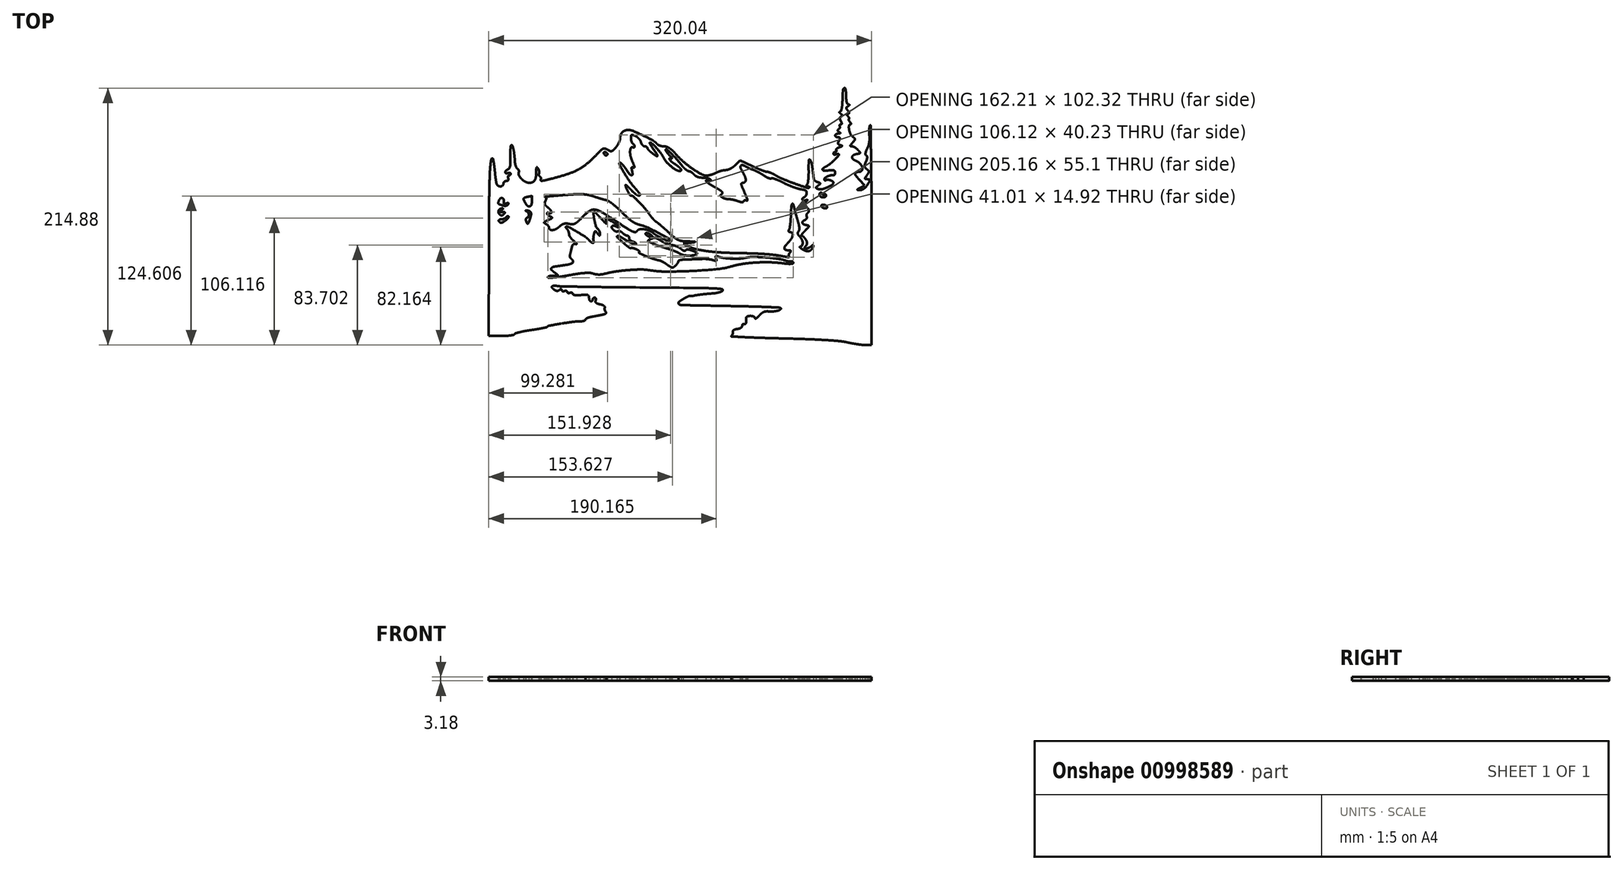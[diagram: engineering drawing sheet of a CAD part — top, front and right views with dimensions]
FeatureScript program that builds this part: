
annotation { "Feature Type Name" : "Feature", "Feature Type Description" : "" }
export const myFeature = defineFeature(function(context is Context, id is Id, definition is map)
    precondition{}
    {
        {
            var Q0;
            Q0=qCreatedBy(makeId("Top.planeOp"),FACE);
            var sketch = newSketch(context, id + "F0", { "sketchPlane" : qUnion([Q0])});
            skArc(sketch, "E0", {"start": v(136, 105.54) * mm, "mid": v(135.97, 104.96) * mm, "end": v(135.94, 104.37) * mm});
            skArc(sketch, "E1", {"start": v(135.94, 104.37) * mm, "mid": v(135.88, 103.1) * mm, "end": v(135.82, 101.84) * mm});
            skArc(sketch, "E2", {"start": v(135.82, 101.84) * mm, "mid": v(135.75, 100.34) * mm, "end": v(135.69, 98.83) * mm});
            skArc(sketch, "E3", {"start": v(135.69, 98.83) * mm, "mid": v(135.62, 97.23) * mm, "end": v(135.55, 95.63) * mm});
            skArc(sketch, "E4", {"start": v(135.55, 95.63) * mm, "mid": v(135.46, 94.03) * mm, "end": v(135.31, 92.43) * mm});
            skArc(sketch, "E5", {"start": v(135.31, 92.43) * mm, "mid": v(135.12, 91.14) * mm, "end": v(134.85, 89.87) * mm});
            skArc(sketch, "E6", {"start": v(134.85, 89.87) * mm, "mid": v(134.58, 88.96) * mm, "end": v(134.24, 88.08) * mm});
            skArc(sketch, "E7", {"start": v(134.24, 88.08) * mm, "mid": v(133.96, 87.74) * mm, "end": v(133.53, 87.6) * mm});
            skArc(sketch, "E8", {"start": v(133.53, 87.6) * mm, "mid": v(133.3, 87.57) * mm, "end": v(133.1, 87.45) * mm});
            skArc(sketch, "E9", {"start": v(133.1, 87.45) * mm, "mid": v(133, 87.3) * mm, "end": v(133, 87.12) * mm});
            skArc(sketch, "E10", {"start": v(133, 87.12) * mm, "mid": v(133.14, 86.83) * mm, "end": v(133.34, 86.6) * mm});
            skArc(sketch, "E11", {"start": v(133.34, 86.6) * mm, "mid": v(133.72, 86.27) * mm, "end": v(134.11, 85.97) * mm});
            skArc(sketch, "E12", {"start": v(134.11, 85.97) * mm, "mid": v(134.64, 85.57) * mm, "end": v(135.15, 85.14) * mm});
            skArc(sketch, "E13", {"start": v(135.15, 85.14) * mm, "mid": v(135.37, 84.87) * mm, "end": v(135.48, 84.54) * mm});
            skArc(sketch, "E14", {"start": v(135.48, 84.54) * mm, "mid": v(135.45, 84.26) * mm, "end": v(135.29, 84.03) * mm});
            skArc(sketch, "E15", {"start": v(135.29, 84.03) * mm, "mid": v(134.91, 83.78) * mm, "end": v(134.5, 83.58) * mm});
            skArc(sketch, "E16", {"start": v(134.5, 83.58) * mm, "mid": v(134.09, 83.36) * mm, "end": v(133.73, 83.05) * mm});
            skArc(sketch, "E17", {"start": v(133.73, 83.05) * mm, "mid": v(133.5, 82.71) * mm, "end": v(133.4, 82.32) * mm});
            skArc(sketch, "E18", {"start": v(133.4, 82.32) * mm, "mid": v(133.41, 81.8) * mm, "end": v(133.54, 81.31) * mm});
            skArc(sketch, "E19", {"start": v(133.54, 81.31) * mm, "mid": v(133.83, 80.59) * mm, "end": v(134.18, 79.89) * mm});
            skArc(sketch, "E20", {"start": v(134.18, 79.89) * mm, "mid": v(134.52, 79.22) * mm, "end": v(134.82, 78.53) * mm});
            skArc(sketch, "E21", {"start": v(134.82, 78.53) * mm, "mid": v(134.95, 78.1) * mm, "end": v(134.98, 77.65) * mm});
            skArc(sketch, "E22", {"start": v(134.98, 77.65) * mm, "mid": v(134.9, 77.38) * mm, "end": v(134.7, 77.16) * mm});
            skArc(sketch, "E23", {"start": v(134.7, 77.16) * mm, "mid": v(134.4, 77.01) * mm, "end": v(134.08, 76.96) * mm});
            skArc(sketch, "E24", {"start": v(134.08, 76.96) * mm, "mid": v(133.79, 76.93) * mm, "end": v(133.5, 76.85) * mm});
            skArc(sketch, "E25", {"start": v(133.5, 76.85) * mm, "mid": v(133.3, 76.73) * mm, "end": v(133.16, 76.55) * mm});
            skArc(sketch, "E26", {"start": v(133.16, 76.55) * mm, "mid": v(133.08, 76.32) * mm, "end": v(133.08, 76.08) * mm});
            skArc(sketch, "E27", {"start": v(133.08, 76.08) * mm, "mid": v(133.16, 75.8) * mm, "end": v(133.28, 75.54) * mm});
            skArc(sketch, "E28", {"start": v(133.28, 75.54) * mm, "mid": v(133.42, 75.24) * mm, "end": v(133.49, 74.92) * mm});
            skArc(sketch, "E29", {"start": v(133.49, 74.92) * mm, "mid": v(133.48, 74.57) * mm, "end": v(133.4, 74.23) * mm});
            skArc(sketch, "E30", {"start": v(133.4, 74.23) * mm, "mid": v(133.25, 73.89) * mm, "end": v(133.04, 73.58) * mm});
            skArc(sketch, "E31", {"start": v(133.04, 73.58) * mm, "mid": v(132.76, 73.3) * mm, "end": v(132.45, 73.07) * mm});
            skArc(sketch, "E32", {"start": v(132.45, 73.07) * mm, "mid": v(132.1, 72.81) * mm, "end": v(131.79, 72.5) * mm});
            skArc(sketch, "E33", {"start": v(131.79, 72.5) * mm, "mid": v(131.64, 72.25) * mm, "end": v(131.62, 71.95) * mm});
            skArc(sketch, "E34", {"start": v(131.62, 71.95) * mm, "mid": v(131.73, 71.63) * mm, "end": v(131.94, 71.36) * mm});
            skArc(sketch, "E35", {"start": v(131.94, 71.36) * mm, "mid": v(132.36, 71.01) * mm, "end": v(132.8, 70.7) * mm});
            skArc(sketch, "E36", {"start": v(132.8, 70.7) * mm, "mid": v(133.3, 70.37) * mm, "end": v(133.8, 70.01) * mm});
            skArc(sketch, "E37", {"start": v(133.8, 70.01) * mm, "mid": v(133.9, 69.85) * mm, "end": v(133.89, 69.66) * mm});
            skArc(sketch, "E38", {"start": v(133.89, 69.66) * mm, "mid": v(133.75, 69.5) * mm, "end": v(133.55, 69.42) * mm});
            skArc(sketch, "E39", {"start": v(133.55, 69.42) * mm, "mid": v(132.88, 69.38) * mm, "end": v(132.2, 69.37) * mm});
            skArc(sketch, "E40", {"start": v(132.2, 69.37) * mm, "mid": v(131.7, 69.33) * mm, "end": v(131.19, 69.24) * mm});
            skArc(sketch, "E41", {"start": v(131.19, 69.24) * mm, "mid": v(130.74, 69.1) * mm, "end": v(130.32, 68.9) * mm});
            skArc(sketch, "E42", {"start": v(130.32, 68.9) * mm, "mid": v(130.01, 68.68) * mm, "end": v(129.74, 68.4) * mm});
            skArc(sketch, "E43", {"start": v(129.74, 68.4) * mm, "mid": v(129.6, 68.13) * mm, "end": v(129.54, 67.82) * mm});
            skArc(sketch, "E44", {"start": v(129.54, 67.82) * mm, "mid": v(129.59, 67.51) * mm, "end": v(129.72, 67.24) * mm});
            skArc(sketch, "E45", {"start": v(129.72, 67.24) * mm, "mid": v(129.95, 66.96) * mm, "end": v(130.23, 66.74) * mm});
            skArc(sketch, "E46", {"start": v(130.23, 66.74) * mm, "mid": v(130.6, 66.54) * mm, "end": v(130.99, 66.4) * mm});
            skArc(sketch, "E47", {"start": v(130.99, 66.4) * mm, "mid": v(131.43, 66.32) * mm, "end": v(131.88, 66.3) * mm});
            skArc(sketch, "E48", {"start": v(131.88, 66.3) * mm, "mid": v(132.43, 66.26) * mm, "end": v(132.96, 66.15) * mm});
            skArc(sketch, "E49", {"start": v(132.96, 66.15) * mm, "mid": v(133.25, 65.98) * mm, "end": v(133.42, 65.7) * mm});
            skArc(sketch, "E50", {"start": v(133.42, 65.7) * mm, "mid": v(133.46, 65.27) * mm, "end": v(133.36, 64.87) * mm});
            skArc(sketch, "E51", {"start": v(133.36, 64.87) * mm, "mid": v(133.02, 64.1) * mm, "end": v(132.65, 63.36) * mm});
            skArc(sketch, "E52", {"start": v(132.65, 63.36) * mm, "mid": v(132.28, 62.6) * mm, "end": v(131.96, 61.82) * mm});
            skArc(sketch, "E53", {"start": v(131.96, 61.82) * mm, "mid": v(131.87, 61.35) * mm, "end": v(131.93, 60.87) * mm});
            skArc(sketch, "E54", {"start": v(131.93, 60.87) * mm, "mid": v(132.14, 60.48) * mm, "end": v(132.47, 60.2) * mm});
            skArc(sketch, "E55", {"start": v(132.47, 60.2) * mm, "mid": v(133.1, 59.92) * mm, "end": v(133.74, 59.7) * mm});
            skArc(sketch, "E56", {"start": v(133.74, 59.7) * mm, "mid": v(134.44, 59.5) * mm, "end": v(135.13, 59.28) * mm});
            skArc(sketch, "E57", {"start": v(135.13, 59.28) * mm, "mid": v(135.29, 59.13) * mm, "end": v(135.3, 58.93) * mm});
            skArc(sketch, "E58", {"start": v(135.3, 58.93) * mm, "mid": v(135.13, 58.7) * mm, "end": v(134.9, 58.55) * mm});
            skArc(sketch, "E59", {"start": v(134.9, 58.55) * mm, "mid": v(133.94, 58.22) * mm, "end": v(132.99, 57.9) * mm});
            skArc(sketch, "E60", {"start": v(132.99, 57.9) * mm, "mid": v(132.35, 57.67) * mm, "end": v(131.74, 57.38) * mm});
            skArc(sketch, "E61", {"start": v(131.74, 57.38) * mm, "mid": v(131.26, 57.09) * mm, "end": v(130.82, 56.73) * mm});
            skArc(sketch, "E62", {"start": v(130.82, 56.73) * mm, "mid": v(130.55, 56.42) * mm, "end": v(130.36, 56.05) * mm});
            skArc(sketch, "E63", {"start": v(130.36, 56.05) * mm, "mid": v(130.31, 55.75) * mm, "end": v(130.4, 55.45) * mm});
            skArc(sketch, "E64", {"start": v(130.4, 55.45) * mm, "mid": v(130.53, 55.2) * mm, "end": v(130.6, 54.94) * mm});
            skArc(sketch, "E65", {"start": v(130.6, 54.94) * mm, "mid": v(130.6, 54.71) * mm, "end": v(130.52, 54.5) * mm});
            skArc(sketch, "E66", {"start": v(130.52, 54.5) * mm, "mid": v(130.38, 54.32) * mm, "end": v(130.18, 54.2) * mm});
            skArc(sketch, "E67", {"start": v(130.18, 54.2) * mm, "mid": v(129.91, 54.13) * mm, "end": v(129.63, 54.1) * mm});
            skArc(sketch, "E68", {"start": v(129.63, 54.1) * mm, "mid": v(129.32, 54.07) * mm, "end": v(129.01, 53.99) * mm});
            skArc(sketch, "E69", {"start": v(129.01, 53.99) * mm, "mid": v(128.74, 53.85) * mm, "end": v(128.5, 53.67) * mm});
            skArc(sketch, "E70", {"start": v(128.5, 53.67) * mm, "mid": v(128.3, 53.45) * mm, "end": v(128.14, 53.19) * mm});
            skArc(sketch, "E71", {"start": v(128.14, 53.19) * mm, "mid": v(128.05, 52.91) * mm, "end": v(128.02, 52.63) * mm});
            skArc(sketch, "E72", {"start": v(128.02, 52.63) * mm, "mid": v(128.06, 52.36) * mm, "end": v(128.2, 52.14) * mm});
            skArc(sketch, "E73", {"start": v(128.2, 52.14) * mm, "mid": v(128.42, 51.95) * mm, "end": v(128.69, 51.84) * mm});
            skArc(sketch, "E74", {"start": v(128.69, 51.84) * mm, "mid": v(129.05, 51.78) * mm, "end": v(129.43, 51.8) * mm});
            skArc(sketch, "E75", {"start": v(129.43, 51.8) * mm, "mid": v(129.87, 51.89) * mm, "end": v(130.3, 52.03) * mm});
            skArc(sketch, "E76", {"start": v(130.3, 52.03) * mm, "mid": v(130.74, 52.18) * mm, "end": v(131.18, 52.3) * mm});
            skArc(sketch, "E77", {"start": v(131.18, 52.3) * mm, "mid": v(131.54, 52.37) * mm, "end": v(131.92, 52.4) * mm});
            skArc(sketch, "E78", {"start": v(131.92, 52.4) * mm, "mid": v(132.17, 52.38) * mm, "end": v(132.41, 52.31) * mm});
            skArc(sketch, "E79", {"start": v(132.41, 52.31) * mm, "mid": v(132.54, 52.21) * mm, "end": v(132.59, 52.06) * mm});
            skArc(sketch, "E80", {"start": v(132.59, 52.06) * mm, "mid": v(132.43, 51.22) * mm, "end": v(131.98, 50.5) * mm});
            skArc(sketch, "E81", {"start": v(131.98, 50.5) * mm, "mid": v(130.39, 48.82) * mm, "end": v(128.75, 47.19) * mm});
            skArc(sketch, "E82", {"start": v(128.75, 47.19) * mm, "mid": v(127.01, 45.57) * mm, "end": v(125.2, 44.02) * mm});
            skArc(sketch, "E83", {"start": v(125.2, 44.02) * mm, "mid": v(123.8, 42.98) * mm, "end": v(122.3, 42.09) * mm});
            skArc(sketch, "E84", {"start": v(122.3, 42.09) * mm, "mid": v(120.8, 41.23) * mm, "end": v(119.37, 40.28) * mm});
            skArc(sketch, "E85", {"start": v(119.37, 40.28) * mm, "mid": v(119, 39.73) * mm, "end": v(119.08, 39.07) * mm});
            skArc(sketch, "E86", {"start": v(119.08, 39.07) * mm, "mid": v(119.62, 38.52) * mm, "end": v(120.36, 38.32) * mm});
            skArc(sketch, "E87", {"start": v(120.36, 38.32) * mm, "mid": v(122.29, 38.4) * mm, "end": v(124.2, 38.57) * mm});
            skArc(sketch, "E88", {"start": v(124.2, 38.57) * mm, "mid": v(125.56, 38.7) * mm, "end": v(126.93, 38.78) * mm});
            skArc(sketch, "E89", {"start": v(126.93, 38.78) * mm, "mid": v(127.7, 38.74) * mm, "end": v(128.45, 38.55) * mm});
            skArc(sketch, "E90", {"start": v(128.45, 38.55) * mm, "mid": v(128.9, 38.28) * mm, "end": v(129.24, 37.86) * mm});
            skArc(sketch, "E91", {"start": v(129.24, 37.86) * mm, "mid": v(129.46, 37.29) * mm, "end": v(129.54, 36.68) * mm});
            skArc(sketch, "E92", {"start": v(129.54, 36.68) * mm, "mid": v(129.5, 36.2) * mm, "end": v(129.4, 35.74) * mm});
            skArc(sketch, "E93", {"start": v(129.4, 35.74) * mm, "mid": v(129.23, 35.34) * mm, "end": v(128.98, 34.99) * mm});
            skArc(sketch, "E94", {"start": v(128.98, 34.99) * mm, "mid": v(128.7, 34.73) * mm, "end": v(128.36, 34.54) * mm});
            skArc(sketch, "E95", {"start": v(128.36, 34.54) * mm, "mid": v(128, 34.45) * mm, "end": v(127.64, 34.46) * mm});
            skArc(sketch, "E96", {"start": v(127.64, 34.46) * mm, "mid": v(126.55, 34.53) * mm, "end": v(125.47, 34.4) * mm});
            skArc(sketch, "E97", {"start": v(125.47, 34.4) * mm, "mid": v(124.21, 34.03) * mm, "end": v(123, 33.54) * mm});
            skArc(sketch, "E98", {"start": v(123, 33.54) * mm, "mid": v(121.97, 32.96) * mm, "end": v(121, 32.27) * mm});
            skArc(sketch, "E99", {"start": v(121, 32.27) * mm, "mid": v(120.56, 31.7) * mm, "end": v(120.4, 30.99) * mm});
            skArc(sketch, "E100", {"start": v(120.4, 30.99) * mm, "mid": v(120.42, 30.74) * mm, "end": v(120.5, 30.5) * mm});
            skArc(sketch, "E101", {"start": v(120.5, 30.5) * mm, "mid": v(120.63, 30.33) * mm, "end": v(120.8, 30.22) * mm});
            skArc(sketch, "E102", {"start": v(120.8, 30.22) * mm, "mid": v(121.02, 30.16) * mm, "end": v(121.25, 30.18) * mm});
            skArc(sketch, "E103", {"start": v(121.25, 30.18) * mm, "mid": v(121.53, 30.26) * mm, "end": v(121.78, 30.4) * mm});
            skArc(sketch, "E104", {"start": v(121.78, 30.4) * mm, "mid": v(122.51, 30.7) * mm, "end": v(123.3, 30.76) * mm});
            skArc(sketch, "E105", {"start": v(123.3, 30.76) * mm, "mid": v(124.42, 30.6) * mm, "end": v(125.5, 30.32) * mm});
            skArc(sketch, "E106", {"start": v(125.5, 30.32) * mm, "mid": v(126.5, 29.93) * mm, "end": v(127.42, 29.42) * mm});
            skArc(sketch, "E107", {"start": v(127.42, 29.42) * mm, "mid": v(127.86, 28.97) * mm, "end": v(128.02, 28.36) * mm});
            skArc(sketch, "E108", {"start": v(128.02, 28.36) * mm, "mid": v(127.75, 27.32) * mm, "end": v(127, 26.54) * mm});
            skArc(sketch, "E109", {"start": v(127, 26.54) * mm, "mid": v(125.03, 25.4) * mm, "end": v(122.99, 24.41) * mm});
            skArc(sketch, "E110", {"start": v(122.99, 24.41) * mm, "mid": v(120.8, 23.55) * mm, "end": v(118.58, 22.84) * mm});
            skArc(sketch, "E111", {"start": v(118.58, 22.84) * mm, "mid": v(117.13, 22.66) * mm, "end": v(115.7, 22.9) * mm});
            skArc(sketch, "E112", {"start": v(115.7, 22.9) * mm, "mid": v(114.75, 23.22) * mm, "end": v(113.8, 23.56) * mm});
            skArc(sketch, "E113", {"start": v(113.8, 23.56) * mm, "mid": v(113.55, 23.75) * mm, "end": v(113.42, 24.04) * mm});
            skArc(sketch, "E114", {"start": v(113.42, 24.04) * mm, "mid": v(113.46, 24.35) * mm, "end": v(113.64, 24.61) * mm});
            skArc(sketch, "E115", {"start": v(113.64, 24.61) * mm, "mid": v(114.43, 25.24) * mm, "end": v(115.24, 25.85) * mm});
            skArc(sketch, "E116", {"start": v(115.24, 25.85) * mm, "mid": v(116.05, 26.46) * mm, "end": v(116.85, 27.1) * mm});
            skArc(sketch, "E117", {"start": v(116.85, 27.1) * mm, "mid": v(117.03, 27.35) * mm, "end": v(117.07, 27.66) * mm});
            skArc(sketch, "E118", {"start": v(117.07, 27.66) * mm, "mid": v(116.95, 27.95) * mm, "end": v(116.7, 28.13) * mm});
            skArc(sketch, "E119", {"start": v(116.7, 28.13) * mm, "mid": v(115.77, 28.47) * mm, "end": v(114.84, 28.78) * mm});
            skArc(sketch, "E120", {"start": v(114.84, 28.78) * mm, "mid": v(114.23, 29.01) * mm, "end": v(113.65, 29.3) * mm});
            skArc(sketch, "E121", {"start": v(113.65, 29.3) * mm, "mid": v(113.1, 29.64) * mm, "end": v(112.6, 30.03) * mm});
            skArc(sketch, "E122", {"start": v(112.6, 30.03) * mm, "mid": v(112.2, 30.42) * mm, "end": v(111.86, 30.85) * mm});
            skArc(sketch, "E123", {"start": v(111.86, 30.85) * mm, "mid": v(111.66, 31.23) * mm, "end": v(111.56, 31.65) * mm});
            skArc(sketch, "E124", {"start": v(111.56, 31.65) * mm, "mid": v(110.9, 37.43) * mm, "end": v(110.15, 43.2) * mm});
            skArc(sketch, "E125", {"start": v(110.15, 43.2) * mm, "mid": v(109.61, 45.37) * mm, "end": v(108.64, 47.38) * mm});
            skArc(sketch, "E126", {"start": v(108.64, 47.38) * mm, "mid": v(107.94, 47.66) * mm, "end": v(107.46, 47.08) * mm});
            skArc(sketch, "E127", {"start": v(107.46, 47.08) * mm, "mid": v(107.33, 42.78) * mm, "end": v(107.34, 38.48) * mm});
            skArc(sketch, "E128", {"start": v(107.34, 38.48) * mm, "mid": v(107.35, 36.59) * mm, "end": v(107.31, 34.7) * mm});
            skArc(sketch, "E129", {"start": v(107.31, 34.7) * mm, "mid": v(107.22, 32.94) * mm, "end": v(107.07, 31.2) * mm});
            skArc(sketch, "E130", {"start": v(107.07, 31.2) * mm, "mid": v(106.9, 29.75) * mm, "end": v(106.68, 28.31) * mm});
            skArc(sketch, "E131", {"start": v(106.68, 28.31) * mm, "mid": v(106.5, 27.65) * mm, "end": v(106.16, 27.05) * mm});
            skArc(sketch, "E132", {"start": v(106.16, 27.05) * mm, "mid": v(105.9, 26.65) * mm, "end": v(105.67, 26.22) * mm});
            skArc(sketch, "E133", {"start": v(105.67, 26.22) * mm, "mid": v(105.6, 25.93) * mm, "end": v(105.63, 25.63) * mm});
            skArc(sketch, "E134", {"start": v(105.63, 25.63) * mm, "mid": v(105.77, 25.4) * mm, "end": v(105.99, 25.27) * mm});
            skArc(sketch, "E135", {"start": v(105.99, 25.27) * mm, "mid": v(106.36, 25.18) * mm, "end": v(106.75, 25.15) * mm});
            skArc(sketch, "E136", {"start": v(106.75, 25.15) * mm, "mid": v(107.1, 25.13) * mm, "end": v(107.45, 25.1) * mm});
            skArc(sketch, "E137", {"start": v(107.45, 25.1) * mm, "mid": v(107.7, 25.03) * mm, "end": v(107.91, 24.92) * mm});
            skArc(sketch, "E138", {"start": v(107.91, 24.92) * mm, "mid": v(108.02, 24.82) * mm, "end": v(108.06, 24.67) * mm});
            skArc(sketch, "E139", {"start": v(108.06, 24.67) * mm, "mid": v(108.04, 24.52) * mm, "end": v(107.95, 24.39) * mm});
            skArc(sketch, "E140", {"start": v(107.95, 24.39) * mm, "mid": v(107.13, 23.93) * mm, "end": v(106.18, 23.97) * mm});
            skArc(sketch, "E141", {"start": v(106.18, 23.97) * mm, "mid": v(100.97, 25.74) * mm, "end": v(95.77, 27.55) * mm});
            skArc(sketch, "E142", {"start": v(95.77, 27.55) * mm, "mid": v(90.84, 29.36) * mm, "end": v(85.95, 31.27) * mm});
            skArc(sketch, "E143", {"start": v(85.95, 31.27) * mm, "mid": v(82.96, 32.63) * mm, "end": v(80.1, 34.24) * mm});
            skArc(sketch, "E144", {"start": v(80.1, 34.24) * mm, "mid": v(79.06, 34.85) * mm, "end": v(78, 35.43) * mm});
            skArc(sketch, "E145", {"start": v(78, 35.43) * mm, "mid": v(76.95, 35.95) * mm, "end": v(75.87, 36.43) * mm});
            skArc(sketch, "E146", {"start": v(75.87, 36.43) * mm, "mid": v(74.93, 36.8) * mm, "end": v(73.98, 37.14) * mm});
            skArc(sketch, "E147", {"start": v(73.98, 37.14) * mm, "mid": v(73.38, 37.29) * mm, "end": v(72.76, 37.34) * mm});
            skArc(sketch, "E148", {"start": v(72.76, 37.34) * mm, "mid": v(72.05, 37.4) * mm, "end": v(71.35, 37.57) * mm});
            skArc(sketch, "E149", {"start": v(71.35, 37.57) * mm, "mid": v(69.74, 38.14) * mm, "end": v(68.14, 38.74) * mm});
            skArc(sketch, "E150", {"start": v(68.14, 38.74) * mm, "mid": v(66.23, 39.49) * mm, "end": v(64.34, 40.28) * mm});
            skArc(sketch, "E151", {"start": v(64.34, 40.28) * mm, "mid": v(62.3, 41.17) * mm, "end": v(60.27, 42.1) * mm});
            skLineSegment(sketch, "E152", {"start": v(60.27, 42.1) * mm, "end": v(50.1, 46.86) * mm});
            skLineSegment(sketch, "E153", {"start": v(50.1, 46.86) * mm, "end": v(45.92, 42.86) * mm});
            skArc(sketch, "E154", {"start": v(45.92, 42.86) * mm, "mid": v(45.01, 42.06) * mm, "end": v(44.05, 41.33) * mm});
            skArc(sketch, "E155", {"start": v(44.05, 41.33) * mm, "mid": v(42.98, 40.65) * mm, "end": v(41.87, 40.03) * mm});
            skArc(sketch, "E156", {"start": v(41.87, 40.03) * mm, "mid": v(40.82, 39.55) * mm, "end": v(39.74, 39.14) * mm});
            skArc(sketch, "E157", {"start": v(39.74, 39.14) * mm, "mid": v(38.9, 38.93) * mm, "end": v(38.02, 38.85) * mm});
            skArc(sketch, "E158", {"start": v(38.02, 38.85) * mm, "mid": v(37.14, 38.81) * mm, "end": v(36.28, 38.69) * mm});
            skArc(sketch, "E159", {"start": v(36.28, 38.69) * mm, "mid": v(35.18, 38.46) * mm, "end": v(34.1, 38.18) * mm});
            skArc(sketch, "E160", {"start": v(34.1, 38.18) * mm, "mid": v(32.98, 37.83) * mm, "end": v(31.87, 37.44) * mm});
            skArc(sketch, "E161", {"start": v(31.87, 37.44) * mm, "mid": v(30.88, 37.03) * mm, "end": v(29.92, 36.57) * mm});
            skArc(sketch, "E162", {"start": v(29.92, 36.57) * mm, "mid": v(28.97, 36.1) * mm, "end": v(28, 35.7) * mm});
            skArc(sketch, "E163", {"start": v(28, 35.7) * mm, "mid": v(26.92, 35.3) * mm, "end": v(25.82, 34.96) * mm});
            skArc(sketch, "E164", {"start": v(25.82, 34.96) * mm, "mid": v(24.78, 34.68) * mm, "end": v(23.72, 34.45) * mm});
            skArc(sketch, "E165", {"start": v(23.72, 34.45) * mm, "mid": v(22.9, 34.33) * mm, "end": v(22.08, 34.3) * mm});
            skArc(sketch, "E166", {"start": v(22.08, 34.3) * mm, "mid": v(19.75, 34.59) * mm, "end": v(17.57, 35.46) * mm});
            skArc(sketch, "E167", {"start": v(17.57, 35.46) * mm, "mid": v(13.88, 37.63) * mm, "end": v(10.3, 39.97) * mm});
            skArc(sketch, "E168", {"start": v(10.3, 39.97) * mm, "mid": v(6.45, 42.78) * mm, "end": v(2.75, 45.78) * mm});
            skArc(sketch, "E169", {"start": v(2.75, 45.79) * mm, "mid": v(-0.44, 48.72) * mm, "end": v(-3.42, 51.87) * mm});
            skArc(sketch, "E170", {"start": v(-3.42, 51.87) * mm, "mid": v(-4.92, 53.52) * mm, "end": v(-6.48, 55.1) * mm});
            skArc(sketch, "E171", {"start": v(-6.48, 55.1) * mm, "mid": v(-7.7, 56.18) * mm, "end": v(-9.02, 57.15) * mm});
            skArc(sketch, "E172", {"start": v(-9.02, 57.15) * mm, "mid": v(-10.13, 57.8) * mm, "end": v(-11.33, 58.29) * mm});
            skArc(sketch, "E173", {"start": v(-11.33, 58.29) * mm, "mid": v(-12.48, 58.58) * mm, "end": v(-13.66, 58.67) * mm});
            skArc(sketch, "E174", {"start": v(-13.66, 58.67) * mm, "mid": v(-14.55, 58.72) * mm, "end": v(-15.44, 58.85) * mm});
            skArc(sketch, "E175", {"start": v(-15.44, 58.85) * mm, "mid": v(-16.36, 59.08) * mm, "end": v(-17.26, 59.39) * mm});
            skArc(sketch, "E176", {"start": v(-17.26, 59.39) * mm, "mid": v(-18.07, 59.75) * mm, "end": v(-18.85, 60.18) * mm});
            skArc(sketch, "E177", {"start": v(-18.85, 60.18) * mm, "mid": v(-19.43, 60.6) * mm, "end": v(-19.93, 61.1) * mm});
            skArc(sketch, "E178", {"start": v(-19.94, 61.1) * mm, "mid": v(-21.46, 62.63) * mm, "end": v(-23.25, 63.83) * mm});
            skArc(sketch, "E179", {"start": v(-23.25, 63.83) * mm, "mid": v(-27.24, 65.92) * mm, "end": v(-31.28, 67.9) * mm});
            skArc(sketch, "E180", {"start": v(-31.28, 67.9) * mm, "mid": v(-35.38, 69.8) * mm, "end": v(-39.52, 71.57) * mm});
            skArc(sketch, "E181", {"start": v(-39.52, 71.57) * mm, "mid": v(-41.55, 72.18) * mm, "end": v(-43.66, 72.4) * mm});
            skArc(sketch, "E182", {"start": v(-43.66, 72.39) * mm, "mid": v(-45.02, 72.26) * mm, "end": v(-46.33, 71.88) * mm});
            skArc(sketch, "E183", {"start": v(-46.33, 71.88) * mm, "mid": v(-47.47, 71.27) * mm, "end": v(-48.46, 70.43) * mm});
            skArc(sketch, "E184", {"start": v(-48.46, 70.43) * mm, "mid": v(-49.26, 69.37) * mm, "end": v(-49.82, 68.16) * mm});
            skArc(sketch, "E185", {"start": v(-49.82, 68.16) * mm, "mid": v(-50.17, 66.76) * mm, "end": v(-50.3, 65.31) * mm});
            skArc(sketch, "E186", {"start": v(-50.3, 65.31) * mm, "mid": v(-50.35, 64.5) * mm, "end": v(-50.54, 63.71) * mm});
            skArc(sketch, "E187", {"start": v(-50.54, 63.71) * mm, "mid": v(-50.9, 62.7) * mm, "end": v(-51.33, 61.7) * mm});
            skArc(sketch, "E188", {"start": v(-51.33, 61.7) * mm, "mid": v(-51.86, 60.64) * mm, "end": v(-52.46, 59.62) * mm});
            skArc(sketch, "E189", {"start": v(-52.46, 59.62) * mm, "mid": v(-53.1, 58.69) * mm, "end": v(-53.81, 57.8) * mm});
            skArc(sketch, "E190", {"start": v(-53.81, 57.8) * mm, "mid": v(-54.86, 56.63) * mm, "end": v(-55.95, 55.5) * mm});
            skArc(sketch, "E191", {"start": v(-55.95, 55.5) * mm, "mid": v(-56.58, 55.01) * mm, "end": v(-57.3, 54.7) * mm});
            skArc(sketch, "E192", {"start": v(-57.3, 54.7) * mm, "mid": v(-58, 54.62) * mm, "end": v(-58.67, 54.78) * mm});
            skArc(sketch, "E193", {"start": v(-58.67, 54.78) * mm, "mid": v(-59.7, 55.25) * mm, "end": v(-60.69, 55.81) * mm});
            skArc(sketch, "E194", {"start": v(-60.69, 55.81) * mm, "mid": v(-61.7, 56.36) * mm, "end": v(-62.76, 56.79) * mm});
            skArc(sketch, "E195", {"start": v(-62.76, 56.79) * mm, "mid": v(-63.54, 56.9) * mm, "end": v(-64.3, 56.75) * mm});
            skArc(sketch, "E196", {"start": v(-64.3, 56.75) * mm, "mid": v(-65.21, 56.3) * mm, "end": v(-66, 55.68) * mm});
            skArc(sketch, "E197", {"start": v(-66, 55.68) * mm, "mid": v(-67.56, 54.15) * mm, "end": v(-69.08, 52.58) * mm});
            skArc(sketch, "E198", {"start": v(-69.08, 52.58) * mm, "mid": v(-73.1, 48.53) * mm, "end": v(-77.34, 44.7) * mm});
            skArc(sketch, "E199", {"start": v(-77.34, 44.7) * mm, "mid": v(-80.95, 41.9) * mm, "end": v(-84.83, 39.5) * mm});
            skArc(sketch, "E200", {"start": v(-84.83, 39.5) * mm, "mid": v(-89.19, 37.36) * mm, "end": v(-93.73, 35.63) * mm});
            skArc(sketch, "E201", {"start": v(-93.73, 35.63) * mm, "mid": v(-100.17, 33.64) * mm, "end": v(-106.68, 31.87) * mm});
            skArc(sketch, "E202", {"start": v(-106.68, 31.87) * mm, "mid": v(-109.97, 31.06) * mm, "end": v(-113.26, 30.27) * mm});
            skArc(sketch, "E203", {"start": v(-113.26, 30.27) * mm, "mid": v(-114.54, 30.01) * mm, "end": v(-115.84, 29.87) * mm});
            skArc(sketch, "E204", {"start": v(-115.84, 29.87) * mm, "mid": v(-116.3, 29.96) * mm, "end": v(-116.64, 30.26) * mm});
            skArc(sketch, "E205", {"start": v(-116.64, 30.26) * mm, "mid": v(-116.77, 30.7) * mm, "end": v(-116.65, 31.14) * mm});
            skArc(sketch, "E206", {"start": v(-116.65, 31.14) * mm, "mid": v(-116.51, 31.43) * mm, "end": v(-116.44, 31.75) * mm});
            skArc(sketch, "E207", {"start": v(-116.44, 31.75) * mm, "mid": v(-116.43, 32.1) * mm, "end": v(-116.5, 32.42) * mm});
            skArc(sketch, "E208", {"start": v(-116.5, 32.42) * mm, "mid": v(-116.62, 32.75) * mm, "end": v(-116.81, 33.05) * mm});
            skArc(sketch, "E209", {"start": v(-116.81, 33.05) * mm, "mid": v(-117.06, 33.31) * mm, "end": v(-117.35, 33.53) * mm});
            skArc(sketch, "E210", {"start": v(-117.35, 33.53) * mm, "mid": v(-117.64, 33.74) * mm, "end": v(-117.88, 34) * mm});
            skArc(sketch, "E211", {"start": v(-117.88, 34) * mm, "mid": v(-118.07, 34.3) * mm, "end": v(-118.2, 34.63) * mm});
            skArc(sketch, "E212", {"start": v(-118.2, 34.63) * mm, "mid": v(-118.27, 34.96) * mm, "end": v(-118.26, 35.3) * mm});
            skArc(sketch, "E213", {"start": v(-118.26, 35.3) * mm, "mid": v(-118.2, 35.61) * mm, "end": v(-118.05, 35.9) * mm});
            skArc(sketch, "E214", {"start": v(-118.05, 35.9) * mm, "mid": v(-117.9, 36.26) * mm, "end": v(-117.83, 36.64) * mm});
            skArc(sketch, "E215", {"start": v(-117.83, 36.64) * mm, "mid": v(-117.84, 37.16) * mm, "end": v(-117.9, 37.69) * mm});
            skArc(sketch, "E216", {"start": v(-117.9, 37.69) * mm, "mid": v(-118.03, 38.28) * mm, "end": v(-118.21, 38.86) * mm});
            skArc(sketch, "E217", {"start": v(-118.21, 38.86) * mm, "mid": v(-118.45, 39.44) * mm, "end": v(-118.74, 40) * mm});
            skArc(sketch, "E218", {"start": v(-118.74, 40) * mm, "mid": v(-119.15, 40.64) * mm, "end": v(-119.59, 41.27) * mm});
            skArc(sketch, "E219", {"start": v(-119.59, 41.27) * mm, "mid": v(-119.8, 41.38) * mm, "end": v(-120.02, 41.27) * mm});
            skArc(sketch, "E220", {"start": v(-120.02, 41.27) * mm, "mid": v(-120.2, 40.92) * mm, "end": v(-120.28, 40.52) * mm});
            skArc(sketch, "E221", {"start": v(-120.28, 40.52) * mm, "mid": v(-120.33, 39.18) * mm, "end": v(-120.35, 37.84) * mm});
            skArc(sketch, "E222", {"start": v(-120.35, 37.84) * mm, "mid": v(-120.44, 35.5) * mm, "end": v(-120.67, 33.15) * mm});
            skArc(sketch, "E223", {"start": v(-120.67, 33.15) * mm, "mid": v(-121.02, 31.67) * mm, "end": v(-121.65, 30.3) * mm});
            skArc(sketch, "E224", {"start": v(-121.65, 30.3) * mm, "mid": v(-122.41, 29.38) * mm, "end": v(-123.42, 28.75) * mm});
            skArc(sketch, "E225", {"start": v(-123.42, 28.75) * mm, "mid": v(-124.73, 28.33) * mm, "end": v(-126.1, 28.2) * mm});
            skArc(sketch, "E226", {"start": v(-126.1, 28.2) * mm, "mid": v(-127.76, 28.4) * mm, "end": v(-129.33, 29) * mm});
            skArc(sketch, "E227", {"start": v(-129.33, 29) * mm, "mid": v(-131.04, 30.07) * mm, "end": v(-132.59, 31.37) * mm});
            skArc(sketch, "E228", {"start": v(-132.59, 31.37) * mm, "mid": v(-133.82, 32.77) * mm, "end": v(-134.82, 34.33) * mm});
            skArc(sketch, "E229", {"start": v(-134.82, 34.33) * mm, "mid": v(-135.18, 35.56) * mm, "end": v(-134.99, 36.83) * mm});
            skArc(sketch, "E230", {"start": v(-134.99, 36.83) * mm, "mid": v(-134.87, 37.24) * mm, "end": v(-134.84, 37.66) * mm});
            skArc(sketch, "E231", {"start": v(-134.84, 37.66) * mm, "mid": v(-134.88, 38.12) * mm, "end": v(-135, 38.56) * mm});
            skArc(sketch, "E232", {"start": v(-135, 38.56) * mm, "mid": v(-135.18, 38.98) * mm, "end": v(-135.43, 39.37) * mm});
            skArc(sketch, "E233", {"start": v(-135.43, 39.37) * mm, "mid": v(-135.73, 39.7) * mm, "end": v(-136.08, 39.96) * mm});
            skArc(sketch, "E234", {"start": v(-136.08, 39.96) * mm, "mid": v(-136.5, 40.3) * mm, "end": v(-136.8, 40.73) * mm});
            skArc(sketch, "E235", {"start": v(-136.8, 40.73) * mm, "mid": v(-137.16, 41.43) * mm, "end": v(-137.46, 42.14) * mm});
            skArc(sketch, "E236", {"start": v(-137.46, 42.14) * mm, "mid": v(-137.73, 43) * mm, "end": v(-137.94, 43.88) * mm});
            skArc(sketch, "E237", {"start": v(-137.94, 43.88) * mm, "mid": v(-138.1, 44.8) * mm, "end": v(-138.18, 45.72) * mm});
            skArc(sketch, "E238", {"start": v(-138.18, 45.72) * mm, "mid": v(-138.35, 48.23) * mm, "end": v(-138.57, 50.73) * mm});
            skArc(sketch, "E239", {"start": v(-138.57, 50.73) * mm, "mid": v(-138.84, 52.86) * mm, "end": v(-139.18, 54.98) * mm});
            skArc(sketch, "E240", {"start": v(-139.18, 54.98) * mm, "mid": v(-139.52, 56.64) * mm, "end": v(-139.91, 58.28) * mm});
            skArc(sketch, "E241", {"start": v(-139.91, 58.28) * mm, "mid": v(-140.22, 59.04) * mm, "end": v(-140.72, 59.7) * mm});
            skArc(sketch, "E242", {"start": v(-140.72, 59.7) * mm, "mid": v(-141.1, 59.8) * mm, "end": v(-141.4, 59.53) * mm});
            skArc(sketch, "E243", {"start": v(-141.4, 59.53) * mm, "mid": v(-141.68, 58.51) * mm, "end": v(-141.83, 57.47) * mm});
            skArc(sketch, "E244", {"start": v(-141.83, 57.47) * mm, "mid": v(-141.97, 55.46) * mm, "end": v(-142.01, 53.45) * mm});
            skArc(sketch, "E245", {"start": v(-142.01, 53.45) * mm, "mid": v(-141.99, 50.13) * mm, "end": v(-141.92, 46.81) * mm});
            skArc(sketch, "E246", {"start": v(-141.92, 46.81) * mm, "mid": v(-141.92, 45.3) * mm, "end": v(-141.97, 43.8) * mm});
            skArc(sketch, "E247", {"start": v(-141.97, 43.8) * mm, "mid": v(-142.1, 42.72) * mm, "end": v(-142.34, 41.65) * mm});
            skArc(sketch, "E248", {"start": v(-142.34, 41.65) * mm, "mid": v(-142.63, 40.9) * mm, "end": v(-143.02, 40.2) * mm});
            skArc(sketch, "E249", {"start": v(-143.02, 40.2) * mm, "mid": v(-143.47, 39.73) * mm, "end": v(-144.03, 39.4) * mm});
            skArc(sketch, "E250", {"start": v(-144.03, 39.4) * mm, "mid": v(-144.48, 39.2) * mm, "end": v(-144.9, 38.96) * mm});
            skArc(sketch, "E251", {"start": v(-144.9, 38.96) * mm, "mid": v(-145.29, 38.67) * mm, "end": v(-145.64, 38.34) * mm});
            skArc(sketch, "E252", {"start": v(-145.64, 38.34) * mm, "mid": v(-145.9, 38.02) * mm, "end": v(-146.14, 37.66) * mm});
            skArc(sketch, "E253", {"start": v(-146.14, 37.66) * mm, "mid": v(-146.26, 37.35) * mm, "end": v(-146.3, 37.01) * mm});
            skArc(sketch, "E254", {"start": v(-146.3, 37.01) * mm, "mid": v(-146.26, 36.74) * mm, "end": v(-146.12, 36.5) * mm});
            skArc(sketch, "E255", {"start": v(-146.12, 36.5) * mm, "mid": v(-145.9, 36.31) * mm, "end": v(-145.63, 36.2) * mm});
            skArc(sketch, "E256", {"start": v(-145.63, 36.2) * mm, "mid": v(-145.27, 36.13) * mm, "end": v(-144.9, 36.14) * mm});
            skArc(sketch, "E257", {"start": v(-144.9, 36.14) * mm, "mid": v(-144.45, 36.23) * mm, "end": v(-144.02, 36.37) * mm});
            skArc(sketch, "E258", {"start": v(-144.02, 36.37) * mm, "mid": v(-143.59, 36.5) * mm, "end": v(-143.14, 36.6) * mm});
            skArc(sketch, "E259", {"start": v(-143.14, 36.6) * mm, "mid": v(-142.77, 36.6) * mm, "end": v(-142.4, 36.55) * mm});
            skArc(sketch, "E260", {"start": v(-142.4, 36.55) * mm, "mid": v(-142.14, 36.44) * mm, "end": v(-141.92, 36.25) * mm});
            skArc(sketch, "E261", {"start": v(-141.92, 36.25) * mm, "mid": v(-141.78, 36.03) * mm, "end": v(-141.73, 35.77) * mm});
            skArc(sketch, "E262", {"start": v(-141.73, 35.77) * mm, "mid": v(-141.76, 35.48) * mm, "end": v(-141.84, 35.2) * mm});
            skArc(sketch, "E263", {"start": v(-141.84, 35.2) * mm, "mid": v(-141.98, 34.95) * mm, "end": v(-142.17, 34.72) * mm});
            skArc(sketch, "E264", {"start": v(-142.17, 34.72) * mm, "mid": v(-142.39, 34.54) * mm, "end": v(-142.64, 34.4) * mm});
            skArc(sketch, "E265", {"start": v(-142.64, 34.4) * mm, "mid": v(-142.92, 34.32) * mm, "end": v(-143.2, 34.3) * mm});
            skArc(sketch, "E266", {"start": v(-143.2, 34.3) * mm, "mid": v(-143.47, 34.24) * mm, "end": v(-143.7, 34.1) * mm});
            skArc(sketch, "E267", {"start": v(-143.7, 34.1) * mm, "mid": v(-143.88, 33.88) * mm, "end": v(-144, 33.62) * mm});
            skArc(sketch, "E268", {"start": v(-144, 33.62) * mm, "mid": v(-144.05, 33.25) * mm, "end": v(-144.03, 32.88) * mm});
            skArc(sketch, "E269", {"start": v(-144.03, 32.88) * mm, "mid": v(-143.95, 32.44) * mm, "end": v(-143.8, 32) * mm});
            skArc(sketch, "E270", {"start": v(-143.8, 32) * mm, "mid": v(-143.67, 31.53) * mm, "end": v(-143.6, 31.04) * mm});
            skArc(sketch, "E271", {"start": v(-143.6, 31.04) * mm, "mid": v(-143.64, 30.66) * mm, "end": v(-143.8, 30.32) * mm});
            skArc(sketch, "E272", {"start": v(-143.8, 30.32) * mm, "mid": v(-144.07, 30.04) * mm, "end": v(-144.4, 29.87) * mm});
            skArc(sketch, "E273", {"start": v(-144.4, 29.87) * mm, "mid": v(-144.89, 29.76) * mm, "end": v(-145.38, 29.72) * mm});
            skArc(sketch, "E274", {"start": v(-145.38, 29.72) * mm, "mid": v(-145.85, 29.67) * mm, "end": v(-146.31, 29.54) * mm});
            skArc(sketch, "E275", {"start": v(-146.31, 29.54) * mm, "mid": v(-146.74, 29.33) * mm, "end": v(-147.1, 29.05) * mm});
            skArc(sketch, "E276", {"start": v(-147.1, 29.05) * mm, "mid": v(-147.41, 28.7) * mm, "end": v(-147.64, 28.3) * mm});
            skArc(sketch, "E277", {"start": v(-147.64, 28.3) * mm, "mid": v(-147.78, 27.88) * mm, "end": v(-147.83, 27.43) * mm});
            skArc(sketch, "E278", {"start": v(-147.83, 27.43) * mm, "mid": v(-147.98, 26.64) * mm, "end": v(-148.43, 25.97) * mm});
            skArc(sketch, "E279", {"start": v(-148.43, 25.97) * mm, "mid": v(-149.13, 25.46) * mm, "end": v(-149.95, 25.2) * mm});
            skArc(sketch, "E280", {"start": v(-149.95, 25.2) * mm, "mid": v(-150.9, 25.21) * mm, "end": v(-151.8, 25.48) * mm});
            skArc(sketch, "E281", {"start": v(-151.8, 25.48) * mm, "mid": v(-152.58, 25.99) * mm, "end": v(-153.18, 26.7) * mm});
            skArc(sketch, "E282", {"start": v(-153.18, 26.7) * mm, "mid": v(-153.43, 27.19) * mm, "end": v(-153.59, 27.72) * mm});
            skArc(sketch, "E283", {"start": v(-153.59, 27.72) * mm, "mid": v(-153.83, 28.92) * mm, "end": v(-154.05, 30.13) * mm});
            skArc(sketch, "E284", {"start": v(-154.05, 30.13) * mm, "mid": v(-154.28, 31.6) * mm, "end": v(-154.47, 33.05) * mm});
            skArc(sketch, "E285", {"start": v(-154.47, 33.05) * mm, "mid": v(-154.65, 34.64) * mm, "end": v(-154.8, 36.22) * mm});
            skArc(sketch, "E286", {"start": v(-154.8, 36.22) * mm, "mid": v(-154.94, 37.89) * mm, "end": v(-155.12, 39.55) * mm});
            skArc(sketch, "E287", {"start": v(-155.12, 39.55) * mm, "mid": v(-155.32, 41.26) * mm, "end": v(-155.55, 42.97) * mm});
            skArc(sketch, "E288", {"start": v(-155.55, 42.97) * mm, "mid": v(-155.78, 44.5) * mm, "end": v(-156.02, 46.01) * mm});
            skArc(sketch, "E289", {"start": v(-156.02, 46.01) * mm, "mid": v(-156.22, 47.01) * mm, "end": v(-156.45, 48) * mm});
            skArc(sketch, "E290", {"start": v(-156.45, 48) * mm, "mid": v(-157.25, 48.6) * mm, "end": v(-158, 47.93) * mm});
            skArc(sketch, "E291", {"start": v(-158, 47.93) * mm, "mid": v(-158.69, 42.62) * mm, "end": v(-159.08, 37.28) * mm});
            skArc(sketch, "E292", {"start": v(-159.08, 37.28) * mm, "mid": v(-159.51, 25.18) * mm, "end": v(-159.72, 13.07) * mm});
            skArc(sketch, "E293", {"start": v(-159.72, 13.07) * mm, "mid": v(-159.87, -8.51) * mm, "end": v(-159.93, -30.1) * mm});
            skLineSegment(sketch, "E294", {"start": v(-159.93, -30.1) * mm, "end": v(-160.02, -99.82) * mm});
            skLineSegment(sketch, "E295", {"start": v(-160.02, -99.82) * mm, "end": v(-149.48, -99.82) * mm});
            skArc(sketch, "E296", {"start": v(-149.48, -99.82) * mm, "mid": v(-147.44, -99.8) * mm, "end": v(-145.4, -99.71) * mm});
            skArc(sketch, "E297", {"start": v(-145.4, -99.71) * mm, "mid": v(-143.64, -99.58) * mm, "end": v(-141.89, -99.37) * mm});
            skArc(sketch, "E298", {"start": v(-141.89, -99.37) * mm, "mid": v(-140.5, -99.16) * mm, "end": v(-139.1, -98.9) * mm});
            skArc(sketch, "E299", {"start": v(-139.1, -98.9) * mm, "mid": v(-138.69, -98.69) * mm, "end": v(-138.43, -98.3) * mm});
            skArc(sketch, "E300", {"start": v(-138.43, -98.3) * mm, "mid": v(-138.16, -97.87) * mm, "end": v(-137.73, -97.62) * mm});
            skArc(sketch, "E301", {"start": v(-137.73, -97.62) * mm, "mid": v(-136, -97.13) * mm, "end": v(-134.27, -96.68) * mm});
            skArc(sketch, "E302", {"start": v(-134.27, -96.68) * mm, "mid": v(-132.12, -96.18) * mm, "end": v(-129.97, -95.75) * mm});
            skArc(sketch, "E303", {"start": v(-129.97, -95.75) * mm, "mid": v(-127.47, -95.31) * mm, "end": v(-124.97, -94.93) * mm});
            skArc(sketch, "E304", {"start": v(-124.97, -94.93) * mm, "mid": v(-122.46, -94.56) * mm, "end": v(-119.95, -94.16) * mm});
            skArc(sketch, "E305", {"start": v(-119.95, -94.16) * mm, "mid": v(-117.77, -93.79) * mm, "end": v(-115.6, -93.37) * mm});
            skArc(sketch, "E306", {"start": v(-115.6, -93.37) * mm, "mid": v(-113.77, -93) * mm, "end": v(-111.94, -92.62) * mm});
            skArc(sketch, "E307", {"start": v(-111.94, -92.62) * mm, "mid": v(-111.56, -92.47) * mm, "end": v(-111.25, -92.2) * mm});
            skArc(sketch, "E308", {"start": v(-111.25, -92.2) * mm, "mid": v(-110.5, -91.6) * mm, "end": v(-109.59, -91.26) * mm});
            skArc(sketch, "E309", {"start": v(-109.59, -91.26) * mm, "mid": v(-104.48, -90.36) * mm, "end": v(-99.36, -89.49) * mm});
            skArc(sketch, "E310", {"start": v(-99.36, -89.49) * mm, "mid": v(-94.5, -88.72) * mm, "end": v(-89.62, -88.02) * mm});
            skArc(sketch, "E311", {"start": v(-89.62, -88.02) * mm, "mid": v(-86.71, -87.73) * mm, "end": v(-83.8, -87.63) * mm});
            skArc(sketch, "E312", {"start": v(-83.8, -87.63) * mm, "mid": v(-82.92, -87.6) * mm, "end": v(-82.05, -87.53) * mm});
            skArc(sketch, "E313", {"start": v(-82.05, -87.53) * mm, "mid": v(-81.3, -87.4) * mm, "end": v(-80.58, -87.22) * mm});
            skArc(sketch, "E314", {"start": v(-80.58, -87.22) * mm, "mid": v(-80.06, -87.02) * mm, "end": v(-79.56, -86.77) * mm});
            skArc(sketch, "E315", {"start": v(-79.56, -86.77) * mm, "mid": v(-79.33, -86.54) * mm, "end": v(-79.25, -86.23) * mm});
            skArc(sketch, "E316", {"start": v(-79.25, -86.23) * mm, "mid": v(-79.17, -85.9) * mm, "end": v(-78.95, -85.63) * mm});
            skArc(sketch, "E317", {"start": v(-78.95, -85.63) * mm, "mid": v(-78.44, -85.28) * mm, "end": v(-77.9, -84.98) * mm});
            skArc(sketch, "E318", {"start": v(-77.9, -84.98) * mm, "mid": v(-77.18, -84.65) * mm, "end": v(-76.43, -84.38) * mm});
            skArc(sketch, "E319", {"start": v(-76.43, -84.38) * mm, "mid": v(-75.56, -84.14) * mm, "end": v(-74.68, -83.94) * mm});
            skArc(sketch, "E320", {"start": v(-74.68, -83.94) * mm, "mid": v(-73.63, -83.74) * mm, "end": v(-72.58, -83.54) * mm});
            skArc(sketch, "E321", {"start": v(-72.58, -83.54) * mm, "mid": v(-71.32, -83.3) * mm, "end": v(-70.06, -83.05) * mm});
            skArc(sketch, "E322", {"start": v(-70.06, -83.05) * mm, "mid": v(-68.8, -82.8) * mm, "end": v(-67.52, -82.56) * mm});
            skArc(sketch, "E323", {"start": v(-67.52, -82.56) * mm, "mid": v(-66.45, -82.35) * mm, "end": v(-65.38, -82.14) * mm});
            skArc(sketch, "E324", {"start": v(-65.38, -82.14) * mm, "mid": v(-64.35, -81.92) * mm, "end": v(-63.32, -81.64) * mm});
            skArc(sketch, "E325", {"start": v(-63.32, -81.64) * mm, "mid": v(-62.73, -81.41) * mm, "end": v(-62.2, -81.07) * mm});
            skArc(sketch, "E326", {"start": v(-62.2, -81.07) * mm, "mid": v(-61.96, -80.78) * mm, "end": v(-61.9, -80.4) * mm});
            skArc(sketch, "E327", {"start": v(-61.9, -80.4) * mm, "mid": v(-61.98, -80) * mm, "end": v(-62.21, -79.67) * mm});
            skArc(sketch, "E328", {"start": v(-62.21, -79.67) * mm, "mid": v(-62.51, -79.32) * mm, "end": v(-62.75, -78.93) * mm});
            skArc(sketch, "E329", {"start": v(-62.75, -78.93) * mm, "mid": v(-62.96, -78.49) * mm, "end": v(-63.1, -78.02) * mm});
            skArc(sketch, "E330", {"start": v(-63.1, -78.02) * mm, "mid": v(-63.18, -77.54) * mm, "end": v(-63.2, -77.06) * mm});
            skArc(sketch, "E331", {"start": v(-63.2, -77.06) * mm, "mid": v(-63.16, -76.63) * mm, "end": v(-63.04, -76.22) * mm});
            skArc(sketch, "E332", {"start": v(-63.04, -76.22) * mm, "mid": v(-62.98, -75.8) * mm, "end": v(-63.09, -75.38) * mm});
            skArc(sketch, "E333", {"start": v(-63.09, -75.38) * mm, "mid": v(-63.38, -74.95) * mm, "end": v(-63.77, -74.6) * mm});
            skArc(sketch, "E334", {"start": v(-63.77, -74.6) * mm, "mid": v(-64.4, -74.2) * mm, "end": v(-65.08, -73.9) * mm});
            skArc(sketch, "E335", {"start": v(-65.08, -73.9) * mm, "mid": v(-66, -73.62) * mm, "end": v(-66.94, -73.4) * mm});
            skArc(sketch, "E336", {"start": v(-66.94, -73.4) * mm, "mid": v(-68.02, -73.16) * mm, "end": v(-69.08, -72.85) * mm});
            skArc(sketch, "E337", {"start": v(-69.08, -72.85) * mm, "mid": v(-69.72, -72.56) * mm, "end": v(-70.3, -72.16) * mm});
            skArc(sketch, "E338", {"start": v(-70.3, -72.16) * mm, "mid": v(-70.62, -71.76) * mm, "end": v(-70.8, -71.27) * mm});
            skArc(sketch, "E339", {"start": v(-70.8, -71.27) * mm, "mid": v(-70.8, -70.7) * mm, "end": v(-70.67, -70.15) * mm});
            skArc(sketch, "E340", {"start": v(-70.67, -70.15) * mm, "mid": v(-70.53, -69.7) * mm, "end": v(-70.45, -69.26) * mm});
            skArc(sketch, "E341", {"start": v(-70.45, -69.26) * mm, "mid": v(-70.45, -68.88) * mm, "end": v(-70.54, -68.5) * mm});
            skArc(sketch, "E342", {"start": v(-70.54, -68.5) * mm, "mid": v(-70.68, -68.23) * mm, "end": v(-70.9, -68) * mm});
            skArc(sketch, "E343", {"start": v(-70.9, -68) * mm, "mid": v(-71.17, -67.87) * mm, "end": v(-71.46, -67.82) * mm});
            skArc(sketch, "E344", {"start": v(-71.46, -67.82) * mm, "mid": v(-71.8, -67.85) * mm, "end": v(-72.1, -67.93) * mm});
            skArc(sketch, "E345", {"start": v(-72.1, -67.93) * mm, "mid": v(-72.4, -68.07) * mm, "end": v(-72.66, -68.27) * mm});
            skArc(sketch, "E346", {"start": v(-72.66, -68.27) * mm, "mid": v(-72.86, -68.5) * mm, "end": v(-73.02, -68.76) * mm});
            skArc(sketch, "E347", {"start": v(-73.02, -68.76) * mm, "mid": v(-73.12, -69.04) * mm, "end": v(-73.15, -69.34) * mm});
            skArc(sketch, "E348", {"start": v(-73.15, -69.34) * mm, "mid": v(-73.18, -69.64) * mm, "end": v(-73.27, -69.92) * mm});
            skArc(sketch, "E349", {"start": v(-73.27, -69.92) * mm, "mid": v(-73.4, -70.19) * mm, "end": v(-73.6, -70.42) * mm});
            skArc(sketch, "E350", {"start": v(-73.6, -70.42) * mm, "mid": v(-73.83, -70.6) * mm, "end": v(-74.1, -70.75) * mm});
            skArc(sketch, "E351", {"start": v(-74.1, -70.75) * mm, "mid": v(-74.38, -70.84) * mm, "end": v(-74.68, -70.87) * mm});
            skArc(sketch, "E352", {"start": v(-74.68, -70.87) * mm, "mid": v(-74.99, -70.8) * mm, "end": v(-75.26, -70.64) * mm});
            skArc(sketch, "E353", {"start": v(-75.26, -70.64) * mm, "mid": v(-75.53, -70.34) * mm, "end": v(-75.75, -70) * mm});
            skArc(sketch, "E354", {"start": v(-75.75, -70) * mm, "mid": v(-75.95, -69.53) * mm, "end": v(-76.09, -69.04) * mm});
            skArc(sketch, "E355", {"start": v(-76.09, -69.04) * mm, "mid": v(-76.17, -68.48) * mm, "end": v(-76.2, -67.92) * mm});
            skArc(sketch, "E356", {"start": v(-76.2, -67.92) * mm, "mid": v(-76.28, -67.14) * mm, "end": v(-76.51, -66.39) * mm});
            skArc(sketch, "E357", {"start": v(-76.51, -66.39) * mm, "mid": v(-76.86, -65.9) * mm, "end": v(-77.38, -65.58) * mm});
            skArc(sketch, "E358", {"start": v(-77.38, -65.58) * mm, "mid": v(-78.26, -65.38) * mm, "end": v(-79.17, -65.33) * mm});
            skArc(sketch, "E359", {"start": v(-79.17, -65.33) * mm, "mid": v(-81.11, -65.45) * mm, "end": v(-83.06, -65.6) * mm});
            skArc(sketch, "E360", {"start": v(-83.06, -65.6) * mm, "mid": v(-84.51, -65.72) * mm, "end": v(-85.97, -65.78) * mm});
            skArc(sketch, "E361", {"start": v(-85.97, -65.78) * mm, "mid": v(-87.04, -65.76) * mm, "end": v(-88.11, -65.64) * mm});
            skArc(sketch, "E362", {"start": v(-88.11, -65.64) * mm, "mid": v(-88.81, -65.5) * mm, "end": v(-89.48, -65.25) * mm});
            skArc(sketch, "E363", {"start": v(-89.48, -65.25) * mm, "mid": v(-89.8, -64.98) * mm, "end": v(-89.92, -64.58) * mm});
            skArc(sketch, "E364", {"start": v(-89.92, -64.58) * mm, "mid": v(-89.96, -64.29) * mm, "end": v(-90.1, -64.02) * mm});
            skArc(sketch, "E365", {"start": v(-90.1, -64.02) * mm, "mid": v(-90.32, -63.8) * mm, "end": v(-90.59, -63.67) * mm});
            skArc(sketch, "E366", {"start": v(-90.59, -63.67) * mm, "mid": v(-90.95, -63.58) * mm, "end": v(-91.33, -63.58) * mm});
            skArc(sketch, "E367", {"start": v(-91.33, -63.58) * mm, "mid": v(-91.77, -63.66) * mm, "end": v(-92.2, -63.8) * mm});
            skArc(sketch, "E368", {"start": v(-92.2, -63.8) * mm, "mid": v(-92.63, -63.93) * mm, "end": v(-93.08, -64.01) * mm});
            skArc(sketch, "E369", {"start": v(-93.08, -64.01) * mm, "mid": v(-93.45, -64.01) * mm, "end": v(-93.82, -63.94) * mm});
            skArc(sketch, "E370", {"start": v(-93.82, -63.94) * mm, "mid": v(-94.09, -63.8) * mm, "end": v(-94.3, -63.59) * mm});
            skArc(sketch, "E371", {"start": v(-94.3, -63.59) * mm, "mid": v(-94.44, -63.33) * mm, "end": v(-94.49, -63.04) * mm});
            skArc(sketch, "E372", {"start": v(-94.49, -63.04) * mm, "mid": v(-94.54, -62.74) * mm, "end": v(-94.67, -62.48) * mm});
            skArc(sketch, "E373", {"start": v(-94.67, -62.48) * mm, "mid": v(-94.9, -62.27) * mm, "end": v(-95.16, -62.14) * mm});
            skArc(sketch, "E374", {"start": v(-95.16, -62.14) * mm, "mid": v(-95.53, -62.06) * mm, "end": v(-95.9, -62.06) * mm});
            skArc(sketch, "E375", {"start": v(-95.9, -62.06) * mm, "mid": v(-96.34, -62.14) * mm, "end": v(-96.77, -62.27) * mm});
            skArc(sketch, "E376", {"start": v(-96.77, -62.27) * mm, "mid": v(-97.2, -62.4) * mm, "end": v(-97.65, -62.49) * mm});
            skArc(sketch, "E377", {"start": v(-97.65, -62.49) * mm, "mid": v(-98.02, -62.49) * mm, "end": v(-98.39, -62.4) * mm});
            skArc(sketch, "E378", {"start": v(-98.39, -62.4) * mm, "mid": v(-98.66, -62.26) * mm, "end": v(-98.87, -62.05) * mm});
            skArc(sketch, "E379", {"start": v(-98.87, -62.05) * mm, "mid": v(-99.01, -61.78) * mm, "end": v(-99.06, -61.49) * mm});
            skArc(sketch, "E380", {"start": v(-99.06, -61.49) * mm, "mid": v(-99.1, -61.16) * mm, "end": v(-99.18, -60.84) * mm});
            skArc(sketch, "E381", {"start": v(-99.18, -60.84) * mm, "mid": v(-99.31, -60.67) * mm, "end": v(-99.52, -60.6) * mm});
            skArc(sketch, "E382", {"start": v(-99.52, -60.6) * mm, "mid": v(-99.81, -60.63) * mm, "end": v(-100.08, -60.76) * mm});
            skArc(sketch, "E383", {"start": v(-100.08, -60.76) * mm, "mid": v(-100.54, -61.07) * mm, "end": v(-100.97, -61.4) * mm});
            skArc(sketch, "E384", {"start": v(-100.97, -61.4) * mm, "mid": v(-101.46, -61.75) * mm, "end": v(-102, -62) * mm});
            skArc(sketch, "E385", {"start": v(-102, -62) * mm, "mid": v(-102.53, -62.13) * mm, "end": v(-103.08, -62.14) * mm});
            skArc(sketch, "E386", {"start": v(-103.08, -62.14) * mm, "mid": v(-103.69, -62.03) * mm, "end": v(-104.27, -61.8) * mm});
            skArc(sketch, "E387", {"start": v(-104.27, -61.8) * mm, "mid": v(-104.97, -61.42) * mm, "end": v(-105.63, -60.98) * mm});
            skArc(sketch, "E388", {"start": v(-105.63, -60.98) * mm, "mid": v(-106.48, -60.26) * mm, "end": v(-107.2, -59.43) * mm});
            skArc(sketch, "E389", {"start": v(-107.2, -59.43) * mm, "mid": v(-107.36, -58.87) * mm, "end": v(-107.08, -58.36) * mm});
            skArc(sketch, "E390", {"start": v(-107.08, -58.36) * mm, "mid": v(-106.32, -57.95) * mm, "end": v(-105.47, -57.83) * mm});
            skArc(sketch, "E391", {"start": v(-105.47, -57.83) * mm, "mid": v(-103.79, -57.94) * mm, "end": v(-102.1, -58.14) * mm});
            skArc(sketch, "E392", {"start": v(-102.1, -58.14) * mm, "mid": v(-100.68, -58.3) * mm, "end": v(-99.24, -58.38) * mm});
            skArc(sketch, "E393", {"start": v(-99.24, -58.38) * mm, "mid": v(-90.82, -58.54) * mm, "end": v(-82.4, -58.69) * mm});
            skArc(sketch, "E394", {"start": v(-82.4, -58.69) * mm, "mid": v(-72.63, -58.84) * mm, "end": v(-62.86, -58.97) * mm});
            skArc(sketch, "E395", {"start": v(-62.86, -58.97) * mm, "mid": v(-51.62, -59.1) * mm, "end": v(-40.39, -59.2) * mm});
            skArc(sketch, "E396", {"start": v(-40.39, -59.2) * mm, "mid": v(-13.83, -59.43) * mm, "end": v(12.73, -59.68) * mm});
            skArc(sketch, "E397", {"start": v(12.73, -59.68) * mm, "mid": v(20.34, -59.8) * mm, "end": v(27.96, -60.04) * mm});
            skArc(sketch, "E398", {"start": v(27.96, -60.04) * mm, "mid": v(31.42, -60.26) * mm, "end": v(34.86, -60.65) * mm});
            skArc(sketch, "E399", {"start": v(34.86, -60.65) * mm, "mid": v(35.53, -61.2) * mm, "end": v(35.33, -62.05) * mm});
            skArc(sketch, "E400", {"start": v(35.33, -62.05) * mm, "mid": v(34.8, -62.48) * mm, "end": v(34.2, -62.8) * mm});
            skArc(sketch, "E401", {"start": v(34.2, -62.8) * mm, "mid": v(33.17, -63.16) * mm, "end": v(32.13, -63.47) * mm});
            skArc(sketch, "E402", {"start": v(32.13, -63.47) * mm, "mid": v(30.89, -63.76) * mm, "end": v(29.63, -64) * mm});
            skArc(sketch, "E403", {"start": v(29.63, -64) * mm, "mid": v(28.33, -64.17) * mm, "end": v(27.03, -64.27) * mm});
            skArc(sketch, "E404", {"start": v(27.03, -64.27) * mm, "mid": v(24.67, -64.43) * mm, "end": v(22.32, -64.63) * mm});
            skArc(sketch, "E405", {"start": v(22.32, -64.63) * mm, "mid": v(19.78, -64.9) * mm, "end": v(17.24, -65.2) * mm});
            skArc(sketch, "E406", {"start": v(17.24, -65.2) * mm, "mid": v(14.95, -65.51) * mm, "end": v(12.67, -65.85) * mm});
            skArc(sketch, "E407", {"start": v(12.67, -65.85) * mm, "mid": v(11.65, -66.06) * mm, "end": v(10.67, -66.37) * mm});
            skArc(sketch, "E408", {"start": v(10.67, -66.37) * mm, "mid": v(10.48, -66.43) * mm, "end": v(10.3, -66.47) * mm});
            skArc(sketch, "E409", {"start": v(10.3, -66.47) * mm, "mid": v(10.04, -66.5) * mm, "end": v(9.78, -66.51) * mm});
            skArc(sketch, "E410", {"start": v(9.78, -66.51) * mm, "mid": v(9.5, -66.52) * mm, "end": v(9.23, -66.51) * mm});
            skArc(sketch, "E411", {"start": v(9.23, -66.51) * mm, "mid": v(8.97, -66.5) * mm, "end": v(8.72, -66.46) * mm});
            skArc(sketch, "E412", {"start": v(8.72, -66.46) * mm, "mid": v(7.65, -66.44) * mm, "end": v(6.62, -66.75) * mm});
            skArc(sketch, "E413", {"start": v(6.62, -66.75) * mm, "mid": v(4.7, -67.7) * mm, "end": v(2.82, -68.74) * mm});
            skArc(sketch, "E414", {"start": v(2.82, -68.74) * mm, "mid": v(0.99, -69.85) * mm, "end": v(-0.8, -71.04) * mm});
            skArc(sketch, "E415", {"start": v(-0.8, -71.04) * mm, "mid": v(-1.33, -71.64) * mm, "end": v(-1.52, -72.43) * mm});
            skArc(sketch, "E416", {"start": v(-1.52, -72.43) * mm, "mid": v(-1.47, -72.73) * mm, "end": v(-1.32, -73) * mm});
            skArc(sketch, "E417", {"start": v(-1.32, -73) * mm, "mid": v(-1.05, -73.28) * mm, "end": v(-0.74, -73.5) * mm});
            skArc(sketch, "E418", {"start": v(-0.74, -73.5) * mm, "mid": v(-0.32, -73.72) * mm, "end": v(0.12, -73.87) * mm});
            skArc(sketch, "E419", {"start": v(0.12, -73.87) * mm, "mid": v(0.63, -73.97) * mm, "end": v(1.14, -74.01) * mm});
            skArc(sketch, "E420", {"start": v(1.14, -74.01) * mm, "mid": v(2.14, -74.05) * mm, "end": v(3.14, -74.07) * mm});
            skArc(sketch, "E421", {"start": v(3.14, -74.07) * mm, "mid": v(8.79, -74.18) * mm, "end": v(14.44, -74.29) * mm});
            skArc(sketch, "E422", {"start": v(14.44, -74.29) * mm, "mid": v(21.01, -74.41) * mm, "end": v(27.59, -74.53) * mm});
            skArc(sketch, "E423", {"start": v(27.59, -74.53) * mm, "mid": v(35.13, -74.67) * mm, "end": v(42.67, -74.8) * mm});
            skArc(sketch, "E424", {"start": v(42.67, -74.8) * mm, "mid": v(50.2, -74.96) * mm, "end": v(57.73, -75.14) * mm});
            skArc(sketch, "E425", {"start": v(57.73, -75.14) * mm, "mid": v(64.26, -75.33) * mm, "end": v(70.79, -75.57) * mm});
            skArc(sketch, "E426", {"start": v(70.79, -75.57) * mm, "mid": v(76.41, -75.8) * mm, "end": v(82.03, -76.03) * mm});
            skArc(sketch, "E427", {"start": v(82.03, -76.03) * mm, "mid": v(82.94, -76.15) * mm, "end": v(83.82, -76.42) * mm});
            skArc(sketch, "E428", {"start": v(83.82, -76.42) * mm, "mid": v(84.2, -76.88) * mm, "end": v(84, -77.45) * mm});
            skArc(sketch, "E429", {"start": v(84, -77.45) * mm, "mid": v(83.03, -78.11) * mm, "end": v(81.94, -78.55) * mm});
            skArc(sketch, "E430", {"start": v(81.94, -78.55) * mm, "mid": v(79.85, -79.04) * mm, "end": v(77.73, -79.33) * mm});
            skArc(sketch, "E431", {"start": v(77.73, -79.33) * mm, "mid": v(75.65, -79.4) * mm, "end": v(73.57, -79.29) * mm});
            skArc(sketch, "E432", {"start": v(73.57, -79.29) * mm, "mid": v(72.51, -79.23) * mm, "end": v(71.46, -79.31) * mm});
            skArc(sketch, "E433", {"start": v(71.46, -79.31) * mm, "mid": v(70.5, -79.52) * mm, "end": v(69.57, -79.87) * mm});
            skArc(sketch, "E434", {"start": v(69.57, -79.87) * mm, "mid": v(68.63, -80.39) * mm, "end": v(67.78, -81.02) * mm});
            skArc(sketch, "E435", {"start": v(67.78, -81.02) * mm, "mid": v(66.83, -81.9) * mm, "end": v(65.95, -82.85) * mm});
            skArc(sketch, "E436", {"start": v(65.95, -82.85) * mm, "mid": v(65.3, -83.57) * mm, "end": v(64.62, -84.26) * mm});
            skArc(sketch, "E437", {"start": v(64.62, -84.26) * mm, "mid": v(64.08, -84.73) * mm, "end": v(63.5, -85.13) * mm});
            skArc(sketch, "E438", {"start": v(63.5, -85.13) * mm, "mid": v(63.17, -85.27) * mm, "end": v(62.8, -85.3) * mm});
            skArc(sketch, "E439", {"start": v(62.8, -85.3) * mm, "mid": v(62.58, -85.2) * mm, "end": v(62.49, -84.96) * mm});
            skArc(sketch, "E440", {"start": v(62.49, -84.96) * mm, "mid": v(62.4, -84.57) * mm, "end": v(62.2, -84.24) * mm});
            skArc(sketch, "E441", {"start": v(62.2, -84.24) * mm, "mid": v(61.8, -83.89) * mm, "end": v(61.35, -83.62) * mm});
            skArc(sketch, "E442", {"start": v(61.35, -83.62) * mm, "mid": v(60.73, -83.37) * mm, "end": v(60.1, -83.2) * mm});
            skArc(sketch, "E443", {"start": v(60.1, -83.2) * mm, "mid": v(59.35, -83.1) * mm, "end": v(58.6, -83.06) * mm});
            skArc(sketch, "E444", {"start": v(58.6, -83.06) * mm, "mid": v(57.85, -83.1) * mm, "end": v(57.1, -83.2) * mm});
            skArc(sketch, "E445", {"start": v(57.1, -83.2) * mm, "mid": v(56.49, -83.35) * mm, "end": v(55.9, -83.6) * mm});
            skArc(sketch, "E446", {"start": v(55.9, -83.6) * mm, "mid": v(55.5, -83.87) * mm, "end": v(55.18, -84.22) * mm});
            skArc(sketch, "E447", {"start": v(55.18, -84.22) * mm, "mid": v(55, -84.57) * mm, "end": v(54.98, -84.96) * mm});
            skArc(sketch, "E448", {"start": v(54.98, -84.96) * mm, "mid": v(55.1, -86.24) * mm, "end": v(55.16, -87.52) * mm});
            skArc(sketch, "E449", {"start": v(55.16, -87.52) * mm, "mid": v(55.1, -88.39) * mm, "end": v(54.9, -89.24) * mm});
            skArc(sketch, "E450", {"start": v(54.9, -89.24) * mm, "mid": v(54.65, -89.67) * mm, "end": v(54.25, -89.97) * mm});
            skArc(sketch, "E451", {"start": v(54.25, -89.97) * mm, "mid": v(53.79, -90.06) * mm, "end": v(53.34, -89.92) * mm});
            skArc(sketch, "E452", {"start": v(53.34, -89.92) * mm, "mid": v(53.06, -89.8) * mm, "end": v(52.76, -89.74) * mm});
            skArc(sketch, "E453", {"start": v(52.76, -89.74) * mm, "mid": v(52.5, -89.78) * mm, "end": v(52.26, -89.92) * mm});
            skArc(sketch, "E454", {"start": v(52.26, -89.92) * mm, "mid": v(52.06, -90.16) * mm, "end": v(51.93, -90.45) * mm});
            skArc(sketch, "E455", {"start": v(51.93, -90.45) * mm, "mid": v(51.84, -90.84) * mm, "end": v(51.82, -91.25) * mm});
            skArc(sketch, "E456", {"start": v(51.82, -91.25) * mm, "mid": v(51.74, -91.75) * mm, "end": v(51.51, -92.2) * mm});
            skArc(sketch, "E457", {"start": v(51.51, -92.2) * mm, "mid": v(51.12, -92.65) * mm, "end": v(50.65, -93.03) * mm});
            skArc(sketch, "E458", {"start": v(50.65, -93.03) * mm, "mid": v(50, -93.39) * mm, "end": v(49.31, -93.65) * mm});
            skArc(sketch, "E459", {"start": v(49.31, -93.65) * mm, "mid": v(48.48, -93.87) * mm, "end": v(47.62, -94) * mm});
            skArc(sketch, "E460", {"start": v(47.62, -94) * mm, "mid": v(46.75, -94.14) * mm, "end": v(45.88, -94.35) * mm});
            skArc(sketch, "E461", {"start": v(45.88, -94.35) * mm, "mid": v(45.24, -94.58) * mm, "end": v(44.66, -94.93) * mm});
            skArc(sketch, "E462", {"start": v(44.66, -94.93) * mm, "mid": v(44.28, -95.27) * mm, "end": v(44, -95.7) * mm});
            skArc(sketch, "E463", {"start": v(44, -95.7) * mm, "mid": v(43.87, -96.16) * mm, "end": v(43.9, -96.63) * mm});
            skArc(sketch, "E464", {"start": v(43.9, -96.63) * mm, "mid": v(43.96, -97.08) * mm, "end": v(43.95, -97.53) * mm});
            skArc(sketch, "E465", {"start": v(43.95, -97.53) * mm, "mid": v(43.87, -98) * mm, "end": v(43.73, -98.45) * mm});
            skArc(sketch, "E466", {"start": v(43.73, -98.45) * mm, "mid": v(43.54, -98.87) * mm, "end": v(43.29, -99.26) * mm});
            skArc(sketch, "E467", {"start": v(43.29, -99.26) * mm, "mid": v(43, -99.57) * mm, "end": v(42.68, -99.82) * mm});
            skArc(sketch, "E468", {"start": v(42.68, -99.82) * mm, "mid": v(42.58, -100.08) * mm, "end": v(42.8, -100.26) * mm});
            skArc(sketch, "E469", {"start": v(42.8, -100.26) * mm, "mid": v(48.59, -100.56) * mm, "end": v(54.39, -100.85) * mm});
            skArc(sketch, "E470", {"start": v(54.39, -100.85) * mm, "mid": v(61.28, -101.15) * mm, "end": v(68.18, -101.4) * mm});
            skArc(sketch, "E471", {"start": v(68.18, -101.4) * mm, "mid": v(76.53, -101.65) * mm, "end": v(84.9, -101.86) * mm});
            skArc(sketch, "E472", {"start": v(84.9, -101.86) * mm, "mid": v(94.97, -102.12) * mm, "end": v(105.06, -102.45) * mm});
            skArc(sketch, "E473", {"start": v(105.06, -102.45) * mm, "mid": v(112.83, -102.77) * mm, "end": v(120.6, -103.19) * mm});
            skArc(sketch, "E474", {"start": v(120.6, -103.19) * mm, "mid": v(126.46, -103.59) * mm, "end": v(132.3, -104.07) * mm});
            skArc(sketch, "E475", {"start": v(132.3, -104.07) * mm, "mid": v(135.9, -104.5) * mm, "end": v(139.45, -105.16) * mm});
            skArc(sketch, "E476", {"start": v(139.45, -105.16) * mm, "mid": v(141.67, -105.61) * mm, "end": v(143.9, -106.03) * mm});
            skArc(sketch, "E477", {"start": v(143.9, -106.03) * mm, "mid": v(146.16, -106.42) * mm, "end": v(148.43, -106.77) * mm});
            skArc(sketch, "E478", {"start": v(148.43, -106.77) * mm, "mid": v(150.45, -107.05) * mm, "end": v(152.46, -107.3) * mm});
            skArc(sketch, "E479", {"start": v(152.46, -107.3) * mm, "mid": v(153.76, -107.4) * mm, "end": v(155.07, -107.44) * mm});
            skLineSegment(sketch, "E480", {"start": v(155.07, -107.44) * mm, "end": v(160.02, -107.44) * mm});
            skLineSegment(sketch, "E481", {"start": v(160.02, -107.44) * mm, "end": v(159.91, -14.1) * mm});
            skArc(sketch, "E482", {"start": v(159.91, -14.1) * mm, "mid": v(159.87, 3.7) * mm, "end": v(159.79, 21.5) * mm});
            skArc(sketch, "E483", {"start": v(159.79, 21.5) * mm, "mid": v(159.67, 36.21) * mm, "end": v(159.48, 50.93) * mm});
            skArc(sketch, "E484", {"start": v(159.48, 50.93) * mm, "mid": v(159.3, 63.52) * mm, "end": v(159.1, 76.11) * mm});
            skArc(sketch, "E485", {"start": v(159.1, 76.11) * mm, "mid": v(158.88, 76.36) * mm, "end": v(158.6, 76.2) * mm});
            skArc(sketch, "E486", {"start": v(158.6, 76.2) * mm, "mid": v(158.35, 75.43) * mm, "end": v(158.19, 74.65) * mm});
            skArc(sketch, "E487", {"start": v(158.19, 74.65) * mm, "mid": v(158.05, 73.53) * mm, "end": v(157.96, 72.4) * mm});
            skArc(sketch, "E488", {"start": v(157.96, 72.4) * mm, "mid": v(157.92, 71.17) * mm, "end": v(157.93, 69.94) * mm});
            skArc(sketch, "E489", {"start": v(157.93, 69.94) * mm, "mid": v(158, 68.75) * mm, "end": v(158.13, 67.58) * mm});
            skArc(sketch, "E490", {"start": v(158.13, 67.58) * mm, "mid": v(158.25, 66.26) * mm, "end": v(158.26, 64.93) * mm});
            skArc(sketch, "E491", {"start": v(158.26, 64.93) * mm, "mid": v(158.18, 63.54) * mm, "end": v(158, 62.16) * mm});
            skArc(sketch, "E492", {"start": v(158, 62.16) * mm, "mid": v(157.72, 60.8) * mm, "end": v(157.35, 59.46) * mm});
            skArc(sketch, "E493", {"start": v(157.35, 59.46) * mm, "mid": v(156.91, 58.22) * mm, "end": v(156.37, 57.01) * mm});
            skArc(sketch, "E494", {"start": v(156.37, 57.01) * mm, "mid": v(155.84, 55.88) * mm, "end": v(155.35, 54.73) * mm});
            skArc(sketch, "E495", {"start": v(155.35, 54.73) * mm, "mid": v(155.07, 53.88) * mm, "end": v(154.9, 53) * mm});
            skArc(sketch, "E496", {"start": v(154.9, 53) * mm, "mid": v(154.86, 52.4) * mm, "end": v(154.95, 51.78) * mm});
            skArc(sketch, "E497", {"start": v(154.95, 51.78) * mm, "mid": v(155.15, 51.35) * mm, "end": v(155.5, 51.02) * mm});
            skArc(sketch, "E498", {"start": v(155.5, 51.02) * mm, "mid": v(155.86, 50.7) * mm, "end": v(156.1, 50.3) * mm});
            skArc(sketch, "E499", {"start": v(156.1, 50.3) * mm, "mid": v(156.25, 49.78) * mm, "end": v(156.28, 49.25) * mm});
            skArc(sketch, "E500", {"start": v(156.28, 49.25) * mm, "mid": v(156.18, 48.5) * mm, "end": v(156, 47.77) * mm});
            skArc(sketch, "E501", {"start": v(156, 47.77) * mm, "mid": v(155.62, 46.78) * mm, "end": v(155.2, 45.8) * mm});
            skArc(sketch, "E502", {"start": v(155.2, 45.8) * mm, "mid": v(154.7, 44.62) * mm, "end": v(154.25, 43.42) * mm});
            skArc(sketch, "E503", {"start": v(154.25, 43.42) * mm, "mid": v(154.09, 42.72) * mm, "end": v(154.08, 42) * mm});
            skArc(sketch, "E504", {"start": v(154.08, 42) * mm, "mid": v(154.23, 41.4) * mm, "end": v(154.56, 40.88) * mm});
            skArc(sketch, "E505", {"start": v(154.56, 40.88) * mm, "mid": v(155.16, 40.26) * mm, "end": v(155.83, 39.71) * mm});
            skArc(sketch, "E506", {"start": v(155.83, 39.71) * mm, "mid": v(156.53, 39.16) * mm, "end": v(157.19, 38.54) * mm});
            skArc(sketch, "E507", {"start": v(157.19, 38.54) * mm, "mid": v(157.48, 38.12) * mm, "end": v(157.6, 37.62) * mm});
            skArc(sketch, "E508", {"start": v(157.6, 37.62) * mm, "mid": v(157.54, 37.04) * mm, "end": v(157.32, 36.51) * mm});
            skArc(sketch, "E509", {"start": v(157.32, 36.51) * mm, "mid": v(156.71, 35.52) * mm, "end": v(156.07, 34.55) * mm});
            skArc(sketch, "E510", {"start": v(156.07, 34.55) * mm, "mid": v(155.4, 33.57) * mm, "end": v(154.74, 32.57) * mm});
            skArc(sketch, "E511", {"start": v(154.74, 32.57) * mm, "mid": v(154.57, 32.2) * mm, "end": v(154.52, 31.78) * mm});
            skArc(sketch, "E512", {"start": v(154.52, 31.78) * mm, "mid": v(154.62, 31.5) * mm, "end": v(154.87, 31.36) * mm});
            skArc(sketch, "E513", {"start": v(154.87, 31.36) * mm, "mid": v(155.5, 31.27) * mm, "end": v(156.12, 31.24) * mm});
            skArc(sketch, "E514", {"start": v(156.12, 31.24) * mm, "mid": v(156.97, 31.18) * mm, "end": v(157.81, 31.01) * mm});
            skArc(sketch, "E515", {"start": v(157.81, 31.01) * mm, "mid": v(158.2, 30.75) * mm, "end": v(158.34, 30.3) * mm});
            skArc(sketch, "E516", {"start": v(158.34, 30.3) * mm, "mid": v(158.24, 29.6) * mm, "end": v(157.96, 28.94) * mm});
            skArc(sketch, "E517", {"start": v(157.96, 28.94) * mm, "mid": v(157.01, 27.39) * mm, "end": v(156.03, 25.85) * mm});
            skArc(sketch, "E518", {"start": v(156.03, 25.85) * mm, "mid": v(155.48, 25.1) * mm, "end": v(154.84, 24.4) * mm});
            skArc(sketch, "E519", {"start": v(154.84, 24.4) * mm, "mid": v(154.12, 23.77) * mm, "end": v(153.34, 23.2) * mm});
            skArc(sketch, "E520", {"start": v(153.34, 23.2) * mm, "mid": v(152.57, 22.76) * mm, "end": v(151.76, 22.4) * mm});
            skArc(sketch, "E521", {"start": v(151.76, 22.4) * mm, "mid": v(151.05, 22.2) * mm, "end": v(150.32, 22.15) * mm});
            skArc(sketch, "E522", {"start": v(150.32, 22.15) * mm, "mid": v(149.25, 22.18) * mm, "end": v(148.17, 22.21) * mm});
            skArc(sketch, "E523", {"start": v(148.17, 22.21) * mm, "mid": v(148.02, 22.3) * mm, "end": v(147.97, 22.46) * mm});
            skArc(sketch, "E524", {"start": v(147.97, 22.46) * mm, "mid": v(148.05, 22.67) * mm, "end": v(148.21, 22.82) * mm});
            skArc(sketch, "E525", {"start": v(148.21, 22.82) * mm, "mid": v(149.4, 23.5) * mm, "end": v(150.6, 24.17) * mm});
            skLineSegment(sketch, "E526", {"start": v(150.6, 24.17) * mm, "end": v(154.13, 26.13) * mm});
            skLineSegment(sketch, "E527", {"start": v(154.13, 26.13) * mm, "end": v(149.66, 30.92) * mm});
            skArc(sketch, "E528", {"start": v(149.66, 30.92) * mm, "mid": v(148.18, 32.56) * mm, "end": v(146.76, 34.25) * mm});
            skArc(sketch, "E529", {"start": v(146.76, 34.25) * mm, "mid": v(146.3, 35.08) * mm, "end": v(146.13, 36) * mm});
            skArc(sketch, "E530", {"start": v(146.13, 36) * mm, "mid": v(146.35, 36.66) * mm, "end": v(146.93, 37.03) * mm});
            skArc(sketch, "E531", {"start": v(146.93, 37.03) * mm, "mid": v(148.26, 37.26) * mm, "end": v(149.6, 37.34) * mm});
            skArc(sketch, "E532", {"start": v(149.6, 37.34) * mm, "mid": v(150.85, 37.66) * mm, "end": v(151.8, 38.54) * mm});
            skArc(sketch, "E533", {"start": v(151.8, 38.54) * mm, "mid": v(152.26, 39.82) * mm, "end": v(152.15, 41.17) * mm});
            skArc(sketch, "E534", {"start": v(152.15, 41.17) * mm, "mid": v(151.36, 42.92) * mm, "end": v(150.16, 44.42) * mm});
            skArc(sketch, "E535", {"start": v(150.16, 44.42) * mm, "mid": v(148.56, 45.69) * mm, "end": v(146.73, 46.6) * mm});
            skArc(sketch, "E536", {"start": v(146.73, 46.6) * mm, "mid": v(145.48, 47.22) * mm, "end": v(144.36, 48.05) * mm});
            skArc(sketch, "E537", {"start": v(144.36, 48.05) * mm, "mid": v(143.82, 48.86) * mm, "end": v(143.74, 49.83) * mm});
            skArc(sketch, "E538", {"start": v(143.74, 49.83) * mm, "mid": v(144.13, 50.77) * mm, "end": v(144.9, 51.43) * mm});
            skArc(sketch, "E539", {"start": v(144.9, 51.43) * mm, "mid": v(146.26, 51.99) * mm, "end": v(147.7, 52.32) * mm});
            skArc(sketch, "E540", {"start": v(147.7, 52.32) * mm, "mid": v(148.75, 52.5) * mm, "end": v(149.8, 52.7) * mm});
            skArc(sketch, "E541", {"start": v(149.8, 52.7) * mm, "mid": v(150.1, 52.86) * mm, "end": v(150.27, 53.16) * mm});
            skArc(sketch, "E542", {"start": v(150.27, 53.16) * mm, "mid": v(150.27, 53.54) * mm, "end": v(150.1, 53.87) * mm});
            skArc(sketch, "E543", {"start": v(150.1, 53.87) * mm, "mid": v(149.3, 54.82) * mm, "end": v(148.48, 55.75) * mm});
            skArc(sketch, "E544", {"start": v(148.48, 55.75) * mm, "mid": v(147.9, 56.33) * mm, "end": v(147.3, 56.87) * mm});
            skArc(sketch, "E545", {"start": v(147.3, 56.87) * mm, "mid": v(146.63, 57.37) * mm, "end": v(145.94, 57.81) * mm});
            skArc(sketch, "E546", {"start": v(145.94, 57.81) * mm, "mid": v(145.29, 58.17) * mm, "end": v(144.6, 58.47) * mm});
            skArc(sketch, "E547", {"start": v(144.6, 58.47) * mm, "mid": v(144.09, 58.62) * mm, "end": v(143.55, 58.67) * mm});
            skArc(sketch, "E548", {"start": v(143.55, 58.67) * mm, "mid": v(143.03, 58.71) * mm, "end": v(142.52, 58.82) * mm});
            skArc(sketch, "E549", {"start": v(142.52, 58.82) * mm, "mid": v(142.3, 59) * mm, "end": v(142.24, 59.27) * mm});
            skArc(sketch, "E550", {"start": v(142.24, 59.27) * mm, "mid": v(142.37, 59.7) * mm, "end": v(142.6, 60.08) * mm});
            skArc(sketch, "E551", {"start": v(142.6, 60.08) * mm, "mid": v(143.31, 60.92) * mm, "end": v(144.04, 61.75) * mm});
            skArc(sketch, "E552", {"start": v(144.04, 61.75) * mm, "mid": v(144.9, 62.72) * mm, "end": v(145.72, 63.72) * mm});
            skArc(sketch, "E553", {"start": v(145.72, 63.72) * mm, "mid": v(145.97, 64.17) * mm, "end": v(146.06, 64.68) * mm});
            skArc(sketch, "E554", {"start": v(146.06, 64.68) * mm, "mid": v(145.96, 65.14) * mm, "end": v(145.68, 65.53) * mm});
            skArc(sketch, "E555", {"start": v(145.68, 65.53) * mm, "mid": v(144.86, 66.22) * mm, "end": v(144.02, 66.87) * mm});
            skArc(sketch, "E556", {"start": v(144.02, 66.87) * mm, "mid": v(142.97, 67.86) * mm, "end": v(142.22, 69.1) * mm});
            skArc(sketch, "E557", {"start": v(142.22, 69.1) * mm, "mid": v(141.56, 70.87) * mm, "end": v(141.13, 72.7) * mm});
            skArc(sketch, "E558", {"start": v(141.13, 72.7) * mm, "mid": v(140.97, 74.29) * mm, "end": v(141.04, 75.89) * mm});
            skArc(sketch, "E559", {"start": v(141.04, 75.89) * mm, "mid": v(141.44, 76.65) * mm, "end": v(142.25, 76.96) * mm});
            skArc(sketch, "E560", {"start": v(142.25, 76.96) * mm, "mid": v(142.45, 77.02) * mm, "end": v(142.6, 77.17) * mm});
            skArc(sketch, "E561", {"start": v(142.6, 77.17) * mm, "mid": v(142.68, 77.4) * mm, "end": v(142.67, 77.63) * mm});
            skArc(sketch, "E562", {"start": v(142.67, 77.63) * mm, "mid": v(142.55, 78.01) * mm, "end": v(142.36, 78.37) * mm});
            skArc(sketch, "E563", {"start": v(142.36, 78.37) * mm, "mid": v(142.06, 78.82) * mm, "end": v(141.73, 79.25) * mm});
            skArc(sketch, "E564", {"start": v(141.73, 79.25) * mm, "mid": v(141.4, 79.68) * mm, "end": v(141.08, 80.13) * mm});
            skArc(sketch, "E565", {"start": v(141.08, 80.13) * mm, "mid": v(140.88, 80.48) * mm, "end": v(140.73, 80.86) * mm});
            skArc(sketch, "E566", {"start": v(140.73, 80.86) * mm, "mid": v(140.68, 81.1) * mm, "end": v(140.7, 81.33) * mm});
            skArc(sketch, "E567", {"start": v(140.7, 81.33) * mm, "mid": v(140.8, 81.48) * mm, "end": v(140.97, 81.53) * mm});
            skArc(sketch, "E568", {"start": v(140.97, 81.53) * mm, "mid": v(141.13, 81.6) * mm, "end": v(141.23, 81.74) * mm});
            skArc(sketch, "E569", {"start": v(141.23, 81.74) * mm, "mid": v(141.26, 81.97) * mm, "end": v(141.21, 82.2) * mm});
            skArc(sketch, "E570", {"start": v(141.21, 82.2) * mm, "mid": v(141.06, 82.59) * mm, "end": v(140.86, 82.94) * mm});
            skArc(sketch, "E571", {"start": v(140.86, 82.94) * mm, "mid": v(140.55, 83.39) * mm, "end": v(140.2, 83.82) * mm});
            skArc(sketch, "E572", {"start": v(140.2, 83.82) * mm, "mid": v(139.73, 84.42) * mm, "end": v(139.27, 85.03) * mm});
            skArc(sketch, "E573", {"start": v(139.27, 85.03) * mm, "mid": v(139.12, 85.32) * mm, "end": v(139.07, 85.65) * mm});
            skArc(sketch, "E574", {"start": v(139.07, 85.65) * mm, "mid": v(139.15, 85.87) * mm, "end": v(139.34, 86) * mm});
            skArc(sketch, "E575", {"start": v(139.34, 86) * mm, "mid": v(139.77, 86.08) * mm, "end": v(140.2, 86.1) * mm});
            skArc(sketch, "E576", {"start": v(140.2, 86.1) * mm, "mid": v(140.62, 86.14) * mm, "end": v(141.03, 86.23) * mm});
            skArc(sketch, "E577", {"start": v(141.03, 86.23) * mm, "mid": v(141.22, 86.38) * mm, "end": v(141.3, 86.6) * mm});
            skArc(sketch, "E578", {"start": v(141.3, 86.6) * mm, "mid": v(141.23, 86.96) * mm, "end": v(141.06, 87.27) * mm});
            skArc(sketch, "E579", {"start": v(141.06, 87.27) * mm, "mid": v(140.6, 87.9) * mm, "end": v(140.11, 88.5) * mm});
            skArc(sketch, "E580", {"start": v(140.11, 88.5) * mm, "mid": v(139.6, 89.16) * mm, "end": v(139.14, 89.84) * mm});
            skArc(sketch, "E581", {"start": v(139.14, 89.84) * mm, "mid": v(138.96, 90.26) * mm, "end": v(138.9, 90.72) * mm});
            skArc(sketch, "E582", {"start": v(138.9, 90.72) * mm, "mid": v(139, 91.13) * mm, "end": v(139.25, 91.47) * mm});
            skArc(sketch, "E583", {"start": v(139.25, 91.47) * mm, "mid": v(139.76, 91.9) * mm, "end": v(140.3, 92.3) * mm});
            skArc(sketch, "E584", {"start": v(140.3, 92.3) * mm, "mid": v(140.79, 92.61) * mm, "end": v(141.26, 92.95) * mm});
            skArc(sketch, "E585", {"start": v(141.26, 92.95) * mm, "mid": v(141.42, 93.13) * mm, "end": v(141.51, 93.35) * mm});
            skArc(sketch, "E586", {"start": v(141.51, 93.35) * mm, "mid": v(141.48, 93.52) * mm, "end": v(141.34, 93.62) * mm});
            skArc(sketch, "E587", {"start": v(141.34, 93.62) * mm, "mid": v(140.97, 93.68) * mm, "end": v(140.59, 93.7) * mm});
            skArc(sketch, "E588", {"start": v(140.59, 93.7) * mm, "mid": v(140.12, 93.83) * mm, "end": v(139.77, 94.15) * mm});
            skArc(sketch, "E589", {"start": v(139.77, 94.15) * mm, "mid": v(139.42, 94.8) * mm, "end": v(139.17, 95.48) * mm});
            skArc(sketch, "E590", {"start": v(139.17, 95.48) * mm, "mid": v(138.93, 96.53) * mm, "end": v(138.8, 97.61) * mm});
            skArc(sketch, "E591", {"start": v(138.8, 97.61) * mm, "mid": v(138.71, 99.1) * mm, "end": v(138.68, 100.58) * mm});
            skArc(sketch, "E592", {"start": v(138.68, 100.58) * mm, "mid": v(138.66, 101.9) * mm, "end": v(138.6, 103.21) * mm});
            skArc(sketch, "E593", {"start": v(138.6, 103.21) * mm, "mid": v(138.48, 104.32) * mm, "end": v(138.31, 105.43) * mm});
            skArc(sketch, "E594", {"start": v(138.31, 105.43) * mm, "mid": v(138.13, 106.26) * mm, "end": v(137.91, 107.07) * mm});
            skArc(sketch, "E595", {"start": v(137.91, 107.07) * mm, "mid": v(137.72, 107.34) * mm, "end": v(137.41, 107.44) * mm});
            skArc(sketch, "E596", {"start": v(137.41, 107.44) * mm, "mid": v(137.16, 107.4) * mm, "end": v(136.92, 107.3) * mm});
            skArc(sketch, "E597", {"start": v(136.92, 107.3) * mm, "mid": v(136.68, 107.1) * mm, "end": v(136.48, 106.88) * mm});
            skArc(sketch, "E598", {"start": v(136.48, 106.88) * mm, "mid": v(136.3, 106.59) * mm, "end": v(136.15, 106.27) * mm});
            skArc(sketch, "E599", {"start": v(136.15, 106.27) * mm, "mid": v(136.06, 105.9) * mm, "end": v(136, 105.54) * mm});
            skArc(sketch, "E600", {"start": v(-32.8, 62.1) * mm, "mid": v(-32.6, 61.43) * mm, "end": v(-32.31, 60.8) * mm});
            skArc(sketch, "E601", {"start": v(-32.31, 60.8) * mm, "mid": v(-31.96, 60.21) * mm, "end": v(-31.54, 59.68) * mm});
            skArc(sketch, "E602", {"start": v(-31.54, 59.68) * mm, "mid": v(-31.1, 59.27) * mm, "end": v(-30.62, 58.93) * mm});
            skArc(sketch, "E603", {"start": v(-30.62, 58.93) * mm, "mid": v(-30.17, 58.74) * mm, "end": v(-29.69, 58.67) * mm});
            skArc(sketch, "E604", {"start": v(-29.69, 58.67) * mm, "mid": v(-29.25, 58.65) * mm, "end": v(-28.83, 58.57) * mm});
            skArc(sketch, "E605", {"start": v(-28.83, 58.57) * mm, "mid": v(-28.45, 58.44) * mm, "end": v(-28.1, 58.26) * mm});
            skArc(sketch, "E606", {"start": v(-28.1, 58.26) * mm, "mid": v(-27.83, 58.05) * mm, "end": v(-27.6, 57.8) * mm});
            skArc(sketch, "E607", {"start": v(-27.6, 57.8) * mm, "mid": v(-27.48, 57.54) * mm, "end": v(-27.43, 57.25) * mm});
            skArc(sketch, "E608", {"start": v(-27.43, 57.25) * mm, "mid": v(-27.36, 56.86) * mm, "end": v(-27.16, 56.5) * mm});
            skArc(sketch, "E609", {"start": v(-27.16, 56.5) * mm, "mid": v(-26.6, 55.86) * mm, "end": v(-26, 55.24) * mm});
            skArc(sketch, "E610", {"start": v(-26, 55.24) * mm, "mid": v(-25.24, 54.5) * mm, "end": v(-24.44, 53.8) * mm});
            skArc(sketch, "E611", {"start": v(-24.44, 53.8) * mm, "mid": v(-23.53, 53.08) * mm, "end": v(-22.58, 52.38) * mm});
            skArc(sketch, "E612", {"start": v(-22.58, 52.38) * mm, "mid": v(-21.1, 51.36) * mm, "end": v(-19.59, 50.4) * mm});
            skArc(sketch, "E613", {"start": v(-19.59, 50.4) * mm, "mid": v(-19.21, 50.4) * mm, "end": v(-19.05, 50.74) * mm});
            skArc(sketch, "E614", {"start": v(-19.05, 50.74) * mm, "mid": v(-19.24, 51.52) * mm, "end": v(-19.61, 52.24) * mm});
            skArc(sketch, "E615", {"start": v(-19.61, 52.24) * mm, "mid": v(-21.4, 54.9) * mm, "end": v(-23.21, 57.53) * mm});
            skArc(sketch, "E616", {"start": v(-23.21, 57.53) * mm, "mid": v(-23.75, 58.33) * mm, "end": v(-24.27, 59.14) * mm});
            skArc(sketch, "E617", {"start": v(-24.27, 59.14) * mm, "mid": v(-24.67, 59.8) * mm, "end": v(-25.03, 60.5) * mm});
            skArc(sketch, "E618", {"start": v(-25.03, 60.5) * mm, "mid": v(-25.27, 60.99) * mm, "end": v(-25.48, 61.5) * mm});
            skArc(sketch, "E619", {"start": v(-25.48, 61.5) * mm, "mid": v(-25.46, 61.65) * mm, "end": v(-25.33, 61.72) * mm});
            skArc(sketch, "E620", {"start": v(-25.33, 61.72) * mm, "mid": v(-24.33, 61.53) * mm, "end": v(-23.47, 60.97) * mm});
            skArc(sketch, "E621", {"start": v(-23.47, 60.97) * mm, "mid": v(-21.6, 59.11) * mm, "end": v(-19.79, 57.19) * mm});
            skArc(sketch, "E622", {"start": v(-19.79, 57.19) * mm, "mid": v(-17.96, 55.1) * mm, "end": v(-16.23, 52.92) * mm});
            skArc(sketch, "E623", {"start": v(-16.23, 52.92) * mm, "mid": v(-15, 51.13) * mm, "end": v(-13.93, 49.23) * mm});
            skArc(sketch, "E624", {"start": v(-13.93, 49.23) * mm, "mid": v(-12.34, 46.63) * mm, "end": v(-10.35, 44.33) * mm});
            skArc(sketch, "E625", {"start": v(-10.35, 44.33) * mm, "mid": v(-7.55, 41.82) * mm, "end": v(-4.53, 39.58) * mm});
            skArc(sketch, "E626", {"start": v(-4.53, 39.58) * mm, "mid": v(-2.6, 38.54) * mm, "end": v(-0.5, 37.92) * mm});
            skArc(sketch, "E627", {"start": v(-0.5, 37.92) * mm, "mid": v(0.5, 38.28) * mm, "end": v(0.67, 39.32) * mm});
            skArc(sketch, "E628", {"start": v(0.67, 39.32) * mm, "mid": v(0.42, 39.82) * mm, "end": v(0.08, 40.26) * mm});
            skArc(sketch, "E629", {"start": v(0.08, 40.26) * mm, "mid": v(-0.54, 40.9) * mm, "end": v(-1.2, 41.51) * mm});
            skArc(sketch, "E630", {"start": v(-1.2, 41.51) * mm, "mid": v(-2, 42.18) * mm, "end": v(-2.83, 42.81) * mm});
            skArc(sketch, "E631", {"start": v(-2.83, 42.81) * mm, "mid": v(-3.71, 43.42) * mm, "end": v(-4.62, 43.98) * mm});
            skArc(sketch, "E632", {"start": v(-4.62, 43.98) * mm, "mid": v(-6.02, 44.9) * mm, "end": v(-7.32, 45.95) * mm});
            skArc(sketch, "E633", {"start": v(-7.32, 45.95) * mm, "mid": v(-8.29, 46.97) * mm, "end": v(-9.07, 48.12) * mm});
            skArc(sketch, "E634", {"start": v(-9.07, 48.12) * mm, "mid": v(-9.09, 48.6) * mm, "end": v(-8.7, 48.89) * mm});
            skArc(sketch, "E635", {"start": v(-8.7, 48.89) * mm, "mid": v(-7.95, 48.89) * mm, "end": v(-7.24, 48.63) * mm});
            skArc(sketch, "E636", {"start": v(-7.24, 48.63) * mm, "mid": v(-7.1, 48.6) * mm, "end": v(-6.95, 48.64) * mm});
            skArc(sketch, "E637", {"start": v(-6.95, 48.64) * mm, "mid": v(-6.88, 48.73) * mm, "end": v(-6.9, 48.85) * mm});
            skArc(sketch, "E638", {"start": v(-6.9, 48.85) * mm, "mid": v(-7.21, 49.27) * mm, "end": v(-7.56, 49.67) * mm});
            skArc(sketch, "E639", {"start": v(-7.56, 49.67) * mm, "mid": v(-8.15, 50.28) * mm, "end": v(-8.76, 50.89) * mm});
            skArc(sketch, "E640", {"start": v(-8.76, 50.89) * mm, "mid": v(-9.43, 51.57) * mm, "end": v(-10.08, 52.28) * mm});
            skArc(sketch, "E641", {"start": v(-10.08, 52.28) * mm, "mid": v(-10.65, 52.99) * mm, "end": v(-11.18, 53.72) * mm});
            skArc(sketch, "E642", {"start": v(-11.18, 53.72) * mm, "mid": v(-11.6, 54.35) * mm, "end": v(-11.98, 55) * mm});
            skArc(sketch, "E643", {"start": v(-11.98, 55) * mm, "mid": v(-12.14, 55.4) * mm, "end": v(-12.2, 55.84) * mm});
            skArc(sketch, "E644", {"start": v(-12.2, 55.84) * mm, "mid": v(-11.92, 56.27) * mm, "end": v(-11.41, 56.2) * mm});
            skArc(sketch, "E645", {"start": v(-11.41, 56.2) * mm, "mid": v(-9.43, 54.43) * mm, "end": v(-7.5, 52.6) * mm});
            skArc(sketch, "E646", {"start": v(-7.5, 52.6) * mm, "mid": v(-5.18, 50.27) * mm, "end": v(-2.95, 47.86) * mm});
            skArc(sketch, "E647", {"start": v(-2.95, 47.86) * mm, "mid": v(-0.8, 45.34) * mm, "end": v(1.27, 42.75) * mm});
            skArc(sketch, "E648", {"start": v(1.27, 42.75) * mm, "mid": v(2, 41.85) * mm, "end": v(2.78, 41) * mm});
            skArc(sketch, "E649", {"start": v(2.78, 41) * mm, "mid": v(3.6, 40.2) * mm, "end": v(4.46, 39.47) * mm});
            skArc(sketch, "E650", {"start": v(4.46, 39.47) * mm, "mid": v(5.24, 38.87) * mm, "end": v(6.06, 38.33) * mm});
            skArc(sketch, "E651", {"start": v(6.06, 38.33) * mm, "mid": v(6.64, 38.04) * mm, "end": v(7.27, 37.88) * mm});
            skArc(sketch, "E652", {"start": v(7.27, 37.88) * mm, "mid": v(7.84, 37.76) * mm, "end": v(8.38, 37.56) * mm});
            skArc(sketch, "E653", {"start": v(8.38, 37.56) * mm, "mid": v(9.01, 37.24) * mm, "end": v(9.62, 36.88) * mm});
            skArc(sketch, "E654", {"start": v(9.62, 36.88) * mm, "mid": v(10.21, 36.45) * mm, "end": v(10.77, 35.98) * mm});
            skArc(sketch, "E655", {"start": v(10.77, 35.98) * mm, "mid": v(11.25, 35.5) * mm, "end": v(11.67, 34.98) * mm});
            skArc(sketch, "E656", {"start": v(11.67, 34.98) * mm, "mid": v(12.18, 34.41) * mm, "end": v(12.8, 33.95) * mm});
            skArc(sketch, "E657", {"start": v(12.8, 33.95) * mm, "mid": v(13.62, 33.5) * mm, "end": v(14.5, 33.15) * mm});
            skArc(sketch, "E658", {"start": v(14.5, 33.15) * mm, "mid": v(15.53, 32.84) * mm, "end": v(16.6, 32.63) * mm});
            skArc(sketch, "E659", {"start": v(16.6, 32.63) * mm, "mid": v(17.77, 32.5) * mm, "end": v(18.95, 32.46) * mm});
            skArc(sketch, "E660", {"start": v(18.95, 32.46) * mm, "mid": v(20.03, 32.43) * mm, "end": v(21.1, 32.34) * mm});
            skArc(sketch, "E661", {"start": v(21.1, 32.34) * mm, "mid": v(22.1, 32.2) * mm, "end": v(23.1, 31.98) * mm});
            skArc(sketch, "E662", {"start": v(23.1, 31.98) * mm, "mid": v(23.88, 31.75) * mm, "end": v(24.66, 31.46) * mm});
            skArc(sketch, "E663", {"start": v(24.66, 31.46) * mm, "mid": v(25.08, 31.2) * mm, "end": v(25.4, 30.83) * mm});
            skArc(sketch, "E664", {"start": v(25.4, 30.83) * mm, "mid": v(25.55, 30.53) * mm, "end": v(25.64, 30.22) * mm});
            skArc(sketch, "E665", {"start": v(25.64, 30.22) * mm, "mid": v(25.62, 30.02) * mm, "end": v(25.47, 29.89) * mm});
            skArc(sketch, "E666", {"start": v(25.47, 29.89) * mm, "mid": v(25.2, 29.82) * mm, "end": v(24.9, 29.84) * mm});
            skArc(sketch, "E667", {"start": v(24.9, 29.84) * mm, "mid": v(24.38, 30) * mm, "end": v(23.87, 30.17) * mm});
            skArc(sketch, "E668", {"start": v(23.87, 30.17) * mm, "mid": v(22.92, 30.4) * mm, "end": v(21.94, 30.4) * mm});
            skArc(sketch, "E669", {"start": v(21.94, 30.4) * mm, "mid": v(21.56, 30.08) * mm, "end": v(21.65, 29.6) * mm});
            skArc(sketch, "E670", {"start": v(21.65, 29.6) * mm, "mid": v(22.97, 28.33) * mm, "end": v(24.44, 27.24) * mm});
            skArc(sketch, "E671", {"start": v(24.44, 27.24) * mm, "mid": v(26.76, 25.8) * mm, "end": v(29.12, 24.44) * mm});
            skArc(sketch, "E672", {"start": v(29.12, 24.44) * mm, "mid": v(30.98, 23.4) * mm, "end": v(32.8, 22.32) * mm});
            skArc(sketch, "E673", {"start": v(32.8, 22.32) * mm, "mid": v(33.8, 21.64) * mm, "end": v(34.7, 20.85) * mm});
            skArc(sketch, "E674", {"start": v(34.7, 20.85) * mm, "mid": v(35.07, 20.35) * mm, "end": v(35.25, 19.76) * mm});
            skArc(sketch, "E675", {"start": v(35.25, 19.76) * mm, "mid": v(35.18, 19.25) * mm, "end": v(34.84, 18.86) * mm});
            skArc(sketch, "E676", {"start": v(34.84, 18.86) * mm, "mid": v(34.32, 18.5) * mm, "end": v(33.83, 18.1) * mm});
            skArc(sketch, "E677", {"start": v(33.83, 18.1) * mm, "mid": v(33.64, 17.82) * mm, "end": v(33.59, 17.5) * mm});
            skArc(sketch, "E678", {"start": v(33.59, 17.5) * mm, "mid": v(33.68, 17.16) * mm, "end": v(33.9, 16.88) * mm});
            skArc(sketch, "E679", {"start": v(33.9, 16.88) * mm, "mid": v(34.46, 16.44) * mm, "end": v(35.05, 16.03) * mm});
            skArc(sketch, "E680", {"start": v(35.05, 16.03) * mm, "mid": v(35.6, 15.7) * mm, "end": v(36.17, 15.45) * mm});
            skArc(sketch, "E681", {"start": v(36.17, 15.45) * mm, "mid": v(36.9, 15.18) * mm, "end": v(37.64, 14.96) * mm});
            skArc(sketch, "E682", {"start": v(37.64, 14.96) * mm, "mid": v(38.43, 14.77) * mm, "end": v(39.23, 14.62) * mm});
            skArc(sketch, "E683", {"start": v(39.23, 14.62) * mm, "mid": v(39.94, 14.53) * mm, "end": v(40.67, 14.5) * mm});
            skArc(sketch, "E684", {"start": v(40.67, 14.5) * mm, "mid": v(41.46, 14.47) * mm, "end": v(42.25, 14.38) * mm});
            skArc(sketch, "E685", {"start": v(42.25, 14.38) * mm, "mid": v(43.26, 14.21) * mm, "end": v(44.27, 14) * mm});
            skArc(sketch, "E686", {"start": v(44.27, 14) * mm, "mid": v(45.33, 13.76) * mm, "end": v(46.38, 13.48) * mm});
            skArc(sketch, "E687", {"start": v(46.38, 13.48) * mm, "mid": v(47.33, 13.19) * mm, "end": v(48.26, 12.86) * mm});
            skArc(sketch, "E688", {"start": v(48.26, 12.86) * mm, "mid": v(49.25, 12.5) * mm, "end": v(50.26, 12.2) * mm});
            skArc(sketch, "E689", {"start": v(50.26, 12.2) * mm, "mid": v(50.95, 12.05) * mm, "end": v(51.64, 12) * mm});
            skArc(sketch, "E690", {"start": v(51.64, 12) * mm, "mid": v(52.1, 12.06) * mm, "end": v(52.54, 12.24) * mm});
            skArc(sketch, "E691", {"start": v(52.54, 12.24) * mm, "mid": v(52.86, 12.5) * mm, "end": v(53.06, 12.87) * mm});
            skArc(sketch, "E692", {"start": v(53.06, 12.87) * mm, "mid": v(53.2, 13.16) * mm, "end": v(53.4, 13.4) * mm});
            skArc(sketch, "E693", {"start": v(53.4, 13.4) * mm, "mid": v(53.64, 13.6) * mm, "end": v(53.93, 13.72) * mm});
            skArc(sketch, "E694", {"start": v(53.93, 13.72) * mm, "mid": v(54.25, 13.77) * mm, "end": v(54.58, 13.74) * mm});
            skArc(sketch, "E695", {"start": v(54.58, 13.74) * mm, "mid": v(54.93, 13.64) * mm, "end": v(55.25, 13.48) * mm});
            skArc(sketch, "E696", {"start": v(55.25, 13.48) * mm, "mid": v(55.6, 13.36) * mm, "end": v(55.96, 13.4) * mm});
            skArc(sketch, "E697", {"start": v(55.96, 13.4) * mm, "mid": v(56.18, 13.58) * mm, "end": v(56.2, 13.87) * mm});
            skArc(sketch, "E698", {"start": v(56.2, 13.87) * mm, "mid": v(55.9, 14.86) * mm, "end": v(55.52, 15.83) * mm});
            skArc(sketch, "E699", {"start": v(55.52, 15.83) * mm, "mid": v(54.11, 19.15) * mm, "end": v(52.7, 22.48) * mm});
            skArc(sketch, "E700", {"start": v(52.7, 22.48) * mm, "mid": v(52, 24.13) * mm, "end": v(51.34, 25.8) * mm});
            skArc(sketch, "E701", {"start": v(51.34, 25.8) * mm, "mid": v(51.14, 26.5) * mm, "end": v(51.05, 27.23) * mm});
            skArc(sketch, "E702", {"start": v(51.05, 27.23) * mm, "mid": v(51.16, 27.63) * mm, "end": v(51.46, 27.92) * mm});
            skArc(sketch, "E703", {"start": v(51.46, 27.92) * mm, "mid": v(52, 28.13) * mm, "end": v(52.56, 28.2) * mm});
            skArc(sketch, "E704", {"start": v(52.56, 28.2) * mm, "mid": v(53.42, 28.37) * mm, "end": v(54.14, 28.88) * mm});
            skArc(sketch, "E705", {"start": v(54.14, 28.88) * mm, "mid": v(54.6, 29.65) * mm, "end": v(54.75, 30.53) * mm});
            skArc(sketch, "E706", {"start": v(54.75, 30.53) * mm, "mid": v(54.57, 31.95) * mm, "end": v(54.13, 33.3) * mm});
            skArc(sketch, "E707", {"start": v(54.13, 33.3) * mm, "mid": v(53.23, 35.24) * mm, "end": v(52.23, 37.12) * mm});
            skArc(sketch, "E708", {"start": v(52.23, 37.12) * mm, "mid": v(51.3, 38.86) * mm, "end": v(50.5, 40.66) * mm});
            skArc(sketch, "E709", {"start": v(50.5, 40.66) * mm, "mid": v(50.35, 41.6) * mm, "end": v(50.65, 42.49) * mm});
            skArc(sketch, "E710", {"start": v(50.65, 42.49) * mm, "mid": v(51.28, 43) * mm, "end": v(52.09, 43.01) * mm});
            skArc(sketch, "E711", {"start": v(52.09, 43.01) * mm, "mid": v(53.63, 42.43) * mm, "end": v(55.11, 41.7) * mm});
            skArc(sketch, "E712", {"start": v(55.11, 41.7) * mm, "mid": v(55.82, 41.32) * mm, "end": v(56.53, 40.94) * mm});
            skArc(sketch, "E713", {"start": v(56.53, 40.94) * mm, "mid": v(57.2, 40.6) * mm, "end": v(57.85, 40.26) * mm});
            skArc(sketch, "E714", {"start": v(57.85, 40.26) * mm, "mid": v(58.4, 39.98) * mm, "end": v(58.97, 39.71) * mm});
            skArc(sketch, "E715", {"start": v(58.97, 39.71) * mm, "mid": v(59.2, 39.62) * mm, "end": v(59.44, 39.55) * mm});
            skArc(sketch, "E716", {"start": v(59.44, 39.55) * mm, "mid": v(60.56, 39.22) * mm, "end": v(61.65, 38.8) * mm});
            skArc(sketch, "E717", {"start": v(61.65, 38.8) * mm, "mid": v(63.11, 38.16) * mm, "end": v(64.55, 37.45) * mm});
            skArc(sketch, "E718", {"start": v(64.55, 37.45) * mm, "mid": v(66.1, 36.63) * mm, "end": v(67.64, 35.76) * mm});
            skArc(sketch, "E719", {"start": v(67.64, 35.76) * mm, "mid": v(69.07, 34.88) * mm, "end": v(70.47, 33.95) * mm});
            skArc(sketch, "E720", {"start": v(70.47, 33.95) * mm, "mid": v(71.31, 33.4) * mm, "end": v(72.18, 32.9) * mm});
            skArc(sketch, "E721", {"start": v(72.18, 32.9) * mm, "mid": v(73, 32.5) * mm, "end": v(73.84, 32.16) * mm});
            skArc(sketch, "E722", {"start": v(73.84, 32.16) * mm, "mid": v(74.54, 31.94) * mm, "end": v(75.25, 31.77) * mm});
            skArc(sketch, "E723", {"start": v(75.25, 31.77) * mm, "mid": v(75.68, 31.77) * mm, "end": v(76.07, 31.92) * mm});
            skArc(sketch, "E724", {"start": v(76.07, 31.92) * mm, "mid": v(76.54, 32.1) * mm, "end": v(77.03, 32.06) * mm});
            skArc(sketch, "E725", {"start": v(77.03, 32.06) * mm, "mid": v(78.32, 31.66) * mm, "end": v(79.6, 31.23) * mm});
            skArc(sketch, "E726", {"start": v(79.6, 31.23) * mm, "mid": v(81.16, 30.63) * mm, "end": v(82.7, 29.97) * mm});
            skArc(sketch, "E727", {"start": v(82.7, 29.97) * mm, "mid": v(84.41, 29.17) * mm, "end": v(86.1, 28.32) * mm});
            skArc(sketch, "E728", {"start": v(86.1, 28.32) * mm, "mid": v(87.95, 27.4) * mm, "end": v(89.83, 26.54) * mm});
            skArc(sketch, "E729", {"start": v(89.83, 26.54) * mm, "mid": v(91.86, 25.68) * mm, "end": v(93.9, 24.88) * mm});
            skArc(sketch, "E730", {"start": v(93.9, 24.88) * mm, "mid": v(95.8, 24.19) * mm, "end": v(97.7, 23.55) * mm});
            skArc(sketch, "E731", {"start": v(97.7, 23.55) * mm, "mid": v(99.1, 23.16) * mm, "end": v(100.53, 22.87) * mm});
            skArc(sketch, "E732", {"start": v(100.53, 22.87) * mm, "mid": v(102.07, 22.58) * mm, "end": v(103.6, 22.23) * mm});
            skArc(sketch, "E733", {"start": v(103.6, 22.23) * mm, "mid": v(104.38, 21.95) * mm, "end": v(105.08, 21.51) * mm});
            skArc(sketch, "E734", {"start": v(105.08, 21.51) * mm, "mid": v(105.48, 21.06) * mm, "end": v(105.67, 20.48) * mm});
            skArc(sketch, "E735", {"start": v(105.67, 20.48) * mm, "mid": v(105.7, 19.7) * mm, "end": v(105.57, 18.94) * mm});
            skArc(sketch, "E736", {"start": v(105.57, 18.94) * mm, "mid": v(105.4, 18.37) * mm, "end": v(105.18, 17.82) * mm});
            skArc(sketch, "E737", {"start": v(105.18, 17.82) * mm, "mid": v(104.93, 17.33) * mm, "end": v(104.63, 16.87) * mm});
            skArc(sketch, "E738", {"start": v(104.63, 16.87) * mm, "mid": v(104.35, 16.52) * mm, "end": v(104.03, 16.21) * mm});
            skArc(sketch, "E739", {"start": v(104.03, 16.21) * mm, "mid": v(103.76, 16.06) * mm, "end": v(103.45, 16) * mm});
            skArc(sketch, "E740", {"start": v(103.45, 16) * mm, "mid": v(103.19, 15.97) * mm, "end": v(102.94, 15.87) * mm});
            skArc(sketch, "E741", {"start": v(102.94, 15.87) * mm, "mid": v(102.7, 15.71) * mm, "end": v(102.5, 15.5) * mm});
            skArc(sketch, "E742", {"start": v(102.5, 15.5) * mm, "mid": v(102.33, 15.25) * mm, "end": v(102.2, 14.96) * mm});
            skArc(sketch, "E743", {"start": v(102.2, 14.96) * mm, "mid": v(102.13, 14.64) * mm, "end": v(102.1, 14.31) * mm});
            skArc(sketch, "E744", {"start": v(102.1, 14.31) * mm, "mid": v(102.16, 14) * mm, "end": v(102.31, 13.74) * mm});
            skArc(sketch, "E745", {"start": v(102.31, 13.74) * mm, "mid": v(102.55, 13.53) * mm, "end": v(102.85, 13.4) * mm});
            skArc(sketch, "E746", {"start": v(102.85, 13.4) * mm, "mid": v(103.26, 13.33) * mm, "end": v(103.68, 13.35) * mm});
            skArc(sketch, "E747", {"start": v(103.68, 13.35) * mm, "mid": v(104.2, 13.46) * mm, "end": v(104.69, 13.62) * mm});
            skArc(sketch, "E748", {"start": v(104.69, 13.62) * mm, "mid": v(105.4, 13.87) * mm, "end": v(106.1, 14.1) * mm});
            skArc(sketch, "E749", {"start": v(106.1, 14.1) * mm, "mid": v(106.28, 14.07) * mm, "end": v(106.35, 13.9) * mm});
            skArc(sketch, "E750", {"start": v(106.35, 13.9) * mm, "mid": v(106.27, 13.61) * mm, "end": v(106.1, 13.36) * mm});
            skArc(sketch, "E751", {"start": v(106.1, 13.36) * mm, "mid": v(105.28, 12.42) * mm, "end": v(104.45, 11.5) * mm});
            skArc(sketch, "E752", {"start": v(104.45, 11.5) * mm, "mid": v(103.7, 10.63) * mm, "end": v(102.95, 9.76) * mm});
            skArc(sketch, "E753", {"start": v(102.95, 9.76) * mm, "mid": v(102.72, 9.38) * mm, "end": v(102.6, 8.96) * mm});
            skArc(sketch, "E754", {"start": v(102.6, 8.96) * mm, "mid": v(102.66, 8.68) * mm, "end": v(102.89, 8.52) * mm});
            skArc(sketch, "E755", {"start": v(102.89, 8.52) * mm, "mid": v(103.44, 8.42) * mm, "end": v(104, 8.38) * mm});
            skArc(sketch, "E756", {"start": v(104, 8.38) * mm, "mid": v(104.96, 8.23) * mm, "end": v(105.82, 7.78) * mm});
            skArc(sketch, "E757", {"start": v(105.82, 7.78) * mm, "mid": v(106.58, 7.06) * mm, "end": v(107.14, 6.17) * mm});
            skArc(sketch, "E758", {"start": v(107.14, 6.17) * mm, "mid": v(107.41, 5.26) * mm, "end": v(107.4, 4.3) * mm});
            skArc(sketch, "E759", {"start": v(107.4, 4.3) * mm, "mid": v(107.1, 3.52) * mm, "end": v(106.5, 2.94) * mm});
            skArc(sketch, "E760", {"start": v(106.5, 2.94) * mm, "mid": v(106.21, 2.71) * mm, "end": v(105.97, 2.42) * mm});
            skArc(sketch, "E761", {"start": v(105.97, 2.42) * mm, "mid": v(105.77, 2.06) * mm, "end": v(105.63, 1.67) * mm});
            skArc(sketch, "E762", {"start": v(105.63, 1.67) * mm, "mid": v(105.55, 1.25) * mm, "end": v(105.54, 0.81) * mm});
            skArc(sketch, "E763", {"start": v(105.54, 0.81) * mm, "mid": v(105.6, 0.38) * mm, "end": v(105.72, -0.03) * mm});
            skArc(sketch, "E764", {"start": v(105.72, -0.03) * mm, "mid": v(105.83, -0.44) * mm, "end": v(105.84, -0.86) * mm});
            skArc(sketch, "E765", {"start": v(105.84, -0.86) * mm, "mid": v(105.77, -1.29) * mm, "end": v(105.62, -1.7) * mm});
            skArc(sketch, "E766", {"start": v(105.62, -1.7) * mm, "mid": v(105.38, -2.07) * mm, "end": v(105.08, -2.4) * mm});
            skArc(sketch, "E767", {"start": v(105.08, -2.4) * mm, "mid": v(104.7, -2.67) * mm, "end": v(104.3, -2.87) * mm});
            skArc(sketch, "E768", {"start": v(104.3, -2.87) * mm, "mid": v(103.4, -3.33) * mm, "end": v(102.6, -3.95) * mm});
            skArc(sketch, "E769", {"start": v(102.6, -3.95) * mm, "mid": v(102.23, -4.55) * mm, "end": v(102.21, -5.26) * mm});
            skArc(sketch, "E770", {"start": v(102.21, -5.26) * mm, "mid": v(102.56, -5.97) * mm, "end": v(103.18, -6.46) * mm});
            skArc(sketch, "E771", {"start": v(103.18, -6.46) * mm, "mid": v(104.24, -6.88) * mm, "end": v(105.35, -7.13) * mm});
            skArc(sketch, "E772", {"start": v(105.35, -7.13) * mm, "mid": v(106.28, -7.3) * mm, "end": v(107.2, -7.54) * mm});
            skArc(sketch, "E773", {"start": v(107.2, -7.54) * mm, "mid": v(107.5, -7.77) * mm, "end": v(107.56, -8.13) * mm});
            skArc(sketch, "E774", {"start": v(107.56, -8.13) * mm, "mid": v(107.38, -8.64) * mm, "end": v(107.06, -9.07) * mm});
            skArc(sketch, "E775", {"start": v(107.06, -9.07) * mm, "mid": v(105.73, -10.45) * mm, "end": v(104.38, -11.81) * mm});
            skArc(sketch, "E776", {"start": v(104.38, -11.81) * mm, "mid": v(103.6, -12.6) * mm, "end": v(102.86, -13.42) * mm});
            skArc(sketch, "E777", {"start": v(102.86, -13.42) * mm, "mid": v(102.3, -14.08) * mm, "end": v(101.8, -14.77) * mm});
            skArc(sketch, "E778", {"start": v(101.8, -14.77) * mm, "mid": v(101.54, -15.22) * mm, "end": v(101.32, -15.7) * mm});
            skArc(sketch, "E779", {"start": v(101.32, -15.7) * mm, "mid": v(101.35, -15.9) * mm, "end": v(101.53, -16) * mm});
            skArc(sketch, "E780", {"start": v(101.53, -16) * mm, "mid": v(101.88, -16.05) * mm, "end": v(102.19, -16.2) * mm});
            skArc(sketch, "E781", {"start": v(102.19, -16.2) * mm, "mid": v(102.65, -16.55) * mm, "end": v(103.08, -16.93) * mm});
            skArc(sketch, "E782", {"start": v(103.08, -16.93) * mm, "mid": v(103.57, -17.43) * mm, "end": v(104.02, -17.96) * mm});
            skArc(sketch, "E783", {"start": v(104.02, -17.96) * mm, "mid": v(104.47, -18.55) * mm, "end": v(104.88, -19.17) * mm});
            skArc(sketch, "E784", {"start": v(104.88, -19.17) * mm, "mid": v(105.35, -19.99) * mm, "end": v(105.76, -20.84) * mm});
            skArc(sketch, "E785", {"start": v(105.76, -20.84) * mm, "mid": v(105.97, -21.47) * mm, "end": v(106.06, -22.13) * mm});
            skArc(sketch, "E786", {"start": v(106.06, -22.13) * mm, "mid": v(106.01, -22.72) * mm, "end": v(105.83, -23.28) * mm});
            skArc(sketch, "E787", {"start": v(105.83, -23.28) * mm, "mid": v(105.48, -23.92) * mm, "end": v(105.06, -24.5) * mm});
            skArc(sketch, "E788", {"start": v(105.06, -24.5) * mm, "mid": v(104.62, -25.06) * mm, "end": v(104.2, -25.63) * mm});
            skArc(sketch, "E789", {"start": v(104.2, -25.63) * mm, "mid": v(104.08, -25.91) * mm, "end": v(104.07, -26.22) * mm});
            skArc(sketch, "E790", {"start": v(104.07, -26.22) * mm, "mid": v(104.2, -26.45) * mm, "end": v(104.41, -26.57) * mm});
            skArc(sketch, "E791", {"start": v(104.41, -26.57) * mm, "mid": v(104.92, -26.65) * mm, "end": v(105.43, -26.67) * mm});
            skArc(sketch, "E792", {"start": v(105.43, -26.67) * mm, "mid": v(105.91, -26.64) * mm, "end": v(106.39, -26.54) * mm});
            skArc(sketch, "E793", {"start": v(106.39, -26.54) * mm, "mid": v(106.95, -26.36) * mm, "end": v(107.5, -26.13) * mm});
            skArc(sketch, "E794", {"start": v(107.5, -26.13) * mm, "mid": v(108.04, -25.86) * mm, "end": v(108.56, -25.54) * mm});
            skArc(sketch, "E795", {"start": v(108.56, -25.54) * mm, "mid": v(109.01, -25.21) * mm, "end": v(109.42, -24.84) * mm});
            skArc(sketch, "E796", {"start": v(109.42, -24.84) * mm, "mid": v(109.81, -24.47) * mm, "end": v(110.23, -24.13) * mm});
            skArc(sketch, "E797", {"start": v(110.23, -24.13) * mm, "mid": v(110.49, -23.97) * mm, "end": v(110.78, -23.9) * mm});
            skArc(sketch, "E798", {"start": v(110.78, -23.9) * mm, "mid": v(110.98, -23.94) * mm, "end": v(111.12, -24.09) * mm});
            skArc(sketch, "E799", {"start": v(111.12, -24.09) * mm, "mid": v(111.22, -24.36) * mm, "end": v(111.25, -24.65) * mm});
            skArc(sketch, "E800", {"start": v(111.25, -24.65) * mm, "mid": v(111.21, -25.04) * mm, "end": v(111.1, -25.41) * mm});
            skArc(sketch, "E801", {"start": v(111.1, -25.41) * mm, "mid": v(110.87, -25.89) * mm, "end": v(110.61, -26.35) * mm});
            skArc(sketch, "E802", {"start": v(110.61, -26.35) * mm, "mid": v(110.28, -26.83) * mm, "end": v(109.9, -27.3) * mm});
            skArc(sketch, "E803", {"start": v(109.9, -27.3) * mm, "mid": v(109.5, -27.72) * mm, "end": v(109.07, -28.1) * mm});
            skArc(sketch, "E804", {"start": v(109.07, -28.1) * mm, "mid": v(108.45, -28.54) * mm, "end": v(107.77, -28.87) * mm});
            skArc(sketch, "E805", {"start": v(107.77, -28.87) * mm, "mid": v(107.12, -29.04) * mm, "end": v(106.45, -29.06) * mm});
            skArc(sketch, "E806", {"start": v(106.45, -29.06) * mm, "mid": v(105.63, -28.93) * mm, "end": v(104.84, -28.67) * mm});
            skArc(sketch, "E807", {"start": v(104.84, -28.67) * mm, "mid": v(103.7, -28.16) * mm, "end": v(102.6, -27.6) * mm});
            skArc(sketch, "E808", {"start": v(102.6, -27.6) * mm, "mid": v(101.82, -27.16) * mm, "end": v(101.06, -26.7) * mm});
            skArc(sketch, "E809", {"start": v(101.06, -26.7) * mm, "mid": v(100.55, -26.34) * mm, "end": v(100.09, -25.93) * mm});
            skArc(sketch, "E810", {"start": v(100.09, -25.93) * mm, "mid": v(99.93, -25.72) * mm, "end": v(99.86, -25.47) * mm});
            skArc(sketch, "E811", {"start": v(99.86, -25.47) * mm, "mid": v(99.92, -25.29) * mm, "end": v(100.1, -25.2) * mm});
            skArc(sketch, "E812", {"start": v(100.1, -25.2) * mm, "mid": v(101, -24.96) * mm, "end": v(101.7, -24.32) * mm});
            skArc(sketch, "E813", {"start": v(101.7, -24.32) * mm, "mid": v(102.17, -23.31) * mm, "end": v(102.34, -22.2) * mm});
            skArc(sketch, "E814", {"start": v(102.34, -22.2) * mm, "mid": v(102.2, -20.8) * mm, "end": v(101.77, -19.47) * mm});
            skArc(sketch, "E815", {"start": v(101.77, -19.47) * mm, "mid": v(101.05, -18.19) * mm, "end": v(100.12, -17.06) * mm});
            skArc(sketch, "E816", {"start": v(100.12, -17.06) * mm, "mid": v(99.5, -16.4) * mm, "end": v(98.94, -15.69) * mm});
            skArc(sketch, "E817", {"start": v(98.94, -15.69) * mm, "mid": v(98.6, -15.12) * mm, "end": v(98.36, -14.5) * mm});
            skArc(sketch, "E818", {"start": v(98.36, -14.5) * mm, "mid": v(98.29, -13.97) * mm, "end": v(98.35, -13.43) * mm});
            skArc(sketch, "E819", {"start": v(98.35, -13.43) * mm, "mid": v(98.55, -12.9) * mm, "end": v(98.86, -12.43) * mm});
            skArc(sketch, "E820", {"start": v(98.86, -12.43) * mm, "mid": v(99.22, -11.86) * mm, "end": v(99.42, -11.2) * mm});
            skArc(sketch, "E821", {"start": v(99.42, -11.2) * mm, "mid": v(99.5, -10.29) * mm, "end": v(99.5, -9.36) * mm});
            skArc(sketch, "E822", {"start": v(99.5, -9.36) * mm, "mid": v(99.37, -8.13) * mm, "end": v(99.15, -6.92) * mm});
            skArc(sketch, "E823", {"start": v(99.15, -6.92) * mm, "mid": v(98.76, -5.34) * mm, "end": v(98.3, -3.77) * mm});
            skArc(sketch, "E824", {"start": v(98.3, -3.77) * mm, "mid": v(97.87, -2.3) * mm, "end": v(97.44, -0.84) * mm});
            skArc(sketch, "E825", {"start": v(97.44, -0.84) * mm, "mid": v(97, 0.74) * mm, "end": v(96.56, 2.33) * mm});
            skArc(sketch, "E826", {"start": v(96.56, 2.33) * mm, "mid": v(96.17, 3.8) * mm, "end": v(95.79, 5.27) * mm});
            skArc(sketch, "E827", {"start": v(95.79, 5.27) * mm, "mid": v(95.52, 6.34) * mm, "end": v(95.28, 7.42) * mm});
            skArc(sketch, "E828", {"start": v(95.28, 7.42) * mm, "mid": v(94.87, 8.99) * mm, "end": v(94.3, 10.51) * mm});
            skArc(sketch, "E829", {"start": v(94.3, 10.51) * mm, "mid": v(93.9, 10.79) * mm, "end": v(93.48, 10.5) * mm});
            skArc(sketch, "E830", {"start": v(93.48, 10.5) * mm, "mid": v(93.04, 9.1) * mm, "end": v(92.82, 7.63) * mm});
            skArc(sketch, "E831", {"start": v(92.82, 7.63) * mm, "mid": v(92.63, 4.1) * mm, "end": v(92.48, 0.55) * mm});
            skArc(sketch, "E832", {"start": v(92.48, 0.55) * mm, "mid": v(92.4, -1.38) * mm, "end": v(92.28, -3.3) * mm});
            skArc(sketch, "E833", {"start": v(92.28, -3.3) * mm, "mid": v(92.12, -5.08) * mm, "end": v(91.9, -6.86) * mm});
            skArc(sketch, "E834", {"start": v(91.9, -6.86) * mm, "mid": v(91.7, -8.33) * mm, "end": v(91.45, -9.8) * mm});
            skArc(sketch, "E835", {"start": v(91.45, -9.8) * mm, "mid": v(91.26, -10.44) * mm, "end": v(90.96, -11.05) * mm});
            skArc(sketch, "E836", {"start": v(90.96, -11.05) * mm, "mid": v(90.74, -11.44) * mm, "end": v(90.58, -11.87) * mm});
            skArc(sketch, "E837", {"start": v(90.58, -11.87) * mm, "mid": v(90.56, -12.17) * mm, "end": v(90.66, -12.46) * mm});
            skArc(sketch, "E838", {"start": v(90.66, -12.46) * mm, "mid": v(90.87, -12.7) * mm, "end": v(91.16, -12.84) * mm});
            skArc(sketch, "E839", {"start": v(91.16, -12.84) * mm, "mid": v(91.63, -12.92) * mm, "end": v(92.1, -12.95) * mm});
            skArc(sketch, "E840", {"start": v(92.1, -12.95) * mm, "mid": v(92.98, -13.19) * mm, "end": v(93.63, -13.82) * mm});
            skArc(sketch, "E841", {"start": v(93.63, -13.82) * mm, "mid": v(93.98, -14.78) * mm, "end": v(93.96, -15.8) * mm});
            skArc(sketch, "E842", {"start": v(93.96, -15.8) * mm, "mid": v(93.49, -17.32) * mm, "end": v(92.74, -18.72) * mm});
            skArc(sketch, "E843", {"start": v(92.74, -18.72) * mm, "mid": v(91.58, -20.3) * mm, "end": v(90.26, -21.76) * mm});
            skArc(sketch, "E844", {"start": v(90.26, -21.76) * mm, "mid": v(88.94, -23.15) * mm, "end": v(87.72, -24.62) * mm});
            skArc(sketch, "E845", {"start": v(87.72, -24.62) * mm, "mid": v(87.21, -25.54) * mm, "end": v(87.02, -26.57) * mm});
            skArc(sketch, "E846", {"start": v(87.02, -26.57) * mm, "mid": v(87.23, -27.3) * mm, "end": v(87.82, -27.77) * mm});
            skArc(sketch, "E847", {"start": v(87.82, -27.77) * mm, "mid": v(88.94, -28.09) * mm, "end": v(90.1, -28.2) * mm});
            skArc(sketch, "E848", {"start": v(90.1, -28.2) * mm, "mid": v(90.9, -28.21) * mm, "end": v(91.7, -28.27) * mm});
            skArc(sketch, "E849", {"start": v(91.7, -28.27) * mm, "mid": v(92.05, -28.38) * mm, "end": v(92.32, -28.62) * mm});
            skArc(sketch, "E850", {"start": v(92.32, -28.62) * mm, "mid": v(92.43, -28.9) * mm, "end": v(92.36, -29.2) * mm});
            skArc(sketch, "E851", {"start": v(92.36, -29.2) * mm, "mid": v(92.02, -29.74) * mm, "end": v(91.64, -30.24) * mm});
            skArc(sketch, "E852", {"start": v(91.64, -30.24) * mm, "mid": v(91.33, -30.66) * mm, "end": v(91.07, -31.1) * mm});
            skArc(sketch, "E853", {"start": v(91.07, -31.1) * mm, "mid": v(90.9, -31.55) * mm, "end": v(90.77, -32.01) * mm});
            skArc(sketch, "E854", {"start": v(90.77, -32.01) * mm, "mid": v(90.73, -32.42) * mm, "end": v(90.77, -32.83) * mm});
            skArc(sketch, "E855", {"start": v(90.77, -32.83) * mm, "mid": v(90.87, -33.14) * mm, "end": v(91.07, -33.41) * mm});
            skArc(sketch, "E856", {"start": v(91.07, -33.41) * mm, "mid": v(91.15, -33.57) * mm, "end": v(91.1, -33.75) * mm});
            skArc(sketch, "E857", {"start": v(91.1, -33.75) * mm, "mid": v(90.95, -33.9) * mm, "end": v(90.75, -33.97) * mm});
            skArc(sketch, "E858", {"start": v(90.75, -33.97) * mm, "mid": v(90.26, -34) * mm, "end": v(89.78, -33.96) * mm});
            skArc(sketch, "E859", {"start": v(89.78, -33.96) * mm, "mid": v(89.08, -33.86) * mm, "end": v(88.39, -33.72) * mm});
            skArc(sketch, "E860", {"start": v(88.39, -33.72) * mm, "mid": v(84.66, -33) * mm, "end": v(80.9, -32.4) * mm});
            skArc(sketch, "E861", {"start": v(80.9, -32.4) * mm, "mid": v(76.74, -31.89) * mm, "end": v(72.56, -31.48) * mm});
            skArc(sketch, "E862", {"start": v(72.56, -31.48) * mm, "mid": v(67.69, -31.13) * mm, "end": v(62.82, -30.9) * mm});
            skArc(sketch, "E863", {"start": v(62.82, -30.9) * mm, "mid": v(56.94, -30.71) * mm, "end": v(51.05, -30.6) * mm});
            skArc(sketch, "E864", {"start": v(51.05, -30.6) * mm, "mid": v(43.58, -30.45) * mm, "end": v(36.11, -30.15) * mm});
            skArc(sketch, "E865", {"start": v(36.11, -30.15) * mm, "mid": v(30.04, -29.75) * mm, "end": v(23.98, -29.12) * mm});
            skArc(sketch, "E866", {"start": v(23.98, -29.12) * mm, "mid": v(19.19, -28.44) * mm, "end": v(14.42, -27.55) * mm});
            skArc(sketch, "E867", {"start": v(14.42, -27.55) * mm, "mid": v(10.98, -26.64) * mm, "end": v(7.65, -25.37) * mm});
            skLineSegment(sketch, "E868", {"start": v(7.65, -25.37) * mm, "end": v(2.29, -22.99) * mm});
            skLineSegment(sketch, "E869", {"start": v(2.29, -22.99) * mm, "end": v(8.38, -22) * mm});
            skArc(sketch, "E870", {"start": v(8.38, -22) * mm, "mid": v(10.45, -21.66) * mm, "end": v(12.52, -21.31) * mm});
            skArc(sketch, "E871", {"start": v(12.52, -21.31) * mm, "mid": v(12.6, -21.22) * mm, "end": v(12.55, -21.11) * mm});
            skArc(sketch, "E872", {"start": v(12.55, -21.11) * mm, "mid": v(12.27, -21) * mm, "end": v(11.97, -20.95) * mm});
            skArc(sketch, "E873", {"start": v(11.97, -20.95) * mm, "mid": v(9.1, -20.87) * mm, "end": v(6.24, -20.8) * mm});
            skArc(sketch, "E874", {"start": v(6.24, -20.8) * mm, "mid": v(3.75, -20.66) * mm, "end": v(1.27, -20.41) * mm});
            skArc(sketch, "E875", {"start": v(1.27, -20.41) * mm, "mid": v(-0.36, -20.08) * mm, "end": v(-1.92, -19.49) * mm});
            skArc(sketch, "E876", {"start": v(-1.92, -19.49) * mm, "mid": v(-3.51, -18.6) * mm, "end": v(-4.97, -17.52) * mm});
            skArc(sketch, "E877", {"start": v(-4.97, -17.52) * mm, "mid": v(-7.4, -15.41) * mm, "end": v(-9.76, -13.24) * mm});
            skArc(sketch, "E878", {"start": v(-9.76, -13.24) * mm, "mid": v(-11.33, -11.77) * mm, "end": v(-12.91, -10.32) * mm});
            skArc(sketch, "E879", {"start": v(-12.91, -10.32) * mm, "mid": v(-14.43, -8.97) * mm, "end": v(-15.97, -7.64) * mm});
            skArc(sketch, "E880", {"start": v(-15.97, -7.64) * mm, "mid": v(-17.29, -6.53) * mm, "end": v(-18.61, -5.43) * mm});
            skArc(sketch, "E881", {"start": v(-18.61, -5.43) * mm, "mid": v(-19.29, -4.93) * mm, "end": v(-20, -4.47) * mm});
            skArc(sketch, "E882", {"start": v(-20, -4.47) * mm, "mid": v(-20.63, -4.06) * mm, "end": v(-21.2, -3.58) * mm});
            skArc(sketch, "E883", {"start": v(-21.2, -3.58) * mm, "mid": v(-22.03, -2.75) * mm, "end": v(-22.82, -1.9) * mm});
            skArc(sketch, "E884", {"start": v(-22.82, -1.9) * mm, "mid": v(-23.7, -0.89) * mm, "end": v(-24.54, 0.15) * mm});
            skArc(sketch, "E885", {"start": v(-24.54, 0.15) * mm, "mid": v(-25.34, 1.21) * mm, "end": v(-26.1, 2.3) * mm});
            skArc(sketch, "E886", {"start": v(-26.1, 2.3) * mm, "mid": v(-27.78, 4.63) * mm, "end": v(-29.6, 6.86) * mm});
            skArc(sketch, "E887", {"start": v(-29.6, 6.86) * mm, "mid": v(-31.95, 9.49) * mm, "end": v(-34.4, 12.04) * mm});
            skArc(sketch, "E888", {"start": v(-34.4, 12.04) * mm, "mid": v(-36.8, 14.43) * mm, "end": v(-39.25, 16.78) * mm});
            skArc(sketch, "E889", {"start": v(-39.25, 16.78) * mm, "mid": v(-40.12, 17.33) * mm, "end": v(-41.13, 17.53) * mm});
            skArc(sketch, "E890", {"start": v(-41.13, 17.53) * mm, "mid": v(-41.67, 17.67) * mm, "end": v(-42.08, 18.06) * mm});
            skArc(sketch, "E891", {"start": v(-42.08, 18.06) * mm, "mid": v(-42.97, 19.6) * mm, "end": v(-43.81, 21.18) * mm});
            skArc(sketch, "E892", {"start": v(-43.81, 21.18) * mm, "mid": v(-44.6, 22.76) * mm, "end": v(-45.33, 24.38) * mm});
            skArc(sketch, "E893", {"start": v(-45.33, 24.38) * mm, "mid": v(-45.62, 25.33) * mm, "end": v(-45.72, 26.32) * mm});
            skArc(sketch, "E894", {"start": v(-45.72, 26.32) * mm, "mid": v(-45.63, 26.46) * mm, "end": v(-45.47, 26.45) * mm});
            skArc(sketch, "E895", {"start": v(-45.47, 26.45) * mm, "mid": v(-44.93, 26.04) * mm, "end": v(-44.4, 25.6) * mm});
            skArc(sketch, "E896", {"start": v(-44.4, 25.6) * mm, "mid": v(-43.67, 24.94) * mm, "end": v(-42.96, 24.25) * mm});
            skArc(sketch, "E897", {"start": v(-42.96, 24.25) * mm, "mid": v(-42.09, 23.35) * mm, "end": v(-41.23, 22.44) * mm});
            skArc(sketch, "E898", {"start": v(-41.23, 22.44) * mm, "mid": v(-39.86, 21.01) * mm, "end": v(-38.41, 19.66) * mm});
            skArc(sketch, "E899", {"start": v(-38.41, 19.66) * mm, "mid": v(-37.2, 18.72) * mm, "end": v(-35.9, 17.91) * mm});
            skArc(sketch, "E900", {"start": v(-35.9, 17.91) * mm, "mid": v(-35.1, 17.61) * mm, "end": v(-34.25, 17.53) * mm});
            skArc(sketch, "E901", {"start": v(-34.25, 17.53) * mm, "mid": v(-33.74, 17.76) * mm, "end": v(-33.53, 18.28) * mm});
            skArc(sketch, "E902", {"start": v(-33.53, 18.28) * mm, "mid": v(-33.57, 18.54) * mm, "end": v(-33.7, 18.77) * mm});
            skArc(sketch, "E903", {"start": v(-33.7, 18.77) * mm, "mid": v(-34.35, 19.64) * mm, "end": v(-35.02, 20.5) * mm});
            skArc(sketch, "E904", {"start": v(-35.02, 20.5) * mm, "mid": v(-35.82, 21.51) * mm, "end": v(-36.65, 22.51) * mm});
            skArc(sketch, "E905", {"start": v(-36.65, 22.51) * mm, "mid": v(-37.62, 23.64) * mm, "end": v(-38.6, 24.76) * mm});
            skArc(sketch, "E906", {"start": v(-38.6, 24.76) * mm, "mid": v(-40.88, 27.5) * mm, "end": v(-42.99, 30.38) * mm});
            skArc(sketch, "E907", {"start": v(-42.99, 30.38) * mm, "mid": v(-45.25, 33.82) * mm, "end": v(-47.37, 37.34) * mm});
            skArc(sketch, "E908", {"start": v(-47.37, 37.34) * mm, "mid": v(-49.17, 40.57) * mm, "end": v(-50.88, 43.85) * mm});
            skArc(sketch, "E909", {"start": v(-50.88, 43.85) * mm, "mid": v(-50.85, 44.6) * mm, "end": v(-50.2, 44.96) * mm});
            skArc(sketch, "E910", {"start": v(-50.2, 44.96) * mm, "mid": v(-49.8, 44.88) * mm, "end": v(-49.47, 44.67) * mm});
            skArc(sketch, "E911", {"start": v(-49.47, 44.67) * mm, "mid": v(-48.82, 44.05) * mm, "end": v(-48.2, 43.4) * mm});
            skArc(sketch, "E912", {"start": v(-48.2, 43.4) * mm, "mid": v(-47.46, 42.55) * mm, "end": v(-46.77, 41.68) * mm});
            skArc(sketch, "E913", {"start": v(-46.77, 41.68) * mm, "mid": v(-46.05, 40.67) * mm, "end": v(-45.35, 39.64) * mm});
            skArc(sketch, "E914", {"start": v(-45.35, 39.64) * mm, "mid": v(-44, 37.66) * mm, "end": v(-42.58, 35.73) * mm});
            skArc(sketch, "E915", {"start": v(-42.58, 35.73) * mm, "mid": v(-41.78, 34.97) * mm, "end": v(-40.77, 34.5) * mm});
            skArc(sketch, "E916", {"start": v(-40.77, 34.5) * mm, "mid": v(-40.15, 34.63) * mm, "end": v(-39.87, 35.2) * mm});
            skArc(sketch, "E917", {"start": v(-39.87, 35.2) * mm, "mid": v(-40, 36.73) * mm, "end": v(-40.28, 38.23) * mm});
            skArc(sketch, "E918", {"start": v(-40.28, 38.23) * mm, "mid": v(-40.47, 39.06) * mm, "end": v(-40.63, 39.9) * mm});
            skArc(sketch, "E919", {"start": v(-40.63, 39.9) * mm, "mid": v(-40.66, 40.4) * mm, "end": v(-40.6, 40.9) * mm});
            skArc(sketch, "E920", {"start": v(-40.6, 40.9) * mm, "mid": v(-40.49, 41.14) * mm, "end": v(-40.26, 41.27) * mm});
            skArc(sketch, "E921", {"start": v(-40.26, 41.27) * mm, "mid": v(-39.96, 41.29) * mm, "end": v(-39.69, 41.19) * mm});
            skArc(sketch, "E922", {"start": v(-39.69, 41.19) * mm, "mid": v(-39.18, 40.94) * mm, "end": v(-38.63, 40.8) * mm});
            skArc(sketch, "E923", {"start": v(-38.63, 40.8) * mm, "mid": v(-38.34, 40.9) * mm, "end": v(-38.24, 41.2) * mm});
            skArc(sketch, "E924", {"start": v(-38.24, 41.2) * mm, "mid": v(-38.4, 41.98) * mm, "end": v(-38.64, 42.74) * mm});
            skArc(sketch, "E925", {"start": v(-38.64, 42.74) * mm, "mid": v(-39.54, 44.96) * mm, "end": v(-40.45, 47.17) * mm});
            skArc(sketch, "E926", {"start": v(-40.45, 47.17) * mm, "mid": v(-41.18, 49.2) * mm, "end": v(-41.68, 51.29) * mm});
            skArc(sketch, "E927", {"start": v(-41.68, 51.29) * mm, "mid": v(-41.91, 53.25) * mm, "end": v(-41.87, 55.23) * mm});
            skArc(sketch, "E928", {"start": v(-41.87, 55.23) * mm, "mid": v(-41.6, 56.44) * mm, "end": v(-41.02, 57.54) * mm});
            skArc(sketch, "E929", {"start": v(-41.02, 57.54) * mm, "mid": v(-40.33, 57.99) * mm, "end": v(-39.51, 57.84) * mm});
            skArc(sketch, "E930", {"start": v(-39.51, 57.84) * mm, "mid": v(-39.25, 57.71) * mm, "end": v(-38.97, 57.63) * mm});
            skArc(sketch, "E931", {"start": v(-38.97, 57.63) * mm, "mid": v(-38.74, 57.61) * mm, "end": v(-38.52, 57.67) * mm});
            skArc(sketch, "E932", {"start": v(-38.52, 57.67) * mm, "mid": v(-38.34, 57.8) * mm, "end": v(-38.21, 57.98) * mm});
            skArc(sketch, "E933", {"start": v(-38.21, 57.98) * mm, "mid": v(-38.13, 58.23) * mm, "end": v(-38.1, 58.5) * mm});
            skArc(sketch, "E934", {"start": v(-38.1, 58.5) * mm, "mid": v(-38.13, 58.83) * mm, "end": v(-38.21, 59.15) * mm});
            skArc(sketch, "E935", {"start": v(-38.21, 59.15) * mm, "mid": v(-38.36, 59.5) * mm, "end": v(-38.55, 59.85) * mm});
            skArc(sketch, "E936", {"start": v(-38.55, 59.85) * mm, "mid": v(-38.78, 60.18) * mm, "end": v(-39.04, 60.49) * mm});
            skArc(sketch, "E937", {"start": v(-39.04, 60.49) * mm, "mid": v(-39.32, 60.74) * mm, "end": v(-39.62, 60.96) * mm});
            skArc(sketch, "E938", {"start": v(-39.62, 60.96) * mm, "mid": v(-39.96, 61.23) * mm, "end": v(-40.2, 61.57) * mm});
            skArc(sketch, "E939", {"start": v(-40.2, 61.57) * mm, "mid": v(-40.48, 62.11) * mm, "end": v(-40.7, 62.68) * mm});
            skArc(sketch, "E940", {"start": v(-40.7, 62.68) * mm, "mid": v(-40.9, 63.35) * mm, "end": v(-41.04, 64.04) * mm});
            skArc(sketch, "E941", {"start": v(-41.04, 64.04) * mm, "mid": v(-41.12, 64.76) * mm, "end": v(-41.15, 65.48) * mm});
            skArc(sketch, "E942", {"start": v(-41.15, 65.48) * mm, "mid": v(-41.12, 66.5) * mm, "end": v(-41.04, 67.52) * mm});
            skArc(sketch, "E943", {"start": v(-41.04, 67.52) * mm, "mid": v(-40.89, 67.93) * mm, "end": v(-40.56, 68.21) * mm});
            skArc(sketch, "E944", {"start": v(-40.56, 68.21) * mm, "mid": v(-40.1, 68.33) * mm, "end": v(-39.64, 68.25) * mm});
            skArc(sketch, "E945", {"start": v(-39.64, 68.25) * mm, "mid": v(-38.51, 67.8) * mm, "end": v(-37.4, 67.3) * mm});
            skArc(sketch, "E946", {"start": v(-37.4, 67.3) * mm, "mid": v(-36.63, 66.87) * mm, "end": v(-35.91, 66.37) * mm});
            skArc(sketch, "E947", {"start": v(-35.91, 66.37) * mm, "mid": v(-35.19, 65.74) * mm, "end": v(-34.51, 65.04) * mm});
            skArc(sketch, "E948", {"start": v(-34.51, 65.04) * mm, "mid": v(-33.93, 64.32) * mm, "end": v(-33.41, 63.54) * mm});
            skArc(sketch, "E949", {"start": v(-33.41, 63.54) * mm, "mid": v(-33.06, 62.85) * mm, "end": v(-32.8, 62.1) * mm});
            skArc(sketch, "E950", {"start": v(-60.85, 52.16) * mm, "mid": v(-60.99, 51.67) * mm, "end": v(-61.28, 51.25) * mm});
            skArc(sketch, "E951", {"start": v(-61.28, 51.25) * mm, "mid": v(-61.68, 51.02) * mm, "end": v(-62.14, 50.99) * mm});
            skArc(sketch, "E952", {"start": v(-62.14, 50.99) * mm, "mid": v(-62.67, 51.17) * mm, "end": v(-63.11, 51.52) * mm});
            skArc(sketch, "E953", {"start": v(-63.11, 51.52) * mm, "mid": v(-63.5, 52.05) * mm, "end": v(-63.78, 52.65) * mm});
            skArc(sketch, "E954", {"start": v(-63.78, 52.65) * mm, "mid": v(-63.86, 52.98) * mm, "end": v(-63.87, 53.3) * mm});
            skArc(sketch, "E955", {"start": v(-63.87, 53.3) * mm, "mid": v(-63.82, 53.56) * mm, "end": v(-63.67, 53.77) * mm});
            skArc(sketch, "E956", {"start": v(-63.67, 53.77) * mm, "mid": v(-63.46, 53.91) * mm, "end": v(-63.21, 53.97) * mm});
            skArc(sketch, "E957", {"start": v(-63.21, 53.97) * mm, "mid": v(-62.88, 53.95) * mm, "end": v(-62.56, 53.87) * mm});
            skArc(sketch, "E958", {"start": v(-62.56, 53.87) * mm, "mid": v(-62.2, 53.73) * mm, "end": v(-61.87, 53.56) * mm});
            skArc(sketch, "E959", {"start": v(-61.87, 53.56) * mm, "mid": v(-61.57, 53.36) * mm, "end": v(-61.3, 53.12) * mm});
            skArc(sketch, "E960", {"start": v(-61.3, 53.12) * mm, "mid": v(-61.1, 52.89) * mm, "end": v(-60.94, 52.63) * mm});
            skArc(sketch, "E961", {"start": v(-60.94, 52.63) * mm, "mid": v(-60.86, 52.4) * mm, "end": v(-60.85, 52.16) * mm});
            skArc(sketch, "E962", {"start": v(120.53, 18.37) * mm, "mid": v(120.78, 18.5) * mm, "end": v(121.06, 18.57) * mm});
            skArc(sketch, "E963", {"start": v(121.06, 18.57) * mm, "mid": v(121.3, 18.58) * mm, "end": v(121.51, 18.5) * mm});
            skArc(sketch, "E964", {"start": v(121.51, 18.5) * mm, "mid": v(121.7, 18.36) * mm, "end": v(121.81, 18.17) * mm});
            skArc(sketch, "E965", {"start": v(121.81, 18.17) * mm, "mid": v(121.9, 17.9) * mm, "end": v(121.92, 17.62) * mm});
            skArc(sketch, "E966", {"start": v(121.92, 17.62) * mm, "mid": v(121.76, 17) * mm, "end": v(121.32, 16.54) * mm});
            skArc(sketch, "E967", {"start": v(121.32, 16.54) * mm, "mid": v(120.56, 16.2) * mm, "end": v(119.75, 16.04) * mm});
            skArc(sketch, "E968", {"start": v(119.75, 16.04) * mm, "mid": v(118.82, 16.08) * mm, "end": v(117.93, 16.32) * mm});
            skArc(sketch, "E969", {"start": v(117.93, 16.32) * mm, "mid": v(117.24, 16.72) * mm, "end": v(116.72, 17.31) * mm});
            skArc(sketch, "E970", {"start": v(116.72, 17.31) * mm, "mid": v(116.58, 17.6) * mm, "end": v(116.49, 17.9) * mm});
            skArc(sketch, "E971", {"start": v(116.49, 17.9) * mm, "mid": v(116.45, 18.22) * mm, "end": v(116.46, 18.55) * mm});
            skArc(sketch, "E972", {"start": v(116.46, 18.55) * mm, "mid": v(116.52, 18.88) * mm, "end": v(116.63, 19.19) * mm});
            skArc(sketch, "E973", {"start": v(116.63, 19.19) * mm, "mid": v(116.78, 19.46) * mm, "end": v(116.98, 19.7) * mm});
            skArc(sketch, "E974", {"start": v(116.98, 19.7) * mm, "mid": v(117.19, 19.86) * mm, "end": v(117.43, 19.97) * mm});
            skArc(sketch, "E975", {"start": v(117.43, 19.97) * mm, "mid": v(117.66, 20.01) * mm, "end": v(117.9, 19.97) * mm});
            skArc(sketch, "E976", {"start": v(117.9, 19.97) * mm, "mid": v(118.12, 19.85) * mm, "end": v(118.3, 19.68) * mm});
            skArc(sketch, "E977", {"start": v(118.3, 19.68) * mm, "mid": v(118.47, 19.42) * mm, "end": v(118.59, 19.14) * mm});
            skArc(sketch, "E978", {"start": v(118.59, 19.14) * mm, "mid": v(118.72, 18.84) * mm, "end": v(118.9, 18.58) * mm});
            skArc(sketch, "E979", {"start": v(118.9, 18.58) * mm, "mid": v(119.12, 18.38) * mm, "end": v(119.38, 18.24) * mm});
            skArc(sketch, "E980", {"start": v(119.38, 18.24) * mm, "mid": v(119.66, 18.17) * mm, "end": v(119.95, 18.17) * mm});
            skArc(sketch, "E981", {"start": v(119.95, 18.17) * mm, "mid": v(120.25, 18.24) * mm, "end": v(120.53, 18.37) * mm});
            skArc(sketch, "E982", {"start": v(-72.44, 16.87) * mm, "mid": v(-71.11, 16.4) * mm, "end": v(-69.78, 15.97) * mm});
            skArc(sketch, "E983", {"start": v(-69.78, 15.97) * mm, "mid": v(-68.32, 15.5) * mm, "end": v(-66.86, 15.06) * mm});
            skArc(sketch, "E984", {"start": v(-66.86, 15.06) * mm, "mid": v(-65.5, 14.67) * mm, "end": v(-64.12, 14.28) * mm});
            skArc(sketch, "E985", {"start": v(-64.12, 14.28) * mm, "mid": v(-63.1, 14.02) * mm, "end": v(-62.08, 13.79) * mm});
            skArc(sketch, "E986", {"start": v(-62.08, 13.79) * mm, "mid": v(-60.93, 13.43) * mm, "end": v(-59.87, 12.87) * mm});
            skArc(sketch, "E987", {"start": v(-59.87, 12.87) * mm, "mid": v(-58.15, 11.7) * mm, "end": v(-56.47, 10.47) * mm});
            skArc(sketch, "E988", {"start": v(-56.47, 10.47) * mm, "mid": v(-54.53, 8.92) * mm, "end": v(-52.65, 7.3) * mm});
            skArc(sketch, "E989", {"start": v(-52.65, 7.3) * mm, "mid": v(-50.71, 5.5) * mm, "end": v(-48.84, 3.63) * mm});
            skArc(sketch, "E990", {"start": v(-48.84, 3.63) * mm, "mid": v(-46.53, 1.33) * mm, "end": v(-44.15, -0.9) * mm});
            skArc(sketch, "E991", {"start": v(-44.15, -0.9) * mm, "mid": v(-42.33, -2.47) * mm, "end": v(-40.4, -3.91) * mm});
            skArc(sketch, "E992", {"start": v(-40.4, -3.91) * mm, "mid": v(-38.75, -4.96) * mm, "end": v(-37.02, -5.85) * mm});
            skArc(sketch, "E993", {"start": v(-37.02, -5.85) * mm, "mid": v(-35.3, -6.53) * mm, "end": v(-33.51, -7.03) * mm});
            skArc(sketch, "E994", {"start": v(-33.51, -7.03) * mm, "mid": v(-30.45, -7.9) * mm, "end": v(-27.5, -9.09) * mm});
            skArc(sketch, "E995", {"start": v(-27.5, -9.09) * mm, "mid": v(-22.84, -11.35) * mm, "end": v(-18.25, -13.75) * mm});
            skArc(sketch, "E996", {"start": v(-18.25, -13.75) * mm, "mid": v(-13.56, -16.3) * mm, "end": v(-8.91, -18.93) * mm});
            skArc(sketch, "E997", {"start": v(-8.91, -18.93) * mm, "mid": v(-8.04, -19.78) * mm, "end": v(-7.68, -20.93) * mm});
            skArc(sketch, "E998", {"start": v(-7.68, -20.93) * mm, "mid": v(-7.9, -21.36) * mm, "end": v(-8.36, -21.4) * mm});
            skArc(sketch, "E999", {"start": v(-8.36, -21.4) * mm, "mid": v(-11.14, -20.15) * mm, "end": v(-13.9, -18.85) * mm});
            skArc(sketch, "E1000", {"start": v(-13.9, -18.85) * mm, "mid": v(-16.64, -17.48) * mm, "end": v(-19.34, -16.02) * mm});
            skArc(sketch, "E1001", {"start": v(-19.34, -16.02) * mm, "mid": v(-21.15, -14.9) * mm, "end": v(-22.86, -13.63) * mm});
            skArc(sketch, "E1002", {"start": v(-22.86, -13.63) * mm, "mid": v(-24.51, -12.5) * mm, "end": v(-26.32, -11.62) * mm});
            skArc(sketch, "E1003", {"start": v(-26.32, -11.62) * mm, "mid": v(-28.37, -10.98) * mm, "end": v(-30.5, -10.61) * mm});
            skArc(sketch, "E1004", {"start": v(-30.5, -10.61) * mm, "mid": v(-32.34, -10.55) * mm, "end": v(-34.18, -10.76) * mm});
            skArc(sketch, "E1005", {"start": v(-34.18, -10.76) * mm, "mid": v(-35.34, -11.25) * mm, "end": v(-36.18, -12.19) * mm});
            skArc(sketch, "E1006", {"start": v(-36.18, -12.19) * mm, "mid": v(-36.77, -12.79) * mm, "end": v(-37.6, -13) * mm});
            skArc(sketch, "E1007", {"start": v(-37.6, -13) * mm, "mid": v(-38.8, -12.84) * mm, "end": v(-39.94, -12.45) * mm});
            skArc(sketch, "E1008", {"start": v(-39.94, -12.45) * mm, "mid": v(-42, -11.42) * mm, "end": v(-44, -10.24) * mm});
            skArc(sketch, "E1009", {"start": v(-44, -10.24) * mm, "mid": v(-48.13, -7.56) * mm, "end": v(-52.23, -4.84) * mm});
            skArc(sketch, "E1010", {"start": v(-52.23, -4.84) * mm, "mid": v(-58.77, -0.56) * mm, "end": v(-65.38, 3.62) * mm});
            skArc(sketch, "E1011", {"start": v(-65.38, 3.62) * mm, "mid": v(-68.15, 4.98) * mm, "end": v(-71.14, 5.77) * mm});
            skArc(sketch, "E1012", {"start": v(-71.14, 5.77) * mm, "mid": v(-73.5, 5.7) * mm, "end": v(-75.67, 4.76) * mm});
            skArc(sketch, "E1013", {"start": v(-75.67, 4.76) * mm, "mid": v(-78.67, 2.47) * mm, "end": v(-81.41, -0.12) * mm});
            skArc(sketch, "E1014", {"start": v(-81.41, -0.12) * mm, "mid": v(-83.37, -2.12) * mm, "end": v(-85.38, -4.07) * mm});
            skArc(sketch, "E1015", {"start": v(-85.38, -4.07) * mm, "mid": v(-86.53, -5.02) * mm, "end": v(-87.8, -5.8) * mm});
            skArc(sketch, "E1016", {"start": v(-87.8, -5.8) * mm, "mid": v(-88.87, -6.22) * mm, "end": v(-90, -6.39) * mm});
            skArc(sketch, "E1017", {"start": v(-90, -6.39) * mm, "mid": v(-91.4, -6.35) * mm, "end": v(-92.8, -6.13) * mm});
            skArc(sketch, "E1018", {"start": v(-92.8, -6.13) * mm, "mid": v(-94, -5.92) * mm, "end": v(-95.21, -5.8) * mm});
            skArc(sketch, "E1019", {"start": v(-95.21, -5.8) * mm, "mid": v(-96.2, -5.83) * mm, "end": v(-97.16, -6) * mm});
            skArc(sketch, "E1020", {"start": v(-97.16, -6) * mm, "mid": v(-98.08, -6.33) * mm, "end": v(-98.93, -6.8) * mm});
            skArc(sketch, "E1021", {"start": v(-98.93, -6.8) * mm, "mid": v(-99.9, -7.5) * mm, "end": v(-100.82, -8.27) * mm});
            skArc(sketch, "E1022", {"start": v(-100.82, -8.27) * mm, "mid": v(-102.21, -9.42) * mm, "end": v(-103.74, -10.38) * mm});
            skArc(sketch, "E1023", {"start": v(-103.74, -10.38) * mm, "mid": v(-105.19, -11) * mm, "end": v(-106.72, -11.32) * mm});
            skArc(sketch, "E1024", {"start": v(-106.72, -11.32) * mm, "mid": v(-107.82, -11.27) * mm, "end": v(-108.84, -10.87) * mm});
            skArc(sketch, "E1025", {"start": v(-108.84, -10.87) * mm, "mid": v(-109.5, -10.2) * mm, "end": v(-109.73, -9.3) * mm});
            skArc(sketch, "E1026", {"start": v(-109.73, -9.3) * mm, "mid": v(-109.78, -8.85) * mm, "end": v(-109.93, -8.41) * mm});
            skArc(sketch, "E1027", {"start": v(-109.93, -8.41) * mm, "mid": v(-110.19, -7.93) * mm, "end": v(-110.51, -7.48) * mm});
            skArc(sketch, "E1028", {"start": v(-110.51, -7.48) * mm, "mid": v(-110.92, -7.04) * mm, "end": v(-111.38, -6.66) * mm});
            skArc(sketch, "E1029", {"start": v(-111.38, -6.66) * mm, "mid": v(-111.87, -6.34) * mm, "end": v(-112.4, -6.08) * mm});
            skArc(sketch, "E1030", {"start": v(-112.4, -6.08) * mm, "mid": v(-113.02, -5.78) * mm, "end": v(-113.6, -5.4) * mm});
            skArc(sketch, "E1031", {"start": v(-113.6, -5.4) * mm, "mid": v(-113.79, -5.13) * mm, "end": v(-113.73, -4.8) * mm});
            skArc(sketch, "E1032", {"start": v(-113.73, -4.8) * mm, "mid": v(-113.4, -4.42) * mm, "end": v(-112.98, -4.13) * mm});
            skArc(sketch, "E1033", {"start": v(-112.98, -4.13) * mm, "mid": v(-111.74, -3.55) * mm, "end": v(-110.5, -2.99) * mm});
            skArc(sketch, "E1034", {"start": v(-110.5, -2.99) * mm, "mid": v(-109.25, -2.43) * mm, "end": v(-108.02, -1.85) * mm});
            skArc(sketch, "E1035", {"start": v(-108.02, -1.85) * mm, "mid": v(-107.6, -1.57) * mm, "end": v(-107.27, -1.18) * mm});
            skArc(sketch, "E1036", {"start": v(-107.27, -1.18) * mm, "mid": v(-107.21, -0.87) * mm, "end": v(-107.39, -0.6) * mm});
            skArc(sketch, "E1037", {"start": v(-107.39, -0.6) * mm, "mid": v(-107.97, -0.24) * mm, "end": v(-108.59, 0.04) * mm});
            skArc(sketch, "E1038", {"start": v(-108.58, 0.04) * mm, "mid": v(-109.1, 0.27) * mm, "end": v(-109.6, 0.55) * mm});
            skArc(sketch, "E1039", {"start": v(-109.6, 0.55) * mm, "mid": v(-110.05, 0.86) * mm, "end": v(-110.47, 1.2) * mm});
            skArc(sketch, "E1040", {"start": v(-110.47, 1.2) * mm, "mid": v(-110.79, 1.54) * mm, "end": v(-111.06, 1.9) * mm});
            skArc(sketch, "E1041", {"start": v(-111.06, 1.9) * mm, "mid": v(-111.2, 2.2) * mm, "end": v(-111.25, 2.54) * mm});
            skArc(sketch, "E1042", {"start": v(-111.25, 2.54) * mm, "mid": v(-111.22, 2.79) * mm, "end": v(-111.14, 3.02) * mm});
            skArc(sketch, "E1043", {"start": v(-111.14, 3.02) * mm, "mid": v(-111.01, 3.2) * mm, "end": v(-110.84, 3.3) * mm});
            skArc(sketch, "E1044", {"start": v(-110.84, 3.3) * mm, "mid": v(-110.6, 3.36) * mm, "end": v(-110.38, 3.34) * mm});
            skArc(sketch, "E1045", {"start": v(-110.38, 3.34) * mm, "mid": v(-110.1, 3.25) * mm, "end": v(-109.83, 3.11) * mm});
            skArc(sketch, "E1046", {"start": v(-109.83, 3.11) * mm, "mid": v(-109.1, 2.82) * mm, "end": v(-108.3, 2.78) * mm});
            skArc(sketch, "E1047", {"start": v(-108.3, 2.78) * mm, "mid": v(-107.83, 3.06) * mm, "end": v(-107.7, 3.6) * mm});
            skArc(sketch, "E1048", {"start": v(-107.7, 3.6) * mm, "mid": v(-108, 4.65) * mm, "end": v(-108.56, 5.58) * mm});
            skArc(sketch, "E1049", {"start": v(-108.56, 5.58) * mm, "mid": v(-109.49, 6.6) * mm, "end": v(-110.54, 7.5) * mm});
            skArc(sketch, "E1050", {"start": v(-110.54, 7.5) * mm, "mid": v(-111.47, 8.25) * mm, "end": v(-112.35, 9.04) * mm});
            skArc(sketch, "E1051", {"start": v(-112.35, 9.04) * mm, "mid": v(-112.83, 9.62) * mm, "end": v(-113.17, 10.29) * mm});
            skArc(sketch, "E1052", {"start": v(-113.17, 10.29) * mm, "mid": v(-113.3, 10.92) * mm, "end": v(-113.26, 11.56) * mm});
            skArc(sketch, "E1053", {"start": v(-113.26, 11.56) * mm, "mid": v(-113.02, 12.37) * mm, "end": v(-112.68, 13.14) * mm});
            skArc(sketch, "E1054", {"start": v(-112.68, 13.14) * mm, "mid": v(-112.34, 13.82) * mm, "end": v(-112.04, 14.52) * mm});
            skArc(sketch, "E1055", {"start": v(-112.04, 14.52) * mm, "mid": v(-111.93, 14.96) * mm, "end": v(-111.93, 15.42) * mm});
            skArc(sketch, "E1056", {"start": v(-111.93, 15.42) * mm, "mid": v(-112.05, 15.74) * mm, "end": v(-112.29, 15.98) * mm});
            skArc(sketch, "E1057", {"start": v(-112.29, 15.98) * mm, "mid": v(-112.68, 16.17) * mm, "end": v(-113.1, 16.28) * mm});
            skArc(sketch, "E1058", {"start": v(-113.1, 16.28) * mm, "mid": v(-113.23, 16.44) * mm, "end": v(-113.1, 16.58) * mm});
            skArc(sketch, "E1059", {"start": v(-113.1, 16.58) * mm, "mid": v(-108.43, 17.02) * mm, "end": v(-103.77, 17.44) * mm});
            skArc(sketch, "E1060", {"start": v(-103.77, 17.44) * mm, "mid": v(-98.67, 17.86) * mm, "end": v(-93.57, 18.25) * mm});
            skArc(sketch, "E1061", {"start": v(-93.57, 18.25) * mm, "mid": v(-89.1, 18.54) * mm, "end": v(-84.63, 18.77) * mm});
            skArc(sketch, "E1062", {"start": v(-84.63, 18.77) * mm, "mid": v(-83.25, 18.8) * mm, "end": v(-81.87, 18.72) * mm});
            skArc(sketch, "E1063", {"start": v(-81.87, 18.72) * mm, "mid": v(-80.21, 18.55) * mm, "end": v(-78.56, 18.33) * mm});
            skArc(sketch, "E1064", {"start": v(-78.56, 18.33) * mm, "mid": v(-76.9, 18.04) * mm, "end": v(-75.23, 17.69) * mm});
            skArc(sketch, "E1065", {"start": v(-75.23, 17.69) * mm, "mid": v(-73.83, 17.32) * mm, "end": v(-72.44, 16.87) * mm});
            skArc(sketch, "E1066", {"start": v(-123.95, 12.95) * mm, "mid": v(-124.07, 11.4) * mm, "end": v(-124.41, 9.87) * mm});
            skArc(sketch, "E1067", {"start": v(-124.41, 9.87) * mm, "mid": v(-124.94, 9) * mm, "end": v(-125.81, 8.49) * mm});
            skArc(sketch, "E1068", {"start": v(-125.81, 8.49) * mm, "mid": v(-126.8, 8.46) * mm, "end": v(-127.66, 8.93) * mm});
            skArc(sketch, "E1069", {"start": v(-127.66, 8.93) * mm, "mid": v(-128.67, 10.06) * mm, "end": v(-129.49, 11.33) * mm});
            skArc(sketch, "E1070", {"start": v(-129.49, 11.33) * mm, "mid": v(-130.16, 12.65) * mm, "end": v(-130.8, 13.99) * mm});
            skArc(sketch, "E1071", {"start": v(-130.8, 13.99) * mm, "mid": v(-130.93, 14.55) * mm, "end": v(-130.84, 15.13) * mm});
            skArc(sketch, "E1072", {"start": v(-130.84, 15.13) * mm, "mid": v(-130.54, 15.58) * mm, "end": v(-130.07, 15.85) * mm});
            skArc(sketch, "E1073", {"start": v(-130.07, 15.85) * mm, "mid": v(-128.86, 16.18) * mm, "end": v(-127.63, 16.45) * mm});
            skArc(sketch, "E1074", {"start": v(-127.64, 16.45) * mm, "mid": v(-126.97, 16.58) * mm, "end": v(-126.31, 16.72) * mm});
            skArc(sketch, "E1075", {"start": v(-126.31, 16.72) * mm, "mid": v(-125.74, 16.84) * mm, "end": v(-125.18, 16.98) * mm});
            skArc(sketch, "E1076", {"start": v(-125.18, 16.98) * mm, "mid": v(-124.7, 17.1) * mm, "end": v(-124.21, 17.22) * mm});
            skArc(sketch, "E1077", {"start": v(-124.21, 17.22) * mm, "mid": v(-124.14, 17.26) * mm, "end": v(-124.08, 17.32) * mm});
            skArc(sketch, "E1078", {"start": v(-124.08, 17.32) * mm, "mid": v(-124.05, 17.33) * mm, "end": v(-124.03, 17.3) * mm});
            skArc(sketch, "E1079", {"start": v(-124.03, 17.3) * mm, "mid": v(-124, 16.71) * mm, "end": v(-123.99, 16.12) * mm});
            skArc(sketch, "E1080", {"start": v(-123.99, 16.12) * mm, "mid": v(-123.97, 15.4) * mm, "end": v(-123.96, 14.7) * mm});
            skArc(sketch, "E1081", {"start": v(-123.96, 14.7) * mm, "mid": v(-123.95, 13.82) * mm, "end": v(-123.95, 12.95) * mm});
            skArc(sketch, "E1082", {"start": v(-147.5, 12.44) * mm, "mid": v(-147.57, 11.89) * mm, "end": v(-147.57, 11.34) * mm});
            skArc(sketch, "E1083", {"start": v(-147.57, 11.34) * mm, "mid": v(-147.48, 11) * mm, "end": v(-147.25, 10.76) * mm});
            skArc(sketch, "E1084", {"start": v(-147.25, 10.76) * mm, "mid": v(-146.91, 10.61) * mm, "end": v(-146.55, 10.61) * mm});
            skArc(sketch, "E1085", {"start": v(-146.55, 10.61) * mm, "mid": v(-145.94, 10.75) * mm, "end": v(-145.35, 10.95) * mm});
            skArc(sketch, "E1086", {"start": v(-145.35, 10.95) * mm, "mid": v(-144.78, 11.16) * mm, "end": v(-144.2, 11.33) * mm});
            skArc(sketch, "E1087", {"start": v(-144.2, 11.33) * mm, "mid": v(-143.92, 11.35) * mm, "end": v(-143.65, 11.27) * mm});
            skArc(sketch, "E1088", {"start": v(-143.65, 11.27) * mm, "mid": v(-143.52, 11.1) * mm, "end": v(-143.52, 10.9) * mm});
            skArc(sketch, "E1089", {"start": v(-143.52, 10.9) * mm, "mid": v(-143.69, 10.49) * mm, "end": v(-143.9, 10.1) * mm});
            skArc(sketch, "E1090", {"start": v(-143.9, 10.1) * mm, "mid": v(-144.2, 9.72) * mm, "end": v(-144.6, 9.43) * mm});
            skArc(sketch, "E1091", {"start": v(-144.6, 9.43) * mm, "mid": v(-145.1, 9.2) * mm, "end": v(-145.64, 9.05) * mm});
            skArc(sketch, "E1092", {"start": v(-145.64, 9.05) * mm, "mid": v(-146.28, 8.98) * mm, "end": v(-146.93, 9) * mm});
            skArc(sketch, "E1093", {"start": v(-146.93, 9) * mm, "mid": v(-147.64, 9.1) * mm, "end": v(-148.34, 9.27) * mm});
            skArc(sketch, "E1094", {"start": v(-148.34, 9.27) * mm, "mid": v(-149.75, 9.72) * mm, "end": v(-151.15, 10.2) * mm});
            skArc(sketch, "E1095", {"start": v(-151.15, 10.2) * mm, "mid": v(-151.6, 10.43) * mm, "end": v(-151.96, 10.8) * mm});
            skArc(sketch, "E1096", {"start": v(-151.96, 10.8) * mm, "mid": v(-152.13, 11.2) * mm, "end": v(-152.12, 11.64) * mm});
            skArc(sketch, "E1097", {"start": v(-152.12, 11.64) * mm, "mid": v(-151.83, 12.6) * mm, "end": v(-151.49, 13.56) * mm});
            skArc(sketch, "E1098", {"start": v(-151.49, 13.56) * mm, "mid": v(-151.01, 14.43) * mm, "end": v(-150.33, 15.16) * mm});
            skArc(sketch, "E1099", {"start": v(-150.33, 15.16) * mm, "mid": v(-149.6, 15.5) * mm, "end": v(-148.81, 15.47) * mm});
            skArc(sketch, "E1100", {"start": v(-148.81, 15.47) * mm, "mid": v(-148.11, 15.08) * mm, "end": v(-147.67, 14.4) * mm});
            skArc(sketch, "E1101", {"start": v(-147.67, 14.4) * mm, "mid": v(-147.46, 13.43) * mm, "end": v(-147.5, 12.44) * mm});
            skArc(sketch, "E1102", {"start": v(122.68, 8.38) * mm, "mid": v(122.8, 8.1) * mm, "end": v(122.86, 7.8) * mm});
            skArc(sketch, "E1103", {"start": v(122.86, 7.8) * mm, "mid": v(122.81, 7.54) * mm, "end": v(122.68, 7.3) * mm});
            skArc(sketch, "E1104", {"start": v(122.68, 7.3) * mm, "mid": v(122.43, 7.1) * mm, "end": v(122.14, 6.97) * mm});
            skArc(sketch, "E1105", {"start": v(122.14, 6.97) * mm, "mid": v(121.74, 6.89) * mm, "end": v(121.34, 6.86) * mm});
            skArc(sketch, "E1106", {"start": v(121.34, 6.86) * mm, "mid": v(120.86, 6.89) * mm, "end": v(120.4, 6.97) * mm});
            skArc(sketch, "E1107", {"start": v(120.4, 6.97) * mm, "mid": v(119.91, 7.11) * mm, "end": v(119.45, 7.3) * mm});
            skArc(sketch, "E1108", {"start": v(119.45, 7.3) * mm, "mid": v(119.03, 7.53) * mm, "end": v(118.64, 7.8) * mm});
            skArc(sketch, "E1109", {"start": v(118.64, 7.8) * mm, "mid": v(118.35, 8.07) * mm, "end": v(118.11, 8.38) * mm});
            skArc(sketch, "E1110", {"start": v(118.11, 8.38) * mm, "mid": v(117.99, 8.66) * mm, "end": v(117.94, 8.96) * mm});
            skArc(sketch, "E1111", {"start": v(117.94, 8.96) * mm, "mid": v(117.98, 9.23) * mm, "end": v(118.12, 9.46) * mm});
            skArc(sketch, "E1112", {"start": v(118.12, 9.46) * mm, "mid": v(118.36, 9.66) * mm, "end": v(118.65, 9.8) * mm});
            skArc(sketch, "E1113", {"start": v(118.65, 9.8) * mm, "mid": v(119.05, 9.88) * mm, "end": v(119.45, 9.9) * mm});
            skArc(sketch, "E1114", {"start": v(119.45, 9.9) * mm, "mid": v(119.93, 9.88) * mm, "end": v(120.4, 9.8) * mm});
            skArc(sketch, "E1115", {"start": v(120.4, 9.8) * mm, "mid": v(120.88, 9.65) * mm, "end": v(121.35, 9.46) * mm});
            skArc(sketch, "E1116", {"start": v(121.35, 9.46) * mm, "mid": v(121.76, 9.23) * mm, "end": v(122.15, 8.97) * mm});
            skArc(sketch, "E1117", {"start": v(122.15, 8.97) * mm, "mid": v(122.44, 8.7) * mm, "end": v(122.68, 8.38) * mm});
            skArc(sketch, "E1118", {"start": v(-149.35, 5.33) * mm, "mid": v(-149.96, 4.93) * mm, "end": v(-150.56, 4.5) * mm});
            skArc(sketch, "E1119", {"start": v(-150.56, 4.5) * mm, "mid": v(-150.67, 4.33) * mm, "end": v(-150.65, 4.13) * mm});
            skArc(sketch, "E1120", {"start": v(-150.65, 4.13) * mm, "mid": v(-150.5, 3.96) * mm, "end": v(-150.3, 3.88) * mm});
            skArc(sketch, "E1121", {"start": v(-150.3, 3.88) * mm, "mid": v(-149.48, 3.85) * mm, "end": v(-148.67, 3.83) * mm});
            skArc(sketch, "E1122", {"start": v(-148.67, 3.83) * mm, "mid": v(-147.93, 3.81) * mm, "end": v(-147.2, 3.75) * mm});
            skArc(sketch, "E1123", {"start": v(-147.2, 3.75) * mm, "mid": v(-146.91, 3.65) * mm, "end": v(-146.7, 3.43) * mm});
            skArc(sketch, "E1124", {"start": v(-146.7, 3.43) * mm, "mid": v(-146.63, 3.17) * mm, "end": v(-146.72, 2.91) * mm});
            skArc(sketch, "E1125", {"start": v(-146.72, 2.91) * mm, "mid": v(-147.1, 2.43) * mm, "end": v(-147.52, 1.98) * mm});
            skArc(sketch, "E1126", {"start": v(-147.52, 1.98) * mm, "mid": v(-147.98, 1.57) * mm, "end": v(-148.48, 1.21) * mm});
            skArc(sketch, "E1127", {"start": v(-148.48, 1.21) * mm, "mid": v(-148.88, 1.02) * mm, "end": v(-149.32, 0.94) * mm});
            skArc(sketch, "E1128", {"start": v(-149.32, 0.94) * mm, "mid": v(-149.75, 0.99) * mm, "end": v(-150.15, 1.15) * mm});
            skArc(sketch, "E1129", {"start": v(-150.15, 1.15) * mm, "mid": v(-150.62, 1.47) * mm, "end": v(-151.05, 1.85) * mm});
            skArc(sketch, "E1130", {"start": v(-151.05, 1.85) * mm, "mid": v(-151.58, 2.56) * mm, "end": v(-151.88, 3.38) * mm});
            skArc(sketch, "E1131", {"start": v(-151.88, 3.38) * mm, "mid": v(-151.93, 4.24) * mm, "end": v(-151.71, 5.08) * mm});
            skArc(sketch, "E1132", {"start": v(-151.71, 5.08) * mm, "mid": v(-151.25, 5.8) * mm, "end": v(-150.59, 6.37) * mm});
            skArc(sketch, "E1133", {"start": v(-150.59, 6.37) * mm, "mid": v(-149.77, 6.72) * mm, "end": v(-148.88, 6.83) * mm});
            skArc(sketch, "E1134", {"start": v(-148.88, 6.83) * mm, "mid": v(-148.6, 6.8) * mm, "end": v(-148.33, 6.71) * mm});
            skArc(sketch, "E1135", {"start": v(-148.33, 6.71) * mm, "mid": v(-148.2, 6.59) * mm, "end": v(-148.2, 6.41) * mm});
            skArc(sketch, "E1136", {"start": v(-148.2, 6.41) * mm, "mid": v(-148.32, 6.16) * mm, "end": v(-148.5, 5.95) * mm});
            skArc(sketch, "E1137", {"start": v(-148.5, 5.95) * mm, "mid": v(-148.92, 5.63) * mm, "end": v(-149.35, 5.33) * mm});
            skArc(sketch, "E1138", {"start": v(-125.57, 4.17) * mm, "mid": v(-125.17, 3.8) * mm, "end": v(-124.9, 3.34) * mm});
            skArc(sketch, "E1139", {"start": v(-124.9, 3.34) * mm, "mid": v(-124.73, 2.73) * mm, "end": v(-124.68, 2.1) * mm});
            skArc(sketch, "E1140", {"start": v(-124.68, 2.1) * mm, "mid": v(-124.75, 1.22) * mm, "end": v(-124.92, 0.34) * mm});
            skArc(sketch, "E1141", {"start": v(-124.92, 0.34) * mm, "mid": v(-125.27, -0.93) * mm, "end": v(-125.68, -2.2) * mm});
            skArc(sketch, "E1142", {"start": v(-125.68, -2.2) * mm, "mid": v(-126.2, -3.67) * mm, "end": v(-126.74, -5.14) * mm});
            skArc(sketch, "E1143", {"start": v(-126.74, -5.14) * mm, "mid": v(-126.98, -5.6) * mm, "end": v(-127.35, -5.98) * mm});
            skArc(sketch, "E1144", {"start": v(-127.35, -5.98) * mm, "mid": v(-127.65, -6.06) * mm, "end": v(-127.91, -5.88) * mm});
            skArc(sketch, "E1145", {"start": v(-127.91, -5.88) * mm, "mid": v(-128.28, -5.21) * mm, "end": v(-128.6, -4.51) * mm});
            skArc(sketch, "E1146", {"start": v(-128.6, -4.51) * mm, "mid": v(-128.79, -3.92) * mm, "end": v(-128.92, -3.31) * mm});
            skArc(sketch, "E1147", {"start": v(-128.92, -3.31) * mm, "mid": v(-128.97, -2.79) * mm, "end": v(-128.94, -2.26) * mm});
            skArc(sketch, "E1148", {"start": v(-128.94, -2.26) * mm, "mid": v(-128.84, -1.85) * mm, "end": v(-128.65, -1.48) * mm});
            skArc(sketch, "E1149", {"start": v(-128.65, -1.48) * mm, "mid": v(-128.42, -1.21) * mm, "end": v(-128.1, -1.05) * mm});
            skArc(sketch, "E1150", {"start": v(-128.1, -1.05) * mm, "mid": v(-127.42, -0.67) * mm, "end": v(-126.93, -0.07) * mm});
            skArc(sketch, "E1151", {"start": v(-126.93, -0.07) * mm, "mid": v(-126.62, 0.72) * mm, "end": v(-126.54, 1.57) * mm});
            skArc(sketch, "E1152", {"start": v(-126.54, 1.57) * mm, "mid": v(-126.71, 2.45) * mm, "end": v(-127.1, 3.26) * mm});
            skArc(sketch, "E1153", {"start": v(-127.1, 3.26) * mm, "mid": v(-127.67, 3.9) * mm, "end": v(-128.4, 4.32) * mm});
            skArc(sketch, "E1154", {"start": v(-128.4, 4.32) * mm, "mid": v(-128.73, 4.47) * mm, "end": v(-129.05, 4.63) * mm});
            skArc(sketch, "E1155", {"start": v(-129.05, 4.63) * mm, "mid": v(-129.2, 4.74) * mm, "end": v(-129.3, 4.9) * mm});
            skArc(sketch, "E1156", {"start": v(-129.3, 4.9) * mm, "mid": v(-129.3, 5.01) * mm, "end": v(-129.21, 5.1) * mm});
            skArc(sketch, "E1157", {"start": v(-129.21, 5.1) * mm, "mid": v(-129, 5.16) * mm, "end": v(-128.78, 5.2) * mm});
            skArc(sketch, "E1158", {"start": v(-128.78, 5.2) * mm, "mid": v(-128.42, 5.2) * mm, "end": v(-128.07, 5.15) * mm});
            skArc(sketch, "E1159", {"start": v(-128.07, 5.15) * mm, "mid": v(-127.64, 5.05) * mm, "end": v(-127.2, 4.93) * mm});
            skArc(sketch, "E1160", {"start": v(-127.2, 4.93) * mm, "mid": v(-126.76, 4.77) * mm, "end": v(-126.33, 4.59) * mm});
            skArc(sketch, "E1161", {"start": v(-126.33, 4.59) * mm, "mid": v(-125.94, 4.4) * mm, "end": v(-125.57, 4.17) * mm});
            skArc(sketch, "E1162", {"start": v(-65.87, -1.9) * mm, "mid": v(-64.53, -3.38) * mm, "end": v(-63.17, -4.85) * mm});
            skArc(sketch, "E1163", {"start": v(-63.17, -4.85) * mm, "mid": v(-62.61, -5.35) * mm, "end": v(-61.99, -5.76) * mm});
            skArc(sketch, "E1164", {"start": v(-61.99, -5.76) * mm, "mid": v(-61.7, -5.76) * mm, "end": v(-61.55, -5.5) * mm});
            skArc(sketch, "E1165", {"start": v(-61.55, -5.5) * mm, "mid": v(-61.59, -4.84) * mm, "end": v(-61.72, -4.18) * mm});
            skLineSegment(sketch, "E1166", {"start": v(-61.72, -4.18) * mm, "end": v(-62.7, -0.74) * mm});
            skLineSegment(sketch, "E1167", {"start": v(-62.7, -0.74) * mm, "end": v(-57.25, -3.95) * mm});
            skArc(sketch, "E1168", {"start": v(-57.25, -3.95) * mm, "mid": v(-55.32, -5.15) * mm, "end": v(-53.44, -6.42) * mm});
            skArc(sketch, "E1169", {"start": v(-53.44, -6.42) * mm, "mid": v(-52.15, -7.44) * mm, "end": v(-50.97, -8.6) * mm});
            skArc(sketch, "E1170", {"start": v(-50.97, -8.6) * mm, "mid": v(-50.93, -8.95) * mm, "end": v(-51.25, -9.12) * mm});
            skArc(sketch, "E1171", {"start": v(-51.25, -9.12) * mm, "mid": v(-52.18, -8.9) * mm, "end": v(-53.06, -8.53) * mm});
            skArc(sketch, "E1172", {"start": v(-53.06, -8.53) * mm, "mid": v(-53.7, -8.23) * mm, "end": v(-54.34, -7.98) * mm});
            skArc(sketch, "E1173", {"start": v(-54.34, -7.98) * mm, "mid": v(-54.93, -7.82) * mm, "end": v(-55.54, -7.73) * mm});
            skArc(sketch, "E1174", {"start": v(-55.54, -7.73) * mm, "mid": v(-56.01, -7.73) * mm, "end": v(-56.49, -7.8) * mm});
            skArc(sketch, "E1175", {"start": v(-56.49, -7.8) * mm, "mid": v(-56.8, -7.95) * mm, "end": v(-57.04, -8.2) * mm});
            skArc(sketch, "E1176", {"start": v(-57.04, -8.2) * mm, "mid": v(-57.26, -8.94) * mm, "end": v(-57.07, -9.67) * mm});
            skArc(sketch, "E1177", {"start": v(-57.07, -9.67) * mm, "mid": v(-56.44, -10.59) * mm, "end": v(-55.64, -11.37) * mm});
            skArc(sketch, "E1178", {"start": v(-55.64, -11.37) * mm, "mid": v(-54.68, -12.02) * mm, "end": v(-53.63, -12.49) * mm});
            skArc(sketch, "E1179", {"start": v(-53.63, -12.49) * mm, "mid": v(-52.8, -12.58) * mm, "end": v(-52, -12.3) * mm});
            skArc(sketch, "E1180", {"start": v(-52, -12.3) * mm, "mid": v(-51.65, -12.16) * mm, "end": v(-51.27, -12.13) * mm});
            skArc(sketch, "E1181", {"start": v(-51.27, -12.13) * mm, "mid": v(-50.78, -12.2) * mm, "end": v(-50.3, -12.34) * mm});
            skArc(sketch, "E1182", {"start": v(-50.3, -12.34) * mm, "mid": v(-49.74, -12.59) * mm, "end": v(-49.23, -12.89) * mm});
            skArc(sketch, "E1183", {"start": v(-49.23, -12.89) * mm, "mid": v(-48.71, -13.27) * mm, "end": v(-48.24, -13.7) * mm});
            skArc(sketch, "E1184", {"start": v(-48.24, -13.7) * mm, "mid": v(-47.75, -14.16) * mm, "end": v(-47.24, -14.58) * mm});
            skArc(sketch, "E1185", {"start": v(-47.24, -14.58) * mm, "mid": v(-46.7, -14.97) * mm, "end": v(-46.13, -15.33) * mm});
            skArc(sketch, "E1186", {"start": v(-46.13, -15.33) * mm, "mid": v(-45.62, -15.6) * mm, "end": v(-45.1, -15.85) * mm});
            skArc(sketch, "E1187", {"start": v(-45.1, -15.85) * mm, "mid": v(-44.7, -15.96) * mm, "end": v(-44.3, -16) * mm});
            skArc(sketch, "E1188", {"start": v(-44.3, -16) * mm, "mid": v(-43.98, -16.04) * mm, "end": v(-43.68, -16.16) * mm});
            skArc(sketch, "E1189", {"start": v(-43.68, -16.16) * mm, "mid": v(-43.4, -16.37) * mm, "end": v(-43.15, -16.62) * mm});
            skArc(sketch, "E1190", {"start": v(-43.15, -16.62) * mm, "mid": v(-42.94, -16.95) * mm, "end": v(-42.8, -17.3) * mm});
            skArc(sketch, "E1191", {"start": v(-42.8, -17.3) * mm, "mid": v(-42.7, -17.7) * mm, "end": v(-42.67, -18.11) * mm});
            skArc(sketch, "E1192", {"start": v(-42.67, -18.11) * mm, "mid": v(-42.6, -18.56) * mm, "end": v(-42.42, -18.98) * mm});
            skArc(sketch, "E1193", {"start": v(-42.42, -18.98) * mm, "mid": v(-42.09, -19.45) * mm, "end": v(-41.68, -19.86) * mm});
            skArc(sketch, "E1194", {"start": v(-41.68, -19.86) * mm, "mid": v(-41.16, -20.27) * mm, "end": v(-40.6, -20.6) * mm});
            skArc(sketch, "E1195", {"start": v(-40.6, -20.6) * mm, "mid": v(-39.97, -20.89) * mm, "end": v(-39.3, -21.1) * mm});
            skArc(sketch, "E1196", {"start": v(-39.3, -21.1) * mm, "mid": v(-38.7, -21.28) * mm, "end": v(-38.1, -21.5) * mm});
            skArc(sketch, "E1197", {"start": v(-38.1, -21.5) * mm, "mid": v(-37.64, -21.73) * mm, "end": v(-37.23, -22.01) * mm});
            skArc(sketch, "E1198", {"start": v(-37.23, -22.01) * mm, "mid": v(-37, -22.25) * mm, "end": v(-36.86, -22.53) * mm});
            skArc(sketch, "E1199", {"start": v(-36.86, -22.53) * mm, "mid": v(-36.84, -22.77) * mm, "end": v(-36.95, -22.98) * mm});
            skArc(sketch, "E1200", {"start": v(-36.95, -22.98) * mm, "mid": v(-37.3, -23.18) * mm, "end": v(-37.7, -23.18) * mm});
            skArc(sketch, "E1201", {"start": v(-37.7, -23.18) * mm, "mid": v(-38.69, -22.87) * mm, "end": v(-39.67, -22.52) * mm});
            skArc(sketch, "E1202", {"start": v(-39.67, -22.52) * mm, "mid": v(-40.9, -22.02) * mm, "end": v(-42.1, -21.46) * mm});
            skArc(sketch, "E1203", {"start": v(-42.1, -21.46) * mm, "mid": v(-43.45, -20.75) * mm, "end": v(-44.78, -20) * mm});
            skArc(sketch, "E1204", {"start": v(-44.78, -20) * mm, "mid": v(-47.95, -18.16) * mm, "end": v(-51.13, -16.36) * mm});
            skArc(sketch, "E1205", {"start": v(-51.13, -16.36) * mm, "mid": v(-51.86, -16.14) * mm, "end": v(-52.62, -16.25) * mm});
            skArc(sketch, "E1206", {"start": v(-52.62, -16.25) * mm, "mid": v(-52.94, -16.62) * mm, "end": v(-52.8, -17.09) * mm});
            skArc(sketch, "E1207", {"start": v(-52.8, -17.09) * mm, "mid": v(-50.58, -19.22) * mm, "end": v(-48.32, -21.32) * mm});
            skArc(sketch, "E1208", {"start": v(-48.32, -21.32) * mm, "mid": v(-47.2, -22.34) * mm, "end": v(-46.03, -23.34) * mm});
            skArc(sketch, "E1209", {"start": v(-46.03, -23.34) * mm, "mid": v(-45, -24.18) * mm, "end": v(-43.93, -24.99) * mm});
            skArc(sketch, "E1210", {"start": v(-43.93, -24.99) * mm, "mid": v(-43.04, -25.62) * mm, "end": v(-42.14, -26.24) * mm});
            skArc(sketch, "E1211", {"start": v(-42.14, -26.24) * mm, "mid": v(-41.81, -26.36) * mm, "end": v(-41.47, -26.35) * mm});
            skArc(sketch, "E1212", {"start": v(-41.47, -26.35) * mm, "mid": v(-40.48, -26.22) * mm, "end": v(-39.49, -26.35) * mm});
            skArc(sketch, "E1213", {"start": v(-39.49, -26.35) * mm, "mid": v(-38.1, -26.79) * mm, "end": v(-36.76, -27.34) * mm});
            skArc(sketch, "E1214", {"start": v(-36.76, -27.34) * mm, "mid": v(-35.6, -27.95) * mm, "end": v(-34.5, -28.66) * mm});
            skArc(sketch, "E1215", {"start": v(-34.5, -28.66) * mm, "mid": v(-34.18, -29.14) * mm, "end": v(-34.28, -29.7) * mm});
            skArc(sketch, "E1216", {"start": v(-34.28, -29.7) * mm, "mid": v(-34.36, -30.3) * mm, "end": v(-33.96, -30.74) * mm});
            skArc(sketch, "E1217", {"start": v(-33.96, -30.74) * mm, "mid": v(-31.07, -32.03) * mm, "end": v(-28.15, -33.26) * mm});
            skArc(sketch, "E1218", {"start": v(-28.15, -33.26) * mm, "mid": v(-25.13, -34.44) * mm, "end": v(-22.06, -35.51) * mm});
            skArc(sketch, "E1219", {"start": v(-22.06, -35.51) * mm, "mid": v(-19.66, -36.22) * mm, "end": v(-17.2, -36.73) * mm});
            skArc(sketch, "E1220", {"start": v(-17.2, -36.73) * mm, "mid": v(-16.7, -36.86) * mm, "end": v(-16.21, -37.05) * mm});
            skArc(sketch, "E1221", {"start": v(-16.21, -37.05) * mm, "mid": v(-15.38, -37.46) * mm, "end": v(-14.57, -37.9) * mm});
            skArc(sketch, "E1222", {"start": v(-14.57, -37.9) * mm, "mid": v(-13.63, -38.44) * mm, "end": v(-12.7, -39) * mm});
            skArc(sketch, "E1223", {"start": v(-12.7, -39) * mm, "mid": v(-11.77, -39.62) * mm, "end": v(-10.85, -40.26) * mm});
            skArc(sketch, "E1224", {"start": v(-10.85, -40.26) * mm, "mid": v(-9.5, -41.18) * mm, "end": v(-8.14, -42.07) * mm});
            skArc(sketch, "E1225", {"start": v(-8.14, -42.07) * mm, "mid": v(-7.44, -42.4) * mm, "end": v(-6.68, -42.58) * mm});
            skArc(sketch, "E1226", {"start": v(-6.68, -42.58) * mm, "mid": v(-6.04, -42.54) * mm, "end": v(-5.45, -42.29) * mm});
            skArc(sketch, "E1227", {"start": v(-5.45, -42.29) * mm, "mid": v(-4.66, -41.71) * mm, "end": v(-3.93, -41.05) * mm});
            skArc(sketch, "E1228", {"start": v(-3.93, -41.05) * mm, "mid": v(-3.46, -40.55) * mm, "end": v(-3.01, -40.03) * mm});
            skArc(sketch, "E1229", {"start": v(-3.01, -40.03) * mm, "mid": v(-2.6, -39.5) * mm, "end": v(-2.23, -38.94) * mm});
            skArc(sketch, "E1230", {"start": v(-2.23, -38.94) * mm, "mid": v(-1.94, -38.45) * mm, "end": v(-1.68, -37.95) * mm});
            skArc(sketch, "E1231", {"start": v(-1.68, -37.95) * mm, "mid": v(-1.56, -37.61) * mm, "end": v(-1.52, -37.25) * mm});
            skArc(sketch, "E1232", {"start": v(-1.52, -37.25) * mm, "mid": v(-1.41, -36.92) * mm, "end": v(-1.13, -36.7) * mm});
            skArc(sketch, "E1233", {"start": v(-1.13, -36.7) * mm, "mid": v(-0.27, -36.46) * mm, "end": v(0.6, -36.26) * mm});
            skArc(sketch, "E1234", {"start": v(0.6, -36.26) * mm, "mid": v(1.77, -36.06) * mm, "end": v(2.94, -35.94) * mm});
            skArc(sketch, "E1235", {"start": v(2.94, -35.94) * mm, "mid": v(4.33, -35.85) * mm, "end": v(5.72, -35.82) * mm});
            skArc(sketch, "E1236", {"start": v(5.72, -35.82) * mm, "mid": v(7.3, -35.8) * mm, "end": v(8.88, -35.77) * mm});
            skArc(sketch, "E1237", {"start": v(8.88, -35.77) * mm, "mid": v(10.64, -35.74) * mm, "end": v(12.4, -35.69) * mm});
            skArc(sketch, "E1238", {"start": v(12.4, -35.69) * mm, "mid": v(14.06, -35.63) * mm, "end": v(15.73, -35.57) * mm});
            skArc(sketch, "E1239", {"start": v(15.73, -35.57) * mm, "mid": v(17.01, -35.52) * mm, "end": v(18.29, -35.45) * mm});
            skArc(sketch, "E1240", {"start": v(18.29, -35.45) * mm, "mid": v(19.44, -35.4) * mm, "end": v(20.6, -35.42) * mm});
            skArc(sketch, "E1241", {"start": v(20.6, -35.42) * mm, "mid": v(21.87, -35.48) * mm, "end": v(23.13, -35.6) * mm});
            skArc(sketch, "E1242", {"start": v(23.13, -35.6) * mm, "mid": v(24.32, -35.74) * mm, "end": v(25.5, -35.94) * mm});
            skArc(sketch, "E1243", {"start": v(25.5, -35.94) * mm, "mid": v(26.4, -36.14) * mm, "end": v(27.28, -36.4) * mm});
            skArc(sketch, "E1244", {"start": v(27.28, -36.4) * mm, "mid": v(28.29, -36.74) * mm, "end": v(29.3, -37.05) * mm});
            skArc(sketch, "E1245", {"start": v(29.3, -37.05) * mm, "mid": v(29.7, -37.09) * mm, "end": v(30.09, -36.97) * mm});
            skArc(sketch, "E1246", {"start": v(30.09, -36.97) * mm, "mid": v(30.3, -36.75) * mm, "end": v(30.34, -36.44) * mm});
            skArc(sketch, "E1247", {"start": v(30.34, -36.44) * mm, "mid": v(30.16, -35.74) * mm, "end": v(29.93, -35.06) * mm});
            skArc(sketch, "E1248", {"start": v(29.93, -35.06) * mm, "mid": v(29.72, -34.45) * mm, "end": v(29.54, -33.82) * mm});
            skArc(sketch, "E1249", {"start": v(29.54, -33.82) * mm, "mid": v(29.54, -33.5) * mm, "end": v(29.66, -33.22) * mm});
            skArc(sketch, "E1250", {"start": v(29.66, -33.22) * mm, "mid": v(29.88, -33.04) * mm, "end": v(30.16, -33.01) * mm});
            skArc(sketch, "E1251", {"start": v(30.16, -33.01) * mm, "mid": v(30.7, -33.13) * mm, "end": v(31.2, -33.3) * mm});
            skArc(sketch, "E1252", {"start": v(31.2, -33.3) * mm, "mid": v(33.59, -34.07) * mm, "end": v(36.04, -34.57) * mm});
            skArc(sketch, "E1253", {"start": v(36.04, -34.57) * mm, "mid": v(39.35, -34.96) * mm, "end": v(42.67, -35.2) * mm});
            skArc(sketch, "E1254", {"start": v(42.67, -35.2) * mm, "mid": v(46.06, -35.28) * mm, "end": v(49.45, -35.2) * mm});
            skArc(sketch, "E1255", {"start": v(49.45, -35.2) * mm, "mid": v(52.17, -34.94) * mm, "end": v(54.86, -34.44) * mm});
            skArc(sketch, "E1256", {"start": v(54.86, -34.44) * mm, "mid": v(58, -33.9) * mm, "end": v(61.19, -33.74) * mm});
            skArc(sketch, "E1257", {"start": v(61.19, -33.74) * mm, "mid": v(66.33, -33.89) * mm, "end": v(71.46, -34.2) * mm});
            skArc(sketch, "E1258", {"start": v(71.46, -34.2) * mm, "mid": v(76.62, -34.67) * mm, "end": v(81.77, -35.31) * mm});
            skArc(sketch, "E1259", {"start": v(81.77, -35.31) * mm, "mid": v(85.12, -35.97) * mm, "end": v(88.4, -36.98) * mm});
            skArc(sketch, "E1260", {"start": v(88.4, -36.98) * mm, "mid": v(88.9, -37.14) * mm, "end": v(89.4, -37.28) * mm});
            skArc(sketch, "E1261", {"start": v(89.4, -37.28) * mm, "mid": v(89.98, -37.4) * mm, "end": v(90.57, -37.48) * mm});
            skArc(sketch, "E1262", {"start": v(90.57, -37.48) * mm, "mid": v(91.13, -37.54) * mm, "end": v(91.69, -37.57) * mm});
            skArc(sketch, "E1263", {"start": v(91.69, -37.57) * mm, "mid": v(92.14, -37.56) * mm, "end": v(92.58, -37.51) * mm});
            skArc(sketch, "E1264", {"start": v(92.58, -37.51) * mm, "mid": v(92.95, -37.48) * mm, "end": v(93.31, -37.5) * mm});
            skArc(sketch, "E1265", {"start": v(93.31, -37.5) * mm, "mid": v(93.63, -37.6) * mm, "end": v(93.93, -37.74) * mm});
            skArc(sketch, "E1266", {"start": v(93.93, -37.74) * mm, "mid": v(94.16, -37.93) * mm, "end": v(94.34, -38.17) * mm});
            skArc(sketch, "E1267", {"start": v(94.34, -38.17) * mm, "mid": v(94.45, -38.44) * mm, "end": v(94.49, -38.72) * mm});
            skArc(sketch, "E1268", {"start": v(94.49, -38.72) * mm, "mid": v(94.36, -39.1) * mm, "end": v(94.03, -39.3) * mm});
            skArc(sketch, "E1269", {"start": v(94.03, -39.3) * mm, "mid": v(93.2, -39.47) * mm, "end": v(92.37, -39.56) * mm});
            skArc(sketch, "E1270", {"start": v(92.37, -39.56) * mm, "mid": v(91.12, -39.58) * mm, "end": v(89.86, -39.53) * mm});
            skArc(sketch, "E1271", {"start": v(89.86, -39.53) * mm, "mid": v(88.17, -39.37) * mm, "end": v(86.49, -39.17) * mm});
            skArc(sketch, "E1272", {"start": v(86.49, -39.17) * mm, "mid": v(81, -38.58) * mm, "end": v(75.48, -38.27) * mm});
            skArc(sketch, "E1273", {"start": v(75.48, -38.27) * mm, "mid": v(69.65, -38.2) * mm, "end": v(63.82, -38.4) * mm});
            skArc(sketch, "E1274", {"start": v(63.82, -38.4) * mm, "mid": v(58.23, -38.84) * mm, "end": v(52.67, -39.52) * mm});
            skArc(sketch, "E1275", {"start": v(52.67, -39.52) * mm, "mid": v(47.93, -40.37) * mm, "end": v(43.27, -41.56) * mm});
            skArc(sketch, "E1276", {"start": v(43.27, -41.56) * mm, "mid": v(37, -43.07) * mm, "end": v(30.6, -43.98) * mm});
            skArc(sketch, "E1277", {"start": v(30.6, -43.98) * mm, "mid": v(20.07, -44.86) * mm, "end": v(9.52, -45.5) * mm});
            skArc(sketch, "E1278", {"start": v(9.52, -45.5) * mm, "mid": v(-1.11, -45.88) * mm, "end": v(-11.75, -46) * mm});
            skArc(sketch, "E1279", {"start": v(-11.75, -46) * mm, "mid": v(-18.68, -45.72) * mm, "end": v(-25.57, -44.87) * mm});
            skArc(sketch, "E1280", {"start": v(-25.57, -44.87) * mm, "mid": v(-29.34, -44.41) * mm, "end": v(-33.14, -44.29) * mm});
            skArc(sketch, "E1281", {"start": v(-33.14, -44.29) * mm, "mid": v(-38.26, -44.42) * mm, "end": v(-43.37, -44.75) * mm});
            skArc(sketch, "E1282", {"start": v(-43.37, -44.75) * mm, "mid": v(-48.78, -45.28) * mm, "end": v(-54.16, -46.01) * mm});
            skArc(sketch, "E1283", {"start": v(-54.16, -46.01) * mm, "mid": v(-58.93, -46.87) * mm, "end": v(-63.64, -47.97) * mm});
            skArc(sketch, "E1284", {"start": v(-63.64, -47.97) * mm, "mid": v(-64.79, -48.22) * mm, "end": v(-65.95, -48.38) * mm});
            skArc(sketch, "E1285", {"start": v(-65.95, -48.38) * mm, "mid": v(-67.17, -48.47) * mm, "end": v(-68.4, -48.48) * mm});
            skArc(sketch, "E1286", {"start": v(-68.4, -48.48) * mm, "mid": v(-69.57, -48.4) * mm, "end": v(-70.75, -48.25) * mm});
            skArc(sketch, "E1287", {"start": v(-70.75, -48.25) * mm, "mid": v(-71.78, -48.02) * mm, "end": v(-72.79, -47.7) * mm});
            skArc(sketch, "E1288", {"start": v(-72.79, -47.7) * mm, "mid": v(-74.19, -47.3) * mm, "end": v(-75.64, -47.12) * mm});
            skArc(sketch, "E1289", {"start": v(-75.64, -47.12) * mm, "mid": v(-77.65, -47.08) * mm, "end": v(-79.67, -47.16) * mm});
            skArc(sketch, "E1290", {"start": v(-79.67, -47.16) * mm, "mid": v(-82.47, -47.42) * mm, "end": v(-85.27, -47.8) * mm});
            skArc(sketch, "E1291", {"start": v(-85.27, -47.8) * mm, "mid": v(-89.33, -48.45) * mm, "end": v(-93.38, -49.17) * mm});
            skArc(sketch, "E1292", {"start": v(-93.38, -49.17) * mm, "mid": v(-96.55, -49.72) * mm, "end": v(-99.73, -50.22) * mm});
            skArc(sketch, "E1293", {"start": v(-99.73, -50.22) * mm, "mid": v(-102.47, -50.6) * mm, "end": v(-105.21, -50.9) * mm});
            skArc(sketch, "E1294", {"start": v(-105.21, -50.9) * mm, "mid": v(-107.5, -51.1) * mm, "end": v(-109.77, -51.29) * mm});
            skArc(sketch, "E1295", {"start": v(-109.77, -51.29) * mm, "mid": v(-110.25, -51.19) * mm, "end": v(-110.61, -50.85) * mm});
            skArc(sketch, "E1296", {"start": v(-110.61, -50.85) * mm, "mid": v(-110.67, -50.58) * mm, "end": v(-110.53, -50.34) * mm});
            skArc(sketch, "E1297", {"start": v(-110.53, -50.34) * mm, "mid": v(-110.14, -50.08) * mm, "end": v(-109.71, -49.9) * mm});
            skArc(sketch, "E1298", {"start": v(-109.71, -49.9) * mm, "mid": v(-109, -49.7) * mm, "end": v(-108.27, -49.57) * mm});
            skArc(sketch, "E1299", {"start": v(-108.27, -49.57) * mm, "mid": v(-107.33, -49.49) * mm, "end": v(-106.39, -49.45) * mm});
            skArc(sketch, "E1300", {"start": v(-106.39, -49.45) * mm, "mid": v(-104.66, -49.42) * mm, "end": v(-102.93, -49.37) * mm});
            skArc(sketch, "E1301", {"start": v(-102.93, -49.37) * mm, "mid": v(-102.64, -49.29) * mm, "end": v(-102.42, -49.08) * mm});
            skArc(sketch, "E1302", {"start": v(-102.42, -49.08) * mm, "mid": v(-102.36, -48.83) * mm, "end": v(-102.5, -48.61) * mm});
            skArc(sketch, "E1303", {"start": v(-102.5, -48.61) * mm, "mid": v(-103.63, -47.79) * mm, "end": v(-104.78, -46.98) * mm});
            skArc(sketch, "E1304", {"start": v(-104.78, -46.98) * mm, "mid": v(-106.25, -45.86) * mm, "end": v(-107.62, -44.62) * mm});
            skArc(sketch, "E1305", {"start": v(-107.62, -44.62) * mm, "mid": v(-107.95, -43.9) * mm, "end": v(-107.72, -43.16) * mm});
            skArc(sketch, "E1306", {"start": v(-107.72, -43.16) * mm, "mid": v(-106.91, -42.44) * mm, "end": v(-105.9, -42.05) * mm});
            skArc(sketch, "E1307", {"start": v(-105.9, -42.05) * mm, "mid": v(-103.06, -41.55) * mm, "end": v(-100.2, -41.12) * mm});
            skArc(sketch, "E1308", {"start": v(-100.2, -41.12) * mm, "mid": v(-96.81, -40.63) * mm, "end": v(-93.43, -40.06) * mm});
            skArc(sketch, "E1309", {"start": v(-93.43, -40.06) * mm, "mid": v(-91.81, -39.63) * mm, "end": v(-90.28, -38.97) * mm});
            skArc(sketch, "E1310", {"start": v(-90.28, -38.97) * mm, "mid": v(-89.72, -38.4) * mm, "end": v(-89.58, -37.62) * mm});
            skArc(sketch, "E1311", {"start": v(-89.58, -37.62) * mm, "mid": v(-89.88, -36.7) * mm, "end": v(-90.5, -35.97) * mm});
            skArc(sketch, "E1312", {"start": v(-90.5, -35.97) * mm, "mid": v(-90.93, -35.56) * mm, "end": v(-91.33, -35.1) * mm});
            skArc(sketch, "E1313", {"start": v(-91.33, -35.1) * mm, "mid": v(-91.67, -34.62) * mm, "end": v(-91.95, -34.1) * mm});
            skArc(sketch, "E1314", {"start": v(-91.95, -34.1) * mm, "mid": v(-92.15, -33.6) * mm, "end": v(-92.28, -33.1) * mm});
            skArc(sketch, "E1315", {"start": v(-92.28, -33.1) * mm, "mid": v(-92.3, -32.68) * mm, "end": v(-92.24, -32.27) * mm});
            skArc(sketch, "E1316", {"start": v(-92.24, -32.27) * mm, "mid": v(-92.1, -31.8) * mm, "end": v(-91.97, -31.32) * mm});
            skArc(sketch, "E1317", {"start": v(-91.97, -31.32) * mm, "mid": v(-91.78, -30.55) * mm, "end": v(-91.59, -29.8) * mm});
            skArc(sketch, "E1318", {"start": v(-91.59, -29.8) * mm, "mid": v(-91.38, -28.93) * mm, "end": v(-91.18, -28.06) * mm});
            skArc(sketch, "E1319", {"start": v(-91.18, -28.06) * mm, "mid": v(-90.98, -27.2) * mm, "end": v(-90.79, -26.34) * mm});
            skArc(sketch, "E1320", {"start": v(-90.79, -26.34) * mm, "mid": v(-90.54, -25.36) * mm, "end": v(-90.22, -24.4) * mm});
            skArc(sketch, "E1321", {"start": v(-90.22, -24.4) * mm, "mid": v(-89.92, -23.82) * mm, "end": v(-89.5, -23.31) * mm});
            skArc(sketch, "E1322", {"start": v(-89.5, -23.31) * mm, "mid": v(-89.05, -23.02) * mm, "end": v(-88.53, -22.89) * mm});
            skArc(sketch, "E1323", {"start": v(-88.53, -22.89) * mm, "mid": v(-87.87, -22.9) * mm, "end": v(-87.23, -23.04) * mm});
            skArc(sketch, "E1324", {"start": v(-87.23, -23.04) * mm, "mid": v(-86.95, -23.07) * mm, "end": v(-86.67, -23) * mm});
            skArc(sketch, "E1325", {"start": v(-86.67, -23) * mm, "mid": v(-86.54, -22.86) * mm, "end": v(-86.57, -22.67) * mm});
            skArc(sketch, "E1326", {"start": v(-86.57, -22.67) * mm, "mid": v(-86.9, -22.22) * mm, "end": v(-87.29, -21.82) * mm});
            skArc(sketch, "E1327", {"start": v(-87.29, -21.82) * mm, "mid": v(-88.02, -21.18) * mm, "end": v(-88.77, -20.57) * mm});
            skArc(sketch, "E1328", {"start": v(-88.77, -20.57) * mm, "mid": v(-89.6, -19.87) * mm, "end": v(-90.38, -19.12) * mm});
            skArc(sketch, "E1329", {"start": v(-90.38, -19.12) * mm, "mid": v(-91.09, -18.32) * mm, "end": v(-91.73, -17.47) * mm});
            skArc(sketch, "E1330", {"start": v(-91.73, -17.47) * mm, "mid": v(-92.24, -16.7) * mm, "end": v(-92.68, -15.89) * mm});
            skArc(sketch, "E1331", {"start": v(-92.68, -15.89) * mm, "mid": v(-92.9, -15.29) * mm, "end": v(-92.96, -14.66) * mm});
            skArc(sketch, "E1332", {"start": v(-92.96, -14.66) * mm, "mid": v(-93, -14.08) * mm, "end": v(-93.1, -13.52) * mm});
            skArc(sketch, "E1333", {"start": v(-93.1, -13.52) * mm, "mid": v(-93.28, -12.89) * mm, "end": v(-93.5, -12.27) * mm});
            skArc(sketch, "E1334", {"start": v(-93.5, -12.27) * mm, "mid": v(-93.77, -11.68) * mm, "end": v(-94.1, -11.1) * mm});
            skArc(sketch, "E1335", {"start": v(-94.1, -11.1) * mm, "mid": v(-94.42, -10.64) * mm, "end": v(-94.8, -10.21) * mm});
            skArc(sketch, "E1336", {"start": v(-94.8, -10.21) * mm, "mid": v(-95.1, -9.87) * mm, "end": v(-95.4, -9.5) * mm});
            skArc(sketch, "E1337", {"start": v(-95.4, -9.5) * mm, "mid": v(-95.56, -9.23) * mm, "end": v(-95.66, -8.92) * mm});
            skArc(sketch, "E1338", {"start": v(-95.66, -8.92) * mm, "mid": v(-95.65, -8.73) * mm, "end": v(-95.55, -8.56) * mm});
            skArc(sketch, "E1339", {"start": v(-95.55, -8.56) * mm, "mid": v(-95.38, -8.44) * mm, "end": v(-95.17, -8.4) * mm});
            skArc(sketch, "E1340", {"start": v(-95.17, -8.4) * mm, "mid": v(-93.83, -8.58) * mm, "end": v(-92.58, -9.08) * mm});
            skArc(sketch, "E1341", {"start": v(-92.58, -9.08) * mm, "mid": v(-89.13, -11.03) * mm, "end": v(-85.72, -13.04) * mm});
            skArc(sketch, "E1342", {"start": v(-85.72, -13.04) * mm, "mid": v(-82.4, -15.07) * mm, "end": v(-79.11, -17.17) * mm});
            skArc(sketch, "E1343", {"start": v(-79.11, -17.17) * mm, "mid": v(-77.62, -18.32) * mm, "end": v(-76.32, -19.67) * mm});
            skArc(sketch, "E1344", {"start": v(-76.32, -19.67) * mm, "mid": v(-75.54, -20.5) * mm, "end": v(-74.67, -21.23) * mm});
            skArc(sketch, "E1345", {"start": v(-74.67, -21.23) * mm, "mid": v(-73.86, -21.72) * mm, "end": v(-72.96, -22.04) * mm});
            skArc(sketch, "E1346", {"start": v(-72.96, -22.04) * mm, "mid": v(-72.53, -21.99) * mm, "end": v(-72.25, -21.66) * mm});
            skArc(sketch, "E1347", {"start": v(-72.25, -21.66) * mm, "mid": v(-72.18, -21.14) * mm, "end": v(-72.35, -20.64) * mm});
            skArc(sketch, "E1348", {"start": v(-72.35, -20.64) * mm, "mid": v(-72.53, -20.25) * mm, "end": v(-72.63, -19.82) * mm});
            skArc(sketch, "E1349", {"start": v(-72.63, -19.82) * mm, "mid": v(-72.68, -19.14) * mm, "end": v(-72.7, -18.46) * mm});
            skArc(sketch, "E1350", {"start": v(-72.7, -18.46) * mm, "mid": v(-72.65, -17.67) * mm, "end": v(-72.57, -16.87) * mm});
            skArc(sketch, "E1351", {"start": v(-72.57, -16.87) * mm, "mid": v(-72.44, -16.06) * mm, "end": v(-72.26, -15.26) * mm});
            skArc(sketch, "E1352", {"start": v(-72.26, -15.26) * mm, "mid": v(-71.94, -14.06) * mm, "end": v(-71.6, -12.87) * mm});
            skArc(sketch, "E1353", {"start": v(-71.6, -12.87) * mm, "mid": v(-71.42, -12.55) * mm, "end": v(-71.11, -12.33) * mm});
            skArc(sketch, "E1354", {"start": v(-71.11, -12.33) * mm, "mid": v(-70.78, -12.3) * mm, "end": v(-70.5, -12.48) * mm});
            skArc(sketch, "E1355", {"start": v(-70.5, -12.48) * mm, "mid": v(-69.84, -13.25) * mm, "end": v(-69.21, -14.05) * mm});
            skArc(sketch, "E1356", {"start": v(-69.21, -14.05) * mm, "mid": v(-68.6, -14.84) * mm, "end": v(-67.98, -15.61) * mm});
            skArc(sketch, "E1357", {"start": v(-67.98, -15.61) * mm, "mid": v(-67.77, -15.8) * mm, "end": v(-67.5, -15.88) * mm});
            skArc(sketch, "E1358", {"start": v(-67.5, -15.88) * mm, "mid": v(-67.3, -15.82) * mm, "end": v(-67.2, -15.64) * mm});
            skArc(sketch, "E1359", {"start": v(-67.2, -15.64) * mm, "mid": v(-67.13, -14.96) * mm, "end": v(-67.1, -14.28) * mm});
            skArc(sketch, "E1360", {"start": v(-67.1, -14.28) * mm, "mid": v(-67.13, -13.74) * mm, "end": v(-67.24, -13.2) * mm});
            skArc(sketch, "E1361", {"start": v(-67.24, -13.2) * mm, "mid": v(-67.44, -12.6) * mm, "end": v(-67.7, -12.01) * mm});
            skArc(sketch, "E1362", {"start": v(-67.7, -12.01) * mm, "mid": v(-68.01, -11.44) * mm, "end": v(-68.38, -10.9) * mm});
            skArc(sketch, "E1363", {"start": v(-68.38, -10.9) * mm, "mid": v(-68.76, -10.44) * mm, "end": v(-69.19, -10.03) * mm});
            skArc(sketch, "E1364", {"start": v(-69.19, -10.03) * mm, "mid": v(-70.06, -9.05) * mm, "end": v(-70.6, -7.84) * mm});
            skArc(sketch, "E1365", {"start": v(-70.6, -7.84) * mm, "mid": v(-71.27, -5.18) * mm, "end": v(-71.82, -2.5) * mm});
            skArc(sketch, "E1366", {"start": v(-71.82, -2.5) * mm, "mid": v(-72.26, 0.16) * mm, "end": v(-72.61, 2.83) * mm});
            skArc(sketch, "E1367", {"start": v(-72.61, 2.83) * mm, "mid": v(-72.4, 3.52) * mm, "end": v(-71.73, 3.8) * mm});
            skArc(sketch, "E1368", {"start": v(-71.73, 3.81) * mm, "mid": v(-71.49, 3.76) * mm, "end": v(-71.28, 3.63) * mm});
            skArc(sketch, "E1369", {"start": v(-71.28, 3.63) * mm, "mid": v(-70.5, 2.88) * mm, "end": v(-69.7, 2.13) * mm});
            skArc(sketch, "E1370", {"start": v(-69.7, 2.13) * mm, "mid": v(-68.8, 1.22) * mm, "end": v(-67.9, 0.29) * mm});
            skArc(sketch, "E1371", {"start": v(-67.9, 0.29) * mm, "mid": v(-66.87, -0.8) * mm, "end": v(-65.87, -1.9) * mm});
            skArc(sketch, "E1372", {"start": v(-145.65, -3.02) * mm, "mid": v(-146.8, -3.85) * mm, "end": v(-148, -4.63) * mm});
            skArc(sketch, "E1373", {"start": v(-148, -4.63) * mm, "mid": v(-148.71, -4.98) * mm, "end": v(-149.5, -5.17) * mm});
            skArc(sketch, "E1374", {"start": v(-149.5, -5.17) * mm, "mid": v(-150.09, -5.14) * mm, "end": v(-150.63, -4.89) * mm});
            skArc(sketch, "E1375", {"start": v(-150.63, -4.89) * mm, "mid": v(-151.19, -4.4) * mm, "end": v(-151.64, -3.8) * mm});
            skArc(sketch, "E1376", {"start": v(-151.64, -3.8) * mm, "mid": v(-151.74, -3.53) * mm, "end": v(-151.74, -3.23) * mm});
            skArc(sketch, "E1377", {"start": v(-151.74, -3.23) * mm, "mid": v(-151.62, -2.95) * mm, "end": v(-151.4, -2.73) * mm});
            skArc(sketch, "E1378", {"start": v(-151.4, -2.73) * mm, "mid": v(-151.04, -2.52) * mm, "end": v(-150.63, -2.4) * mm});
            skArc(sketch, "E1379", {"start": v(-150.63, -2.4) * mm, "mid": v(-150.09, -2.31) * mm, "end": v(-149.53, -2.29) * mm});
            skArc(sketch, "E1380", {"start": v(-149.53, -2.29) * mm, "mid": v(-148.9, -2.26) * mm, "end": v(-148.3, -2.17) * mm});
            skArc(sketch, "E1381", {"start": v(-148.3, -2.17) * mm, "mid": v(-147.68, -2.02) * mm, "end": v(-147.08, -1.8) * mm});
            skArc(sketch, "E1382", {"start": v(-147.08, -1.8) * mm, "mid": v(-146.57, -1.57) * mm, "end": v(-146.08, -1.28) * mm});
            skArc(sketch, "E1383", {"start": v(-146.08, -1.28) * mm, "mid": v(-145.75, -1) * mm, "end": v(-145.48, -0.66) * mm});
            skArc(sketch, "E1384", {"start": v(-145.48, -0.66) * mm, "mid": v(-145.27, -0.37) * mm, "end": v(-145.03, -0.1) * mm});
            skArc(sketch, "E1385", {"start": v(-145.03, -0.1) * mm, "mid": v(-144.79, 0.09) * mm, "end": v(-144.51, 0.23) * mm});
            skArc(sketch, "E1386", {"start": v(-144.51, 0.23) * mm, "mid": v(-144.26, 0.3) * mm, "end": v(-144, 0.3) * mm});
            skArc(sketch, "E1387", {"start": v(-144, 0.3) * mm, "mid": v(-143.79, 0.22) * mm, "end": v(-143.6, 0.09) * mm});
            skArc(sketch, "E1388", {"start": v(-143.6, 0.09) * mm, "mid": v(-143.46, -0.15) * mm, "end": v(-143.47, -0.41) * mm});
            skArc(sketch, "E1389", {"start": v(-143.47, -0.41) * mm, "mid": v(-143.63, -0.81) * mm, "end": v(-143.84, -1.19) * mm});
            skArc(sketch, "E1390", {"start": v(-143.84, -1.19) * mm, "mid": v(-144.2, -1.66) * mm, "end": v(-144.6, -2.1) * mm});
            skArc(sketch, "E1391", {"start": v(-144.6, -2.1) * mm, "mid": v(-145.1, -2.57) * mm, "end": v(-145.65, -3.02) * mm});
            skArc(sketch, "E1392", {"start": v(-23.27, -16.92) * mm, "mid": v(-23.82, -17.25) * mm, "end": v(-24.45, -17.27) * mm});
            skArc(sketch, "E1393", {"start": v(-24.45, -17.27) * mm, "mid": v(-25.5, -16.98) * mm, "end": v(-26.51, -16.58) * mm});
            skArc(sketch, "E1394", {"start": v(-26.51, -16.58) * mm, "mid": v(-27.48, -16.06) * mm, "end": v(-28.39, -15.43) * mm});
            skArc(sketch, "E1395", {"start": v(-28.39, -15.43) * mm, "mid": v(-28.8, -14.91) * mm, "end": v(-28.96, -14.26) * mm});
            skArc(sketch, "E1396", {"start": v(-28.96, -14.26) * mm, "mid": v(-28.88, -14.02) * mm, "end": v(-28.7, -13.87) * mm});
            skArc(sketch, "E1397", {"start": v(-28.7, -13.87) * mm, "mid": v(-28.36, -13.77) * mm, "end": v(-28.02, -13.76) * mm});
            skArc(sketch, "E1398", {"start": v(-28.02, -13.76) * mm, "mid": v(-27.5, -13.84) * mm, "end": v(-27, -14) * mm});
            skArc(sketch, "E1399", {"start": v(-27, -14) * mm, "mid": v(-26.38, -14.25) * mm, "end": v(-25.78, -14.55) * mm});
            skArc(sketch, "E1400", {"start": v(-25.78, -14.55) * mm, "mid": v(-25.18, -14.88) * mm, "end": v(-24.6, -15.25) * mm});
            skArc(sketch, "E1401", {"start": v(-24.6, -15.25) * mm, "mid": v(-24.15, -15.58) * mm, "end": v(-23.73, -15.95) * mm});
            skArc(sketch, "E1402", {"start": v(-23.73, -15.95) * mm, "mid": v(-23.46, -16.23) * mm, "end": v(-23.23, -16.55) * mm});
            skArc(sketch, "E1403", {"start": v(-23.23, -16.55) * mm, "mid": v(-23.19, -16.74) * mm, "end": v(-23.27, -16.92) * mm});
            skArc(sketch, "E1404", {"start": v(-15.7, -20.5) * mm, "mid": v(-14.63, -21.12) * mm, "end": v(-13.52, -21.68) * mm});
            skArc(sketch, "E1405", {"start": v(-13.52, -21.68) * mm, "mid": v(-12.27, -22.24) * mm, "end": v(-11, -22.74) * mm});
            skArc(sketch, "E1406", {"start": v(-11, -22.74) * mm, "mid": v(-9.78, -23.17) * mm, "end": v(-8.54, -23.55) * mm});
            skArc(sketch, "E1407", {"start": v(-8.54, -23.55) * mm, "mid": v(-7.55, -23.78) * mm, "end": v(-6.56, -23.93) * mm});
            skArc(sketch, "E1408", {"start": v(-6.56, -23.93) * mm, "mid": v(-5.62, -24.07) * mm, "end": v(-4.7, -24.3) * mm});
            skArc(sketch, "E1409", {"start": v(-4.7, -24.3) * mm, "mid": v(-3.68, -24.64) * mm, "end": v(-2.67, -25.04) * mm});
            skArc(sketch, "E1410", {"start": v(-2.67, -25.04) * mm, "mid": v(-1.7, -25.49) * mm, "end": v(-0.77, -26) * mm});
            skArc(sketch, "E1411", {"start": v(-0.77, -26) * mm, "mid": v(-0.02, -26.49) * mm, "end": v(0.67, -27.05) * mm});
            skArc(sketch, "E1412", {"start": v(0.67, -27.05) * mm, "mid": v(1.3, -27.59) * mm, "end": v(1.97, -28.07) * mm});
            skArc(sketch, "E1413", {"start": v(1.97, -28.07) * mm, "mid": v(2.52, -28.38) * mm, "end": v(3.1, -28.6) * mm});
            skArc(sketch, "E1414", {"start": v(3.1, -28.6) * mm, "mid": v(3.54, -28.66) * mm, "end": v(3.98, -28.6) * mm});
            skArc(sketch, "E1415", {"start": v(3.98, -28.6) * mm, "mid": v(4.33, -28.44) * mm, "end": v(4.6, -28.16) * mm});
            skArc(sketch, "E1416", {"start": v(4.6, -28.16) * mm, "mid": v(4.91, -27.81) * mm, "end": v(5.34, -27.61) * mm});
            skArc(sketch, "E1417", {"start": v(5.34, -27.61) * mm, "mid": v(5.95, -27.51) * mm, "end": v(6.57, -27.51) * mm});
            skArc(sketch, "E1418", {"start": v(6.57, -27.51) * mm, "mid": v(7.45, -27.64) * mm, "end": v(8.3, -27.86) * mm});
            skArc(sketch, "E1419", {"start": v(8.3, -27.86) * mm, "mid": v(9.44, -28.25) * mm, "end": v(10.56, -28.7) * mm});
            skArc(sketch, "E1420", {"start": v(10.56, -28.7) * mm, "mid": v(11.84, -29.25) * mm, "end": v(13.1, -29.83) * mm});
            skArc(sketch, "E1421", {"start": v(13.1, -29.83) * mm, "mid": v(13.6, -30.15) * mm, "end": v(14.02, -30.57) * mm});
            skArc(sketch, "E1422", {"start": v(14.02, -30.57) * mm, "mid": v(14.11, -30.89) * mm, "end": v(13.96, -31.18) * mm});
            skArc(sketch, "E1423", {"start": v(13.96, -31.18) * mm, "mid": v(13.5, -31.53) * mm, "end": v(12.99, -31.78) * mm});
            skArc(sketch, "E1424", {"start": v(12.99, -31.78) * mm, "mid": v(11.32, -32.3) * mm, "end": v(9.6, -32.6) * mm});
            skArc(sketch, "E1425", {"start": v(9.6, -32.6) * mm, "mid": v(7.68, -32.73) * mm, "end": v(5.74, -32.68) * mm});
            skArc(sketch, "E1426", {"start": v(5.74, -32.68) * mm, "mid": v(3.87, -32.45) * mm, "end": v(2.04, -32.05) * mm});
            skArc(sketch, "E1427", {"start": v(2.04, -32.05) * mm, "mid": v(0.56, -31.53) * mm, "end": v(-0.8, -30.77) * mm});
            skArc(sketch, "E1428", {"start": v(-0.8, -30.77) * mm, "mid": v(-1.6, -30.29) * mm, "end": v(-2.42, -29.87) * mm});
            skArc(sketch, "E1429", {"start": v(-2.42, -29.87) * mm, "mid": v(-3.67, -29.31) * mm, "end": v(-4.94, -28.78) * mm});
            skArc(sketch, "E1430", {"start": v(-4.94, -28.78) * mm, "mid": v(-6.38, -28.23) * mm, "end": v(-7.82, -27.7) * mm});
            skArc(sketch, "E1431", {"start": v(-7.82, -27.7) * mm, "mid": v(-9.24, -27.24) * mm, "end": v(-10.67, -26.81) * mm});
            skArc(sketch, "E1432", {"start": v(-10.67, -26.81) * mm, "mid": v(-12.18, -26.37) * mm, "end": v(-13.68, -25.9) * mm});
            skArc(sketch, "E1433", {"start": v(-13.68, -25.9) * mm, "mid": v(-15.38, -25.33) * mm, "end": v(-17.08, -24.74) * mm});
            skArc(sketch, "E1434", {"start": v(-17.08, -24.74) * mm, "mid": v(-18.7, -24.16) * mm, "end": v(-20.33, -23.55) * mm});
            skArc(sketch, "E1435", {"start": v(-20.33, -23.55) * mm, "mid": v(-21.6, -23.05) * mm, "end": v(-22.86, -22.52) * mm});
            skArc(sketch, "E1436", {"start": v(-22.86, -22.52) * mm, "mid": v(-24.44, -21.81) * mm, "end": v(-26.01, -21.08) * mm});
            skArc(sketch, "E1437", {"start": v(-26.01, -21.08) * mm, "mid": v(-26.47, -20.78) * mm, "end": v(-26.83, -20.37) * mm});
            skArc(sketch, "E1438", {"start": v(-26.83, -20.37) * mm, "mid": v(-26.89, -20.02) * mm, "end": v(-26.68, -19.74) * mm});
            skArc(sketch, "E1439", {"start": v(-26.68, -19.74) * mm, "mid": v(-25.93, -19.32) * mm, "end": v(-25.15, -18.96) * mm});
            skArc(sketch, "E1440", {"start": v(-25.15, -18.96) * mm, "mid": v(-23.76, -18.44) * mm, "end": v(-22.36, -17.97) * mm});
            skArc(sketch, "E1441", {"start": v(-22.36, -17.97) * mm, "mid": v(-21.61, -17.82) * mm, "end": v(-20.85, -17.86) * mm});
            skArc(sketch, "E1442", {"start": v(-20.85, -17.86) * mm, "mid": v(-20.03, -18.07) * mm, "end": v(-19.26, -18.42) * mm});
            skArc(sketch, "E1443", {"start": v(-19.26, -18.42) * mm, "mid": v(-17.47, -19.45) * mm, "end": v(-15.7, -20.5) * mm});
            skSolve(sketch);
        }
        {
            var Q0;
            Q0=makeQuery(id+"F0.imprint","IMPRINT",FACE,{"disambiguationData":[TD([[makeQuery(id+"F0.imprint","IMPRINT",EDGE,{"derivedFrom":sQuery(id+"F0.wireOp",EDGE,"E0")}),1.0]])]});
            extrude(context, id + "F1", {"entities" : qUnion([Q0]), "depth" : 3.17 * mm, "offsetDistance" : 25.4 * mm});
        }
    });
